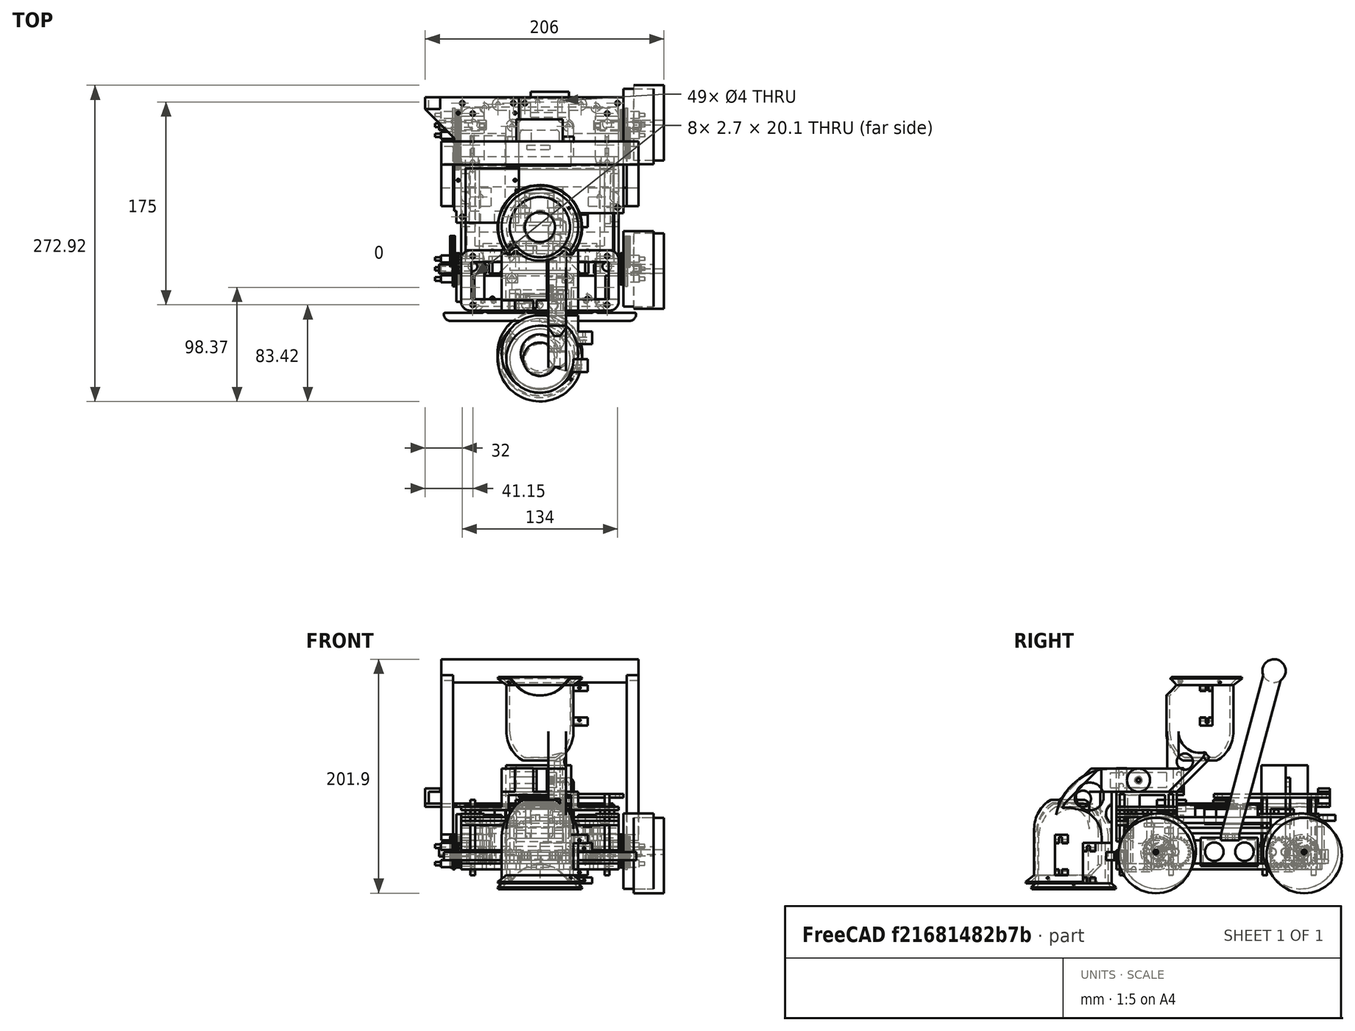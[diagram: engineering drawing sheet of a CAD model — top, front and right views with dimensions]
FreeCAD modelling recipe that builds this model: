
FCSTD DOCUMENT  (FreeCAD 1.0R39319 (Git))
Label: robot - robcup-ber4a3
License: All rights reserved
LicenseURL: https://en.wikipedia.org/wiki/All_rights_reserved
objects: Part::Cylinder×264, Part::Box×177, Part::Cut×164, Part::MultiFuse×149, Part::Fillet×33, Part::FeaturePython×22, Part::Sphere×14, Part::Chamfer×13, Part::Cone×8, Part::Part2DObjectPython×4, Part::Extrusion×4
note: 852 computed .brp shape members not serialized (recipe doc carries the construction recipe); baked Part::Feature solids carry a one-line shape summary decoded from their .brp

FEATURE [Part::Box] Box024  label="立方体004"
  AttacherType = Attacher::AttachEngine3D
  Height = 25
  Length = 51
  Placement = pos=(-51,-93,16) rot=(0,0,1;0rad)
  Width = 5
FEATURE [Part::Box] Box025  label="立方体005"
  AttacherType = Attacher::AttachEngine3D
  Height = 25
  Length = 23
  Placement = pos=(-37,-93,16) rot=(0,0,1;0rad)
  Width = 5
FEATURE [Part::Box] Box026  label="立方体006"
  AttacherType = Attacher::AttachEngine3D
  Height = 10
  Length = 51
  Placement = pos=(-51,-90,31) rot=(0,0,1;0rad)
  Width = 5
FEATURE [Part::Cylinder] Cylinder007  label="円柱007"
  Angle = 360
  AttacherType = Attacher::AttachEngine3D
  FirstAngle = 0
  Height = 32
  Placement = pos=(0,82,0) rot=(0,0,1;0rad)
  Radius = 4
  SecondAngle = 0
FEATURE [Part::Cylinder] Cylinder011  label="円柱011"
  Angle = 360
  AttacherType = Attacher::AttachEngine3D
  FirstAngle = 0
  Height = 32
  Placement = pos=(15.2,-98,0) rot=(0,0,1;0rad)
  Radius = 4
  SecondAngle = 0
FEATURE [Part::Cylinder] Cylinder012  label="円柱012"
  Angle = 360
  AttacherType = Attacher::AttachEngine3D
  FirstAngle = 0
  Height = 42
  Placement = pos=(-68,82,-5) rot=(0,0,1;0rad)
  Radius = 2
  SecondAngle = 0
FEATURE [Part::Box] Box069  label="立方体048"
  AttacherType = Attacher::AttachEngine3D
  Height = 20.1
  Length = 38.8
  Placement = pos=(82,-93,0) rot=(0,0,1;0rad)
  Width = 40.1
FEATURE [Part::Box] Box075  label="立方体054"
  AttacherType = Attacher::AttachEngine3D
  Height = 20.1
  Length = 38.8
  Placement = pos=(82,-93,0) rot=(0,0,1;0rad)
  Width = 40.1
FEATURE [Part::Box] Box084  label="立方体063"
  AttacherType = Attacher::AttachEngine3D
  Height = 20.1
  Length = 2.7
  Placement = pos=(90.8,-99.95,0) rot=(0,0,1;0rad)
  Width = 54
FEATURE [Part::Box] Box097  label="立方体076"
  AttacherType = Attacher::AttachEngine3D
  Height = 25
  Length = 52
  Placement = pos=(-60,-93,16) rot=(0,0,1;0rad)
  Width = 5
FEATURE [Part::Box] Box098  label="立方体077"
  AttacherType = Attacher::AttachEngine3D
  Height = 25
  Length = 35
  Placement = pos=(-52,-88,16) rot=(0,0,1;0rad)
  Width = 5
FEATURE [Part::Box] Box100  label="立方体079"
  AttacherType = Attacher::AttachEngine3D
  Height = 25
  Length = 25
  Placement = pos=(-38.5,-94,16) rot=(0,0,1;0rad)
  Width = 1
FEATURE [Part::Box] Box101  label="立方体080"
  AttacherType = Attacher::AttachEngine3D
  Height = 25
  Length = 15
  Placement = pos=(-33.5,-101,16) rot=(0,0,1;0rad)
  Width = 7
FEATURE [Part::Box] Box102  label="立方体081"
  AttacherType = Attacher::AttachEngine3D
  Height = 5
  Length = 112
  Placement = pos=(-90,-52,-5) rot=(0,0,1;0rad)
  Width = 66
FEATURE [Part::Cylinder] Cylinder033  label="円柱033"
  Angle = 360
  AttacherType = Attacher::AttachEngine3D
  FirstAngle = 0
  Height = 32
  Placement = pos=(30.2,-10,0) rot=(0,0,1;0rad)
  Radius = 4
  SecondAngle = 0
FEATURE [Part::Cylinder] Cylinder034  label="円柱034"
  Angle = 360
  AttacherType = Attacher::AttachEngine3D
  FirstAngle = 0
  Height = 32
  Placement = pos=(-98,-10,0) rot=(0,0,1;0rad)
  Radius = 4
  SecondAngle = 0
FEATURE [Part::Box] Box223  label="立方体201"
  AttacherType = Attacher::AttachEngine3D
  Height = 20.1
  Length = 2.7
  Placement = pos=(90.8,-99.95,0) rot=(0,0,1;0rad)
  Width = 54
FEATURE [Part::Box] Box225  label="立方体203"
  AttacherType = Attacher::AttachEngine3D
  Height = 20.1
  Length = 2.7
  Placement = pos=(109.3,-99.95,0) rot=(0,0,1;0rad)
  Width = 54
FEATURE [Part::MultiFuse] Fusion084
  Placement = pos=(-188,26,0) rot=(0,0,1;0rad)
  Shapes = -> [Box084,Box069]
FEATURE [Part::MultiFuse] Fusion085
  Placement = pos=(-188,100,0) rot=(0,0,1;0rad)
  Shapes = -> [Box223,Box075]
FEATURE [Part::Box] Box226  label="立方体204"
  AttacherType = Attacher::AttachEngine3D
  Height = 20.1
  Length = 38.8
  Placement = pos=(82,-93,0) rot=(0,0,1;0rad)
  Width = 40.1
FEATURE [Part::Box] Box227  label="立方体205"
  AttacherType = Attacher::AttachEngine3D
  Height = 20.1
  Length = 38.8
  Placement = pos=(82,-93,0) rot=(0,0,1;0rad)
  Width = 40.1
FEATURE [Part::MultiFuse] Fusion086
  Placement = pos=(-82.6,26,0) rot=(0,0,1;0rad)
  Shapes = -> [Box226,Box225]
FEATURE [Part::Box] Box076  label="立方体055"
  AttacherType = Attacher::AttachEngine3D
  Height = 20.1
  Length = 2.7
  Placement = pos=(109.3,-99.95,0) rot=(0,0,1;0rad)
  Width = 54
FEATURE [Part::MultiFuse] Fusion087
  Placement = pos=(-82.6,100,0) rot=(0,0,1;0rad)
  Shapes = -> [Box076,Box227]
FEATURE [Part::FeaturePython] CycloidGear  # WARN: FeaturePython — macro-defined, semantics opaque (R4)
  AttacherType = Attacher::AttachEngine3D
  Placement = pos=(-32.8,-91,71) rot=(0,1,0;1.5708rad)
  angular_backlash = 0
  backlash = 0
  clearance = 0.25
  double_helix = false
  head = 0
  head_fillet = 0
  height = 5.5
  helix_angle = 0
  inner_diameter = 12.5
  module = 0.24
  num_teeth = 25
  numpoints = 20
  outer_diameter = 7.5
  pitch_diameter = 6
  root_fillet = 0
  version = 1.3.0
  expr: angular_backlash = backlash / pitch_diameter * 360 ° / pi
  expr: inner_diameter = num_teeth / 2
  expr: pitch_diameter = num_teeth * module
FEATURE [Part::Box] Box259  label="立方体234"
  AttacherType = Attacher::AttachEngine3D
  Height = 3
  Length = 90
  Placement = pos=(-52,-40,42) rot=(0,0,1;0rad)
  Width = 100
FEATURE [Part::Box] Box260  label="立方体235"
  AttacherType = Attacher::AttachEngine3D
  Height = 3
  Length = 56
  Placement = pos=(-104,-22,37) rot=(0,0,1;0rad)
  Width = 88
FEATURE [Part::Cylinder] Cylinder064  label="円柱064"
  Angle = 360
  AttacherType = Attacher::AttachEngine3D
  FirstAngle = 0
  Height = 3
  Placement = pos=(-100.5,62.5,37) rot=(0,0,1;0rad)
  Radius = 1.25
  SecondAngle = 0
FEATURE [Part::Cylinder] Cylinder065  label="円柱065"
  Angle = 360
  AttacherType = Attacher::AttachEngine3D
  FirstAngle = 0
  Height = 3
  Placement = pos=(-51.5,62.5,37) rot=(0,0,1;0rad)
  Radius = 1.25
  SecondAngle = 0
FEATURE [Part::Cylinder] Cylinder066  label="円柱066"
  Angle = 360
  AttacherType = Attacher::AttachEngine3D
  FirstAngle = 0
  Height = 3
  Placement = pos=(-51.5,4.5,37) rot=(0,0,1;0rad)
  Radius = 1.25
  SecondAngle = 0
FEATURE [Part::Cylinder] Cylinder067  label="円柱067"
  Angle = 360
  AttacherType = Attacher::AttachEngine3D
  FirstAngle = 0
  Height = 3
  Placement = pos=(-100.5,4.5,37) rot=(0,0,1;0rad)
  Radius = 1.25
  SecondAngle = 0
FEATURE [Part::Box] Box263  label="立方体237"
  AttacherType = Attacher::AttachEngine3D
  Height = 20.4
  Length = 45.2
  Placement = pos=(-48.6,-98,10) rot=(0,0,1;0rad)
  Width = 5
FEATURE [Part::Cylinder] Cylinder068  label="円柱068"
  Angle = 360
  AttacherType = Attacher::AttachEngine3D
  FirstAngle = 0
  Height = 15
  Placement = pos=(-13,-93,20.2) rot=(1,0,0;1.5708rad)
  Radius = 8
  SecondAngle = 0
FEATURE [Part::Cylinder] Cylinder069  label="円柱069"
  Angle = 360
  AttacherType = Attacher::AttachEngine3D
  FirstAngle = 0
  Height = 15
  Placement = pos=(-39,-93,20.2) rot=(1,0,0;1.5708rad)
  Radius = 8
  SecondAngle = 0
FEATURE [Part::MultiFuse] Fusion112
  Placement = pos=(0,-109,40) rot=(0,0,-1;1.5708rad)
  Refine = true
  Shapes = -> [Box263,Cylinder069,Cylinder068]
FEATURE [Part::Box] Box264  label="立方体238"
  AttacherType = Attacher::AttachEngine3D
  Height = 20.4
  Length = 45.2
  Placement = pos=(-48.6,-98,10) rot=(0,0,1;0rad)
  Width = 5
FEATURE [Part::Cylinder] Cylinder070  label="円柱070"
  Angle = 360
  AttacherType = Attacher::AttachEngine3D
  FirstAngle = 0
  Height = 15
  Placement = pos=(-13,-93,20.2) rot=(1,0,0;1.5708rad)
  Radius = 8
  SecondAngle = 0
FEATURE [Part::Cylinder] Cylinder071  label="円柱071"
  Angle = 360
  AttacherType = Attacher::AttachEngine3D
  FirstAngle = 0
  Height = 15
  Placement = pos=(-39,-93,20.2) rot=(1,0,0;1.5708rad)
  Radius = 8
  SecondAngle = 0
FEATURE [Part::MultiFuse] Fusion113
  Placement = pos=(-67,-57,40) rot=(0,0,1;1.5708rad)
  Refine = true
  Shapes = -> [Box264,Cylinder071,Cylinder070]
FEATURE [Part::Box] Box266  label="立方体240"
  AttacherType = Attacher::AttachEngine3D
  Height = 49.2
  Length = 12
  Placement = pos=(-105,-58.4,48) rot=(1,0,0;1.5708rad)
  Width = 24.4
FEATURE [Part::Box] Box268  label="立方体242"
  AttacherType = Attacher::AttachEngine3D
  Height = 49.2
  Length = 12
  Placement = pos=(26,-58.4,48) rot=(1,0,0;1.5708rad)
  Width = 24.4
FEATURE [Part::Cylinder] Cylinder072  label="円柱072"
  Angle = 360
  AttacherType = Attacher::AttachEngine3D
  FirstAngle = 0
  Height = 40.5
  Placement = pos=(-125,62,10) rot=(0,1,0;1.5708rad)
  Radius = 4
  SecondAngle = 0
FEATURE [Part::FeaturePython] CycloidGear001  # WARN: FeaturePython — macro-defined, semantics opaque (R4)
  AttacherType = Attacher::AttachEngine3D
  Placement = pos=(-111.4,62,10) rot=(0,1,0;1.5708rad)
  angular_backlash = 0
  backlash = 0
  clearance = 0.25
  double_helix = false
  head = 0
  head_fillet = 0
  height = 4
  helix_angle = 0
  inner_diameter = 12.5
  module = 1
  num_teeth = 25
  numpoints = 20
  outer_diameter = 7.5
  pitch_diameter = 25
  root_fillet = 0
  version = 1.3.0
  expr: angular_backlash = backlash / pitch_diameter * 360 ° / pi
  expr: inner_diameter = num_teeth / 2
  expr: pitch_diameter = num_teeth * module
FEATURE [Part::FeaturePython] CycloidGear002  # WARN: FeaturePython — macro-defined, semantics opaque (R4)
  AttacherType = Attacher::AttachEngine3D
  Placement = pos=(-111.45,37,10) rot=(0,1,0;1.5708rad)
  angular_backlash = 0
  backlash = 0
  clearance = 0.25
  double_helix = false
  head = 0
  head_fillet = 0
  height = 4
  helix_angle = 0
  inner_diameter = 12.5
  module = 1
  num_teeth = 25
  numpoints = 20
  outer_diameter = 7.5
  pitch_diameter = 25
  root_fillet = 0
  version = 1.3.0
  expr: angular_backlash = backlash / pitch_diameter * 360 ° / pi
  expr: inner_diameter = num_teeth / 2
  expr: pitch_diameter = num_teeth * module
FEATURE [Part::FeaturePython] CycloidGear003  # WARN: FeaturePython — macro-defined, semantics opaque (R4)
  AttacherType = Attacher::AttachEngine3D
  Placement = pos=(-111.45,37,10) rot=(0,1,0;1.5708rad)
  angular_backlash = 0
  backlash = 0
  clearance = 0.25
  double_helix = false
  head = 0
  head_fillet = 0
  height = 4
  helix_angle = 0
  inner_diameter = 12.5
  module = 0.24
  num_teeth = 25
  numpoints = 20
  outer_diameter = 7.5
  pitch_diameter = 6
  root_fillet = 0
  version = 1.3.0
  expr: angular_backlash = backlash / pitch_diameter * 360 ° / pi
  expr: inner_diameter = num_teeth / 2
  expr: pitch_diameter = num_teeth * module
FEATURE [Part::Sphere] Sphere  label="球体"
  Angle1 = 0
  Angle2 = 60
  Angle3 = 360
  AttacherType = Attacher::AttachEngine3D
  Placement = pos=(-34,-160,45) rot=(0,0,1;0rad)
  Radius = 33
FEATURE [Part::Sphere] Sphere001  label="球体001"
  Angle1 = 0
  Angle2 = 60
  Angle3 = 360
  AttacherType = Attacher::AttachEngine3D
  Placement = pos=(-34,-160,45) rot=(0,0,1;0rad)
  Radius = 30
FEATURE [Part::Cone] Cone  label="円錐"
  Angle = 360
  AttacherType = Attacher::AttachEngine3D
  Height = 5
  Radius1 = 38
  Radius2 = 33
FEATURE [Part::Cone] Cone001  label="円錐001"
  Angle = 360
  AttacherType = Attacher::AttachEngine3D
  Height = 5
  Radius1 = 33
  Radius2 = 30
FEATURE [Part::Cut] Cut053
  Base = -> Cone
  Placement = pos=(-34,-160,0) rot=(0,0,1;0rad)
  Tool = -> Cone001
FEATURE [Part::Chamfer] Chamfer016
  Base = -> Cut053
  EdgeLinks = -> Cut053 [Edge3]
  Edges = 1 edges r=2: [Edge3]
FEATURE [Part::Cylinder] Cylinder073  label="円柱073"
  Angle = 360
  AttacherType = Attacher::AttachEngine3D
  FirstAngle = 0
  Height = 20
  Placement = pos=(-60,-160,-3) rot=(0,-1,0;0.785398rad)
  Radius = 1
  SecondAngle = 0
FEATURE [Part::Cylinder] Cylinder074  label="円柱074"
  Angle = 360
  AttacherType = Attacher::AttachEngine3D
  FirstAngle = 0
  Height = 20
  Placement = pos=(-8,-160,-3) rot=(0,1,0;0.785398rad)
  Radius = 1
  SecondAngle = 0
FEATURE [Part::Box] Box273  label="立方体246"
  AttacherType = Attacher::AttachEngine3D
  Height = 20.1
  Length = 2.7
  Placement = pos=(109.3,-99.95,0) rot=(0,0,1;0rad)
  Width = 54
FEATURE [Part::Box] Box274  label="立方体247"
  AttacherType = Attacher::AttachEngine3D
  Height = 20.1
  Length = 38.8
  Placement = pos=(82,-93,0) rot=(0,0,1;0rad)
  Width = 40.1
FEATURE [Part::MultiFuse] Fusion118
  Placement = pos=(-153.6,-8,61) rot=(0,0,1;0rad)
  Shapes = -> [Box274,Box273]
FEATURE [Part::Cylinder] Cylinder076  label="円柱076"
  Angle = 360
  AttacherType = Attacher::AttachEngine3D
  FirstAngle = 0
  Height = 50
  Placement = pos=(-34,-160,-17) rot=(0,0,1;0rad)
  Radius = 33
  SecondAngle = 0
FEATURE [Part::Box] Box278  label="立方体250"
  AttacherType = Attacher::AttachEngine3D
  Height = 35
  Length = 45.1
  Placement = pos=(-34,-146,-17) rot=(0,0,1;0rad)
  Width = 25
FEATURE [Part::Box] Box279  label="立方体251"
  AttacherType = Attacher::AttachEngine3D
  Height = 32.3
  Length = 12.1
  Placement = pos=(0,8.5,-4.9) rot=(0,0,1;0rad)
  Width = 2.5
FEATURE [Part::Box] Box280  label="立方体252"
  AttacherType = Attacher::AttachEngine3D
  Height = 22.5
  Length = 12.1
  Width = 26.7
FEATURE [Part::Cylinder] Cylinder077  label="円柱077"
  Angle = 360
  AttacherType = Attacher::AttachEngine3D
  FirstAngle = 0
  Height = 3
  Placement = pos=(6.05,0,16.4) rot=(1,0,0;1.5708rad)
  Radius = 2.4
  SecondAngle = 0
FEATURE [Part::MultiFuse] Fusion120
  Placement = pos=(-1,-151,-12) rot=(0,0,1;0rad)
  Shapes = -> [Cylinder077,Box279,Box280]
FEATURE [Part::Cut] Cut056
  Base = -> Box278
  Tool = -> Fusion120
FEATURE [Part::Cut] Cut057
  Base = -> Cut056
  Placement = pos=(0,15,-3) rot=(0,0,1;0rad)
  Tool = -> Cylinder076
FEATURE [Part::MultiFuse] Fusion121
  Placement = pos=(0,0,-3) rot=(0,0,1;0rad)
  Shapes = -> [Fusion118,CycloidGear]
FEATURE [Part::Box] Box281  label="立方体253"
  AttacherType = Attacher::AttachEngine3D
  Height = 20.1
  Length = 16
  Placement = pos=(-60.3,-108,62) rot=(0,0,1;0rad)
  Width = 9
FEATURE [Part::Box] Box283  label="立方体255"
  AttacherType = Attacher::AttachEngine3D
  Height = 3
  Length = 66
  Placement = pos=(-71.6,-108,59) rot=(0,0,1;0rad)
  Width = 58.1
FEATURE [Part::Box] Box286  label="立方体258"
  AttacherType = Attacher::AttachEngine3D
  Height = 16
  Length = 6
  Placement = pos=(-67,-108,46.1) rot=(0,0,1;0rad)
  Width = 9.9
FEATURE [Part::Box] Box288  label="立方体260"
  AttacherType = Attacher::AttachEngine3D
  Height = 16
  Length = 6
  Placement = pos=(-7,-108,46.1) rot=(0,0,1;0rad)
  Width = 20
FEATURE [Part::Cylinder] Cylinder083  label="円柱083"
  Angle = 360
  AttacherType = Attacher::AttachEngine3D
  FirstAngle = 0
  Height = 15
  Placement = pos=(-31.3,-89,72) rot=(0.57735,0.57735,0.57735;2.0944rad)
  Radius = 10
  SecondAngle = 0
FEATURE [Part::Box] Box289  label="立方体261"
  AttacherType = Attacher::AttachEngine3D
  Height = 20
  Length = 15
  Placement = pos=(-31.3,-112,62) rot=(0,0,1;0rad)
  Width = 23
FEATURE [Part::Cylinder] Cylinder084  label="円柱084"
  Angle = 360
  AttacherType = Attacher::AttachEngine3D
  FirstAngle = 0
  Height = 50
  Placement = pos=(-34,-145,-27) rot=(0,0,1;0rad)
  Radius = 30
  SecondAngle = 0
FEATURE [Part::Sphere] Sphere003  label="球体003"
  Angle1 = 0
  Angle2 = 60
  Angle3 = 360
  AttacherType = Attacher::AttachEngine3D
  Placement = pos=(-34,-145,23) rot=(0,0,1;0rad)
  Radius = 30
FEATURE [Part::Cylinder] Cylinder085  label="円柱085"
  Angle = 360
  AttacherType = Attacher::AttachEngine3D
  FirstAngle = 0
  Height = 5
  Placement = pos=(-128.4,53.35,15) rot=(0,1,0;1.5708rad)
  Radius = 1.5
  SecondAngle = 0
FEATURE [Part::FeaturePython] Tube  # WARN: FeaturePython — macro-defined, semantics opaque (R4)
  AttacherType = Attacher::AttachEngine3D
  Height = 2
  InnerRadius = 6
  OuterRadius = 15
  Placement = pos=(-113.4,62,10) rot=(0,1,0;1.5708rad)
FEATURE [Part::Cylinder] Cylinder086  label="円柱086"
  Angle = 360
  AttacherType = Attacher::AttachEngine3D
  FirstAngle = 0
  Height = 5
  Placement = pos=(-128.4,70.66,15) rot=(0,1,0;1.5708rad)
  Radius = 1.5
  SecondAngle = 0
FEATURE [Part::Cylinder] Cylinder087  label="円柱087"
  Angle = 360
  AttacherType = Attacher::AttachEngine3D
  FirstAngle = 0
  Height = 5
  Placement = pos=(-128.4,62,0) rot=(0,1,0;1.5708rad)
  Radius = 1.5
  SecondAngle = 0
FEATURE [Part::FeaturePython] CycloidGear004  # WARN: FeaturePython — macro-defined, semantics opaque (R4)
  AttacherType = Attacher::AttachEngine3D
  Placement = pos=(39.6,62,10) rot=(0,1,0;1.5708rad)
  angular_backlash = 0
  backlash = 0
  clearance = 0.25
  double_helix = false
  head = 0
  head_fillet = 0
  height = 4
  helix_angle = 0
  inner_diameter = 12.5
  module = 1
  num_teeth = 25
  numpoints = 20
  outer_diameter = 7.5
  pitch_diameter = 25
  root_fillet = 0
  version = 1.3.0
  expr: angular_backlash = backlash / pitch_diameter * 360 ° / pi
  expr: inner_diameter = num_teeth / 2
  expr: pitch_diameter = num_teeth * module
FEATURE [Part::Cut] Cut062  label="右下モーター側ギア"
  Base = -> CycloidGear002
  Placement = pos=(4,-10,0) rot=(0,0,1;0rad)
  Tool = -> CycloidGear003
FEATURE [Part::FeaturePython] CycloidGear007  # WARN: FeaturePython — macro-defined, semantics opaque (R4)
  AttacherType = Attacher::AttachEngine3D
  Placement = pos=(-111.45,37,10) rot=(0,1,0;1.5708rad)
  angular_backlash = 0
  backlash = 0
  clearance = 0.25
  double_helix = false
  head = 0
  head_fillet = 0
  height = 4
  helix_angle = 0
  inner_diameter = 12.5
  module = 1
  num_teeth = 25
  numpoints = 20
  outer_diameter = 7.5
  pitch_diameter = 25
  root_fillet = 0
  version = 1.3.0
  expr: angular_backlash = backlash / pitch_diameter * 360 ° / pi
  expr: inner_diameter = num_teeth / 2
  expr: pitch_diameter = num_teeth * module
FEATURE [Part::FeaturePython] CycloidGear008  # WARN: FeaturePython — macro-defined, semantics opaque (R4)
  AttacherType = Attacher::AttachEngine3D
  Placement = pos=(-111.45,37,10) rot=(0,1,0;1.5708rad)
  angular_backlash = 0
  backlash = 0
  clearance = 0.25
  double_helix = false
  head = 0
  head_fillet = 0
  height = 4
  helix_angle = 0
  inner_diameter = 12.5
  module = 0.24
  num_teeth = 25
  numpoints = 20
  outer_diameter = 7.5
  pitch_diameter = 6
  root_fillet = 0
  version = 1.3.0
  expr: angular_backlash = backlash / pitch_diameter * 360 ° / pi
  expr: inner_diameter = num_teeth / 2
  expr: pitch_diameter = num_teeth * module
FEATURE [Part::Cut] Cut064  label="左下モーター側ギア"
  Base = -> CycloidGear007
  Placement = pos=(151.05,0,0) rot=(0,0,1;0rad)
  Tool = -> CycloidGear008
FEATURE [Part::Cylinder] Cylinder088  label="円柱088"
  Angle = 360
  AttacherType = Attacher::AttachEngine3D
  FirstAngle = 0
  Height = 10
  Placement = pos=(-123.4,70.66,15) rot=(0,1,0;1.5708rad)
  Radius = 3
  SecondAngle = 0
FEATURE [Part::Cylinder] Cylinder089  label="円柱089"
  Angle = 360
  AttacherType = Attacher::AttachEngine3D
  FirstAngle = 0
  Height = 10
  Placement = pos=(-123.4,-90.65,15) rot=(0,1,0;1.5708rad)
  Radius = 3
  SecondAngle = 0
FEATURE [Part::Cylinder] Cylinder090  label="円柱090"
  Angle = 360
  AttacherType = Attacher::AttachEngine3D
  FirstAngle = 0
  Height = 10
  Placement = pos=(-123.4,62,0) rot=(0,1,0;1.5708rad)
  Radius = 3
  SecondAngle = 0
FEATURE [Part::Box] Box297  label="立方体269"
  AttacherType = Attacher::AttachEngine3D
  Height = 13
  Length = 30
  Placement = pos=(-94,-22,34) rot=(0,0,1;0rad)
  Width = 65
FEATURE [Part::Cylinder] Cylinder091  label="円柱091"
  Angle = 360
  AttacherType = Attacher::AttachEngine3D
  FirstAngle = 0
  Height = 1.4
  Placement = pos=(-107.4,62,10) rot=(0,1,0;1.5708rad)
  Radius = 5
  SecondAngle = 0
FEATURE [Part::Cylinder] Cylinder093  label="円柱093"
  Angle = 360
  AttacherType = Attacher::AttachEngine3D
  FirstAngle = 0
  Height = 40.5
  Placement = pos=(-125,-82,10) rot=(0,1,0;1.5708rad)
  Radius = 4
  SecondAngle = 0
FEATURE [Part::FeaturePython] CycloidGear009  # WARN: FeaturePython — macro-defined, semantics opaque (R4)
  AttacherType = Attacher::AttachEngine3D
  Placement = pos=(-111.4,-82,10) rot=(0,1,0;1.5708rad)
  angular_backlash = 0
  backlash = 0
  clearance = 0.25
  double_helix = false
  head = 0
  head_fillet = 0
  height = 4
  helix_angle = 0
  inner_diameter = 12.5
  module = 1
  num_teeth = 25
  numpoints = 20
  outer_diameter = 7.5
  pitch_diameter = 25
  root_fillet = 0
  version = 1.3.0
  expr: angular_backlash = backlash / pitch_diameter * 360 ° / pi
  expr: inner_diameter = num_teeth / 2
  expr: pitch_diameter = num_teeth * module
FEATURE [Part::FeaturePython] Tube014  # WARN: FeaturePython — macro-defined, semantics opaque (R4)
  AttacherType = Attacher::AttachEngine3D
  Height = 2
  InnerRadius = 6
  OuterRadius = 15
  Placement = pos=(-113.4,-82,10) rot=(0,1,0;1.5708rad)
FEATURE [Part::Cylinder] Cylinder100  label="円柱100"
  Angle = 360
  AttacherType = Attacher::AttachEngine3D
  FirstAngle = 0
  Height = 10
  Placement = pos=(-123.4,53.35,15) rot=(0,1,0;1.5708rad)
  Radius = 3
  SecondAngle = 0
FEATURE [Part::Cylinder] Cylinder101  label="円柱101"
  Angle = 360
  AttacherType = Attacher::AttachEngine3D
  FirstAngle = 0
  Height = 10
  Placement = pos=(-123.4,-73.34,15) rot=(0,1,0;1.5708rad)
  Radius = 3
  SecondAngle = 0
FEATURE [Part::Cylinder] Cylinder102  label="円柱102"
  Angle = 360
  AttacherType = Attacher::AttachEngine3D
  FirstAngle = 0
  Height = 10
  Placement = pos=(-123.4,-82,0) rot=(0,1,0;1.5708rad)
  Radius = 3
  SecondAngle = 0
FEATURE [Part::Cylinder] Cylinder106  label="円柱106"
  Angle = 360
  AttacherType = Attacher::AttachEngine3D
  FirstAngle = 0
  Height = 1.4
  Placement = pos=(-107.4,-82,10) rot=(0,1,0;1.5708rad)
  Radius = 5
  SecondAngle = 0
FEATURE [Part::FeaturePython] CycloidGear010  # WARN: FeaturePython — macro-defined, semantics opaque (R4)
  AttacherType = Attacher::AttachEngine3D
  Placement = pos=(-111.45,37,10) rot=(0,1,0;1.5708rad)
  angular_backlash = 0
  backlash = 0
  clearance = 0.25
  double_helix = false
  head = 0
  head_fillet = 0
  height = 4
  helix_angle = 0
  inner_diameter = 12.5
  module = 1
  num_teeth = 25
  numpoints = 20
  outer_diameter = 7.5
  pitch_diameter = 25
  root_fillet = 0
  version = 1.3.0
  expr: angular_backlash = backlash / pitch_diameter * 360 ° / pi
  expr: inner_diameter = num_teeth / 2
  expr: pitch_diameter = num_teeth * module
FEATURE [Part::FeaturePython] CycloidGear011  # WARN: FeaturePython — macro-defined, semantics opaque (R4)
  AttacherType = Attacher::AttachEngine3D
  Placement = pos=(-111.45,37,10) rot=(0,1,0;1.5708rad)
  angular_backlash = 0
  backlash = 0
  clearance = 0.25
  double_helix = false
  head = 0
  head_fillet = 0
  height = 4
  helix_angle = 0
  inner_diameter = 12.5
  module = 0.24
  num_teeth = 25
  numpoints = 20
  outer_diameter = 7.5
  pitch_diameter = 6
  root_fillet = 0
  version = 1.3.0
  expr: angular_backlash = backlash / pitch_diameter * 360 ° / pi
  expr: inner_diameter = num_teeth / 2
  expr: pitch_diameter = num_teeth * module
FEATURE [Part::Cut] Cut073  label="右上モーター側ギア"
  Base = -> CycloidGear010
  Placement = pos=(0.05,-94,0) rot=(0,0,1;0rad)
  Tool = -> CycloidGear011
FEATURE [Part::FeaturePython] Tube017  # WARN: FeaturePython — macro-defined, semantics opaque (R4)
  AttacherType = Attacher::AttachEngine3D
  Height = 2
  InnerRadius = 6
  OuterRadius = 15
  Placement = pos=(43.6,62,10) rot=(0,1,0;1.5708rad)
FEATURE [Part::Cylinder] Cylinder108  label="円柱108"
  Angle = 360
  AttacherType = Attacher::AttachEngine3D
  FirstAngle = 0
  Height = 1.4
  Placement = pos=(38.2,62,10) rot=(0,1,0;1.5708rad)
  Radius = 5
  SecondAngle = 0
FEATURE [Part::Cylinder] Cylinder109  label="円柱109"
  Angle = 360
  AttacherType = Attacher::AttachEngine3D
  FirstAngle = 0
  Height = 10
  Placement = pos=(45.6,70.66,15) rot=(0,1,0;1.5708rad)
  Radius = 3
  SecondAngle = 0
FEATURE [Part::Cylinder] Cylinder110  label="円柱110"
  Angle = 360
  AttacherType = Attacher::AttachEngine3D
  FirstAngle = 0
  Height = 10
  Placement = pos=(45.6,53.35,15) rot=(0,1,0;1.5708rad)
  Radius = 3
  SecondAngle = 0
FEATURE [Part::Cylinder] Cylinder111  label="円柱111"
  Angle = 360
  AttacherType = Attacher::AttachEngine3D
  FirstAngle = 0
  Height = 10
  Placement = pos=(45.6,62,0) rot=(0,1,0;1.5708rad)
  Radius = 3
  SecondAngle = 0
FEATURE [Part::Cylinder] Cylinder113  label="円柱113"
  Angle = 360
  AttacherType = Attacher::AttachEngine3D
  FirstAngle = 0
  Height = 5
  Placement = pos=(55.6,70.66,15) rot=(0,1,0;1.5708rad)
  Radius = 1.5
  SecondAngle = 0
FEATURE [Part::Cylinder] Cylinder114  label="円柱114"
  Angle = 360
  AttacherType = Attacher::AttachEngine3D
  FirstAngle = 0
  Height = 5
  Placement = pos=(55.6,53.35,15) rot=(0,1,0;1.5708rad)
  Radius = 1.5
  SecondAngle = 0
FEATURE [Part::Cylinder] Cylinder115  label="円柱115"
  Angle = 360
  AttacherType = Attacher::AttachEngine3D
  FirstAngle = 0
  Height = 5
  Placement = pos=(55.6,62,0) rot=(0,1,0;1.5708rad)
  Radius = 1.5
  SecondAngle = 0
FEATURE [Part::Cylinder] Cylinder117  label="円柱117"
  Angle = 360
  AttacherType = Attacher::AttachEngine3D
  FirstAngle = 0
  Height = 40.5
  Placement = pos=(16.7,62,10) rot=(0,1,0;1.5708rad)
  Radius = 4
  SecondAngle = 0
FEATURE [Part::FeaturePython] CycloidGear012  # WARN: FeaturePython — macro-defined, semantics opaque (R4)
  AttacherType = Attacher::AttachEngine3D
  Placement = pos=(-111.45,37,10) rot=(0,1,0;1.5708rad)
  angular_backlash = 0
  backlash = 0
  clearance = 0.25
  double_helix = false
  head = 0
  head_fillet = 0
  height = 4
  helix_angle = 0
  inner_diameter = 12.5
  module = 1
  num_teeth = 25
  numpoints = 20
  outer_diameter = 7.5
  pitch_diameter = 25
  root_fillet = 0
  version = 1.3.0
  expr: angular_backlash = backlash / pitch_diameter * 360 ° / pi
  expr: inner_diameter = num_teeth / 2
  expr: pitch_diameter = num_teeth * module
FEATURE [Part::FeaturePython] CycloidGear013  # WARN: FeaturePython — macro-defined, semantics opaque (R4)
  AttacherType = Attacher::AttachEngine3D
  Placement = pos=(-111.45,37,10) rot=(0,1,0;1.5708rad)
  angular_backlash = 0
  backlash = 0
  clearance = 0.25
  double_helix = false
  head = 0
  head_fillet = 0
  height = 4
  helix_angle = 0
  inner_diameter = 12.5
  module = 0.24
  num_teeth = 25
  numpoints = 20
  outer_diameter = 7.5
  pitch_diameter = 6
  root_fillet = 0
  version = 1.3.0
  expr: angular_backlash = backlash / pitch_diameter * 360 ° / pi
  expr: inner_diameter = num_teeth / 2
  expr: pitch_diameter = num_teeth * module
FEATURE [Part::Cut] Cut074  label="左上モーター側ギア"
  Base = -> CycloidGear012
  Placement = pos=(151.05,-94,0) rot=(0,0,1;0rad)
  Tool = -> CycloidGear013
FEATURE [Part::FeaturePython] CycloidGear014  # WARN: FeaturePython — macro-defined, semantics opaque (R4)
  AttacherType = Attacher::AttachEngine3D
  Placement = pos=(39.6,-82,10) rot=(0,1,0;1.5708rad)
  angular_backlash = 0
  backlash = 0
  clearance = 0.25
  double_helix = false
  head = 0
  head_fillet = 0
  height = 4
  helix_angle = 0
  inner_diameter = 12.5
  module = 1
  num_teeth = 25
  numpoints = 20
  outer_diameter = 7.5
  pitch_diameter = 25
  root_fillet = 0
  version = 1.3.0
  expr: angular_backlash = backlash / pitch_diameter * 360 ° / pi
  expr: inner_diameter = num_teeth / 2
  expr: pitch_diameter = num_teeth * module
FEATURE [Part::Cylinder] Cylinder118  label="円柱118"
  Angle = 360
  AttacherType = Attacher::AttachEngine3D
  FirstAngle = 0
  Height = 1.4
  Placement = pos=(38.2,-82,10) rot=(0,1,0;1.5708rad)
  Radius = 5
  SecondAngle = 0
FEATURE [Part::Cylinder] Cylinder119  label="円柱119"
  Angle = 360
  AttacherType = Attacher::AttachEngine3D
  FirstAngle = 0
  Height = 40.5
  Placement = pos=(16.7,-82,10) rot=(0,1,0;1.5708rad)
  Radius = 4
  SecondAngle = 0
FEATURE [Part::Cylinder] Cylinder121  label="円柱121"
  Angle = 360
  AttacherType = Attacher::AttachEngine3D
  FirstAngle = 0
  Height = 10
  Placement = pos=(45.6,-73.34,15) rot=(0,1,0;1.5708rad)
  Radius = 3
  SecondAngle = 0
FEATURE [Part::Cylinder] Cylinder122  label="円柱122"
  Angle = 360
  AttacherType = Attacher::AttachEngine3D
  FirstAngle = 0
  Height = 10
  Placement = pos=(45.6,-90.65,15) rot=(0,1,0;1.5708rad)
  Radius = 3
  SecondAngle = 0
FEATURE [Part::Cylinder] Cylinder123  label="円柱123"
  Angle = 360
  AttacherType = Attacher::AttachEngine3D
  FirstAngle = 0
  Height = 10
  Placement = pos=(45.6,-82,0) rot=(0,1,0;1.5708rad)
  Radius = 3
  SecondAngle = 0
FEATURE [Part::Cylinder] Cylinder124  label="円柱124"
  Angle = 360
  AttacherType = Attacher::AttachEngine3D
  FirstAngle = 0
  Height = 5
  Placement = pos=(55.6,-73.34,15) rot=(0,1,0;1.5708rad)
  Radius = 1.5
  SecondAngle = 0
FEATURE [Part::Cylinder] Cylinder125  label="円柱125"
  Angle = 360
  AttacherType = Attacher::AttachEngine3D
  FirstAngle = 0
  Height = 5
  Placement = pos=(55.6,-90.65,15) rot=(0,1,0;1.5708rad)
  Radius = 1.5
  SecondAngle = 0
FEATURE [Part::Cylinder] Cylinder126  label="円柱126"
  Angle = 360
  AttacherType = Attacher::AttachEngine3D
  FirstAngle = 0
  Height = 5
  Placement = pos=(55.6,-82,0) rot=(0,1,0;1.5708rad)
  Radius = 1.5
  SecondAngle = 0
FEATURE [Part::FeaturePython] Tube018  # WARN: FeaturePython — macro-defined, semantics opaque (R4)
  AttacherType = Attacher::AttachEngine3D
  Height = 2
  InnerRadius = 6
  OuterRadius = 15
  Placement = pos=(43.6,-82,10) rot=(0,1,0;1.5708rad)
FEATURE [Part::Box] Box309  label="立方体281"
  AttacherType = Attacher::AttachEngine3D
  Height = 5
  Length = 43
  Placement = pos=(8,-18,0) rot=(0,0,1;0rad)
  Width = 16
FEATURE [Part::Box] Box310  label="立方体282"
  AttacherType = Attacher::AttachEngine3D
  Height = 5
  Length = 43
  Placement = pos=(-119,-18,0) rot=(0,0,1;0rad)
  Width = 16
FEATURE [Part::Cylinder] Cylinder127  label="円柱127"
  Angle = 360
  AttacherType = Attacher::AttachEngine3D
  FirstAngle = 0
  Height = 170
  Placement = pos=(-119,28,146.3) rot=(0,1,0;1.5708rad)
  Radius = 10
  SecondAngle = 0
FEATURE [Part::Cylinder] Cylinder001  label="円柱001"
  Angle = 360
  AttacherType = Attacher::AttachEngine3D
  FirstAngle = 0
  Height = 0.8
  Radius = 7.8
  SecondAngle = 0
FEATURE [Part::Cylinder] Cylinder128  label="円柱128"
  Angle = 360
  AttacherType = Attacher::AttachEngine3D
  FirstAngle = 0
  Height = 4
  Radius = 7
  SecondAngle = 0
FEATURE [Part::MultiFuse] Fusion137
  Placement = pos=(-107.4,62,10) rot=(0,-1,0;1.5708rad)
  Shapes = -> [Cylinder001,Cylinder128]
FEATURE [Part::Cut] Cut
  Base = -> CycloidGear001
  Tool = -> Fusion137
FEATURE [Part::Cylinder] Cylinder129  label="円柱129"
  Angle = 360
  AttacherType = Attacher::AttachEngine3D
  FirstAngle = 0
  Height = 0.8
  Radius = 7.8
  SecondAngle = 0
FEATURE [Part::Cylinder] Cylinder130  label="円柱130"
  Angle = 360
  AttacherType = Attacher::AttachEngine3D
  FirstAngle = 0
  Height = 4
  Radius = 7
  SecondAngle = 0
FEATURE [Part::MultiFuse] Fusion138
  Placement = pos=(-107.4,-82,10) rot=(0,-1,0;1.5708rad)
  Shapes = -> [Cylinder129,Cylinder130]
FEATURE [Part::Cut] Cut087
  Base = -> CycloidGear009
  Tool = -> Fusion138
FEATURE [Part::Cylinder] Cylinder131  label="円柱131"
  Angle = 360
  AttacherType = Attacher::AttachEngine3D
  FirstAngle = 0
  Height = 0.8
  Radius = 7.8
  SecondAngle = 0
FEATURE [Part::Cylinder] Cylinder132  label="円柱132"
  Angle = 360
  AttacherType = Attacher::AttachEngine3D
  FirstAngle = 0
  Height = 4
  Radius = 7
  SecondAngle = 0
FEATURE [Part::MultiFuse] Fusion139
  Placement = pos=(39.6,-82,10) rot=(0,1,0;1.5708rad)
  Shapes = -> [Cylinder131,Cylinder132]
FEATURE [Part::Cylinder] Cylinder133  label="円柱133"
  Angle = 360
  AttacherType = Attacher::AttachEngine3D
  FirstAngle = 0
  Height = 0.8
  Radius = 7.8
  SecondAngle = 0
FEATURE [Part::Cylinder] Cylinder134  label="円柱134"
  Angle = 360
  AttacherType = Attacher::AttachEngine3D
  FirstAngle = 0
  Height = 4
  Radius = 7
  SecondAngle = 0
FEATURE [Part::MultiFuse] Fusion140
  Placement = pos=(39.6,62,10) rot=(0,1,0;1.5708rad)
  Shapes = -> [Cylinder133,Cylinder134]
FEATURE [Part::Cut] Cut088
  Base = -> CycloidGear014
  Tool = -> Fusion139
FEATURE [Part::Cut] Cut089
  Base = -> CycloidGear004
  Tool = -> Fusion140
FEATURE [Part::Cylinder] Cylinder135  label="円柱135"
  Angle = 360
  AttacherType = Attacher::AttachEngine3D
  FirstAngle = 0
  Height = 47.8
  Placement = pos=(9.4,62,10) rot=(0,1,0;1.5708rad)
  Radius = 2
  SecondAngle = 0
FEATURE [Part::Cylinder] Cylinder136  label="円柱136"
  Angle = 360
  AttacherType = Attacher::AttachEngine3D
  FirstAngle = 0
  Height = 47.8
  Placement = pos=(9.4,-82,10) rot=(0,1,0;1.5708rad)
  Radius = 2
  SecondAngle = 0
FEATURE [Part::MultiFuse] Fusion141
  Shapes = -> [Cylinder108,Cylinder117]
FEATURE [Part::Cut] Cut092  label="左下車軸"
  Base = -> Fusion141
  Placement = pos=(-4,-10,0) rot=(0,0,1;0rad)
  Tool = -> Cylinder135
FEATURE [Part::Cylinder] Cylinder138  label="円柱138"
  Angle = 360
  AttacherType = Attacher::AttachEngine3D
  FirstAngle = 0
  Height = 47.8
  Placement = pos=(-125,62,10) rot=(0,1,0;1.5708rad)
  Radius = 2
  SecondAngle = 0
FEATURE [Part::MultiFuse] Fusion142
  Shapes = -> [Cylinder072,Cylinder091]
FEATURE [Part::Cut] Cut095  label="右下車軸"
  Base = -> Fusion142
  Placement = pos=(4,-10,0) rot=(0,0,1;0rad)
  Tool = -> Cylinder138
FEATURE [Part::MultiFuse] Fusion143
  Shapes = -> [Cylinder119,Cylinder118]
FEATURE [Part::Cut] Cut096  label="右上車軸"
  Base = -> Fusion143
  Placement = pos=(-4,10,0) rot=(0,0,1;0rad)
  Tool = -> Cylinder136
FEATURE [Part::Cylinder] Cylinder142  label="円柱142"
  Angle = 360
  AttacherType = Attacher::AttachEngine3D
  FirstAngle = 0
  Height = 5
  Placement = pos=(-128.4,-90.65,15) rot=(0,1,0;1.5708rad)
  Radius = 1.5
  SecondAngle = 0
FEATURE [Part::Cylinder] Cylinder143  label="円柱143"
  Angle = 360
  AttacherType = Attacher::AttachEngine3D
  FirstAngle = 0
  Height = 5
  Placement = pos=(-128.4,-82,0) rot=(0,1,0;1.5708rad)
  Radius = 1.5
  SecondAngle = 0
FEATURE [Part::Cylinder] Cylinder144  label="円柱144"
  Angle = 360
  AttacherType = Attacher::AttachEngine3D
  FirstAngle = 0
  Height = 5
  Placement = pos=(-128.4,-73.34,15) rot=(0,1,0;1.5708rad)
  Radius = 1.5
  SecondAngle = 0
FEATURE [Part::Cylinder] Cylinder145  label="円柱145"
  Angle = 360
  AttacherType = Attacher::AttachEngine3D
  FirstAngle = 0
  Height = 47.8
  Placement = pos=(-125,-82,10) rot=(0,1,0;1.5708rad)
  Radius = 2
  SecondAngle = 0
FEATURE [Part::MultiFuse] Fusion144
  Shapes = -> [Cylinder093,Cylinder106]
FEATURE [Part::Cut] Cut098  label="左上車軸"
  Base = -> Fusion144
  Placement = pos=(4,10,0) rot=(0,0,1;0rad)
  Tool = -> Cylinder145
FEATURE [Part::MultiFuse] Fusion145  label="右上車軸側ギア"
  Placement = pos=(4,10,0) rot=(0,0,1;0rad)
  Shapes = -> [Cylinder142,Cylinder089,Cylinder143,Cylinder102,Cylinder144,Cylinder101,Tube014,Cut087]
FEATURE [Part::MultiFuse] Fusion146  label="左上車軸側ギア"
  Placement = pos=(-4,10,0) rot=(0,0,1;0rad)
  Shapes = -> [Cylinder124,Cylinder121,Cylinder122,Cylinder125,Cylinder126,Cylinder123,Tube018,Cut088]
FEATURE [Part::MultiFuse] Fusion147  label="左下車軸側ギア"
  Placement = pos=(-4,-10,0) rot=(0,0,1;0rad)
  Shapes = -> [Cylinder109,Cylinder113,Cylinder111,Cylinder115,Cylinder110,Cylinder114,Tube017,Cut089]
FEATURE [Part::MultiFuse] Fusion148  label="右下車軸側ギア"
  Placement = pos=(4,-10,0) rot=(0,0,1;0rad)
  Shapes = -> [Cylinder085,Cylinder100,Cylinder087,Cylinder090,Cylinder086,Cylinder088,Tube,Cut]
FEATURE [Part::Cylinder] Cylinder163  label="円柱163"
  Angle = 360
  AttacherType = Attacher::AttachEngine3D
  FirstAngle = 0
  Height = 20
  Placement = pos=(9.4,51.9,5) rot=(0,1,0;1.5708rad)
  Radius = 2
  SecondAngle = 0
FEATURE [Part::Cylinder] Cylinder164  label="円柱164"
  Angle = 360
  AttacherType = Attacher::AttachEngine3D
  FirstAngle = 0
  Height = 20
  Placement = pos=(9.4,51.9,15) rot=(0,1,0;1.5708rad)
  Radius = 2
  SecondAngle = 0
FEATURE [Part::Cylinder] Cylinder165  label="円柱165"
  Angle = 360
  AttacherType = Attacher::AttachEngine3D
  FirstAngle = 0
  Height = 20
  Placement = pos=(9.4,2.2,15) rot=(0,1,0;1.5708rad)
  Radius = 2
  SecondAngle = 0
FEATURE [Part::Cylinder] Cylinder166  label="円柱166"
  Angle = 360
  AttacherType = Attacher::AttachEngine3D
  FirstAngle = 0
  Height = 20
  Placement = pos=(9.4,2.2,5) rot=(0,1,0;1.5708rad)
  Radius = 2
  SecondAngle = 0
FEATURE [Part::Cylinder] Cylinder167  label="円柱167"
  Angle = 360
  AttacherType = Attacher::AttachEngine3D
  FirstAngle = 0
  Height = 20
  Placement = pos=(9.4,-22.1,5) rot=(0,1,0;1.5708rad)
  Radius = 2
  SecondAngle = 0
FEATURE [Part::Cylinder] Cylinder168  label="円柱168"
  Angle = 360
  AttacherType = Attacher::AttachEngine3D
  FirstAngle = 0
  Height = 20
  Placement = pos=(9.4,-22.1,15) rot=(0,1,0;1.5708rad)
  Radius = 2
  SecondAngle = 0
FEATURE [Part::Cylinder] Cylinder169  label="円柱169"
  Angle = 360
  AttacherType = Attacher::AttachEngine3D
  FirstAngle = 0
  Height = 20
  Placement = pos=(9.4,-71.8,15) rot=(0,1,0;1.5708rad)
  Radius = 2
  SecondAngle = 0
FEATURE [Part::Cylinder] Cylinder170  label="円柱170"
  Angle = 360
  AttacherType = Attacher::AttachEngine3D
  FirstAngle = 0
  Height = 20
  Placement = pos=(9.4,-71.8,5) rot=(0,1,0;1.5708rad)
  Radius = 2
  SecondAngle = 0
FEATURE [Part::Cylinder] Cylinder171  label="円柱171"
  Angle = 360
  AttacherType = Attacher::AttachEngine3D
  FirstAngle = 0
  Height = 20
  Placement = pos=(-97.2,51.9,5) rot=(0,1,0;1.5708rad)
  Radius = 2
  SecondAngle = 0
FEATURE [Part::Cylinder] Cylinder172  label="円柱172"
  Angle = 360
  AttacherType = Attacher::AttachEngine3D
  FirstAngle = 0
  Height = 20
  Placement = pos=(-97.2,51.9,15) rot=(0,1,0;1.5708rad)
  Radius = 2
  SecondAngle = 0
FEATURE [Part::Cylinder] Cylinder173  label="円柱173"
  Angle = 360
  AttacherType = Attacher::AttachEngine3D
  FirstAngle = 0
  Height = 20
  Placement = pos=(-97.2,2.2,15) rot=(0,1,0;1.5708rad)
  Radius = 2
  SecondAngle = 0
FEATURE [Part::Cylinder] Cylinder174  label="円柱174"
  Angle = 360
  AttacherType = Attacher::AttachEngine3D
  FirstAngle = 0
  Height = 20
  Placement = pos=(-97.2,2.2,5) rot=(0,1,0;1.5708rad)
  Radius = 2
  SecondAngle = 0
FEATURE [Part::Cylinder] Cylinder175  label="円柱175"
  Angle = 360
  AttacherType = Attacher::AttachEngine3D
  FirstAngle = 0
  Height = 20
  Placement = pos=(-97.2,-22.1,5) rot=(0,1,0;1.5708rad)
  Radius = 2
  SecondAngle = 0
FEATURE [Part::Cylinder] Cylinder176  label="円柱176"
  Angle = 360
  AttacherType = Attacher::AttachEngine3D
  FirstAngle = 0
  Height = 20
  Placement = pos=(-97.2,-22.1,15) rot=(0,1,0;1.5708rad)
  Radius = 2
  SecondAngle = 0
FEATURE [Part::Cylinder] Cylinder177  label="円柱177"
  Angle = 360
  AttacherType = Attacher::AttachEngine3D
  FirstAngle = 0
  Height = 20
  Placement = pos=(-97.2,-71.8,15) rot=(0,1,0;1.5708rad)
  Radius = 2
  SecondAngle = 0
FEATURE [Part::Cylinder] Cylinder178  label="円柱178"
  Angle = 360
  AttacherType = Attacher::AttachEngine3D
  FirstAngle = 0
  Height = 20
  Placement = pos=(-97.2,-71.8,5) rot=(0,1,0;1.5708rad)
  Radius = 2
  SecondAngle = 0
FEATURE [Part::Cut] Cut116
  Base = -> Fusion087
  Tool = -> Cylinder164
FEATURE [Part::Cut] Cut117
  Base = -> Cut116
  Tool = -> Cylinder163
FEATURE [Part::Cut] Cut118
  Base = -> Cut117
  Tool = -> Cylinder165
FEATURE [Part::Cut] Cut119  label="左下モーターー"
  Base = -> Cut118
  Placement = pos=(-4.2,24.9,47.1) rot=(-1,0,0;1.5708rad)
  Tool = -> Cylinder166
FEATURE [Part::Cut] Cut120
  Base = -> Fusion086
  Tool = -> Cylinder168
FEATURE [Part::Cut] Cut121
  Base = -> Cut120
  Tool = -> Cylinder167
FEATURE [Part::Cut] Cut122
  Base = -> Cut121
  Tool = -> Cylinder169
FEATURE [Part::Cut] Cut123  label="左上モーター"
  Base = -> Cut122
  Placement = pos=(-4.2,-98.1,-26.9) rot=(-1,0,0;1.5708rad)
  Tool = -> Cylinder170
FEATURE [Part::Cut] Cut124
  Base = -> Fusion085
  Tool = -> Cylinder172
FEATURE [Part::Cut] Cut125
  Base = -> Cut124
  Tool = -> Cylinder171
FEATURE [Part::Cut] Cut126
  Base = -> Cut125
  Tool = -> Cylinder173
FEATURE [Part::Cut] Cut128
  Base = -> Fusion084
  Tool = -> Cylinder176
FEATURE [Part::Cut] Cut129
  Base = -> Cut128
  Tool = -> Cylinder175
FEATURE [Part::Cut] Cut130
  Base = -> Cut129
  Tool = -> Cylinder177
FEATURE [Part::Cut] Cut131  label="右上モーター"
  Base = -> Cut130
  Placement = pos=(4,-98.1,-26.9) rot=(-1,0,0;1.5708rad)
  Tool = -> Cylinder178
FEATURE [Part::Part2DObjectPython] Wire004  # Draft 2D object (typed FeaturePython)
  Area = 2400
  ChamferSize = 0
  Closed = true
  End = (40,150,0)
  FilletRadius = 0
  Length = 342.483
  MakeFace = true
  Points = (4) [(0,0,0),(16,0,0),(56,150,0),(40,150,0)]
  Start = (0,0,0)
  Subdivisions = 0
FEATURE [Part::Extrusion] Extrude009
  Base = -> Wire004
  Dir = (0,0,1)
  DirMode = 2
  FaceMakerClass = Part::FaceMakerBullseye
  FaceMakerMode = 3
  LengthFwd = 10
  LengthRev = 0
  Solid = false
  Symmetric = false
FEATURE [Part::Fillet] Fillet002
  Base = -> Extrude009
  EdgeLinks = -> Extrude009 [Edge5,Edge8]
  Edges = 2 edges r=7.72: [Edge5,Edge8]
  Placement = pos=(41,-18,5) rot=(0.57735,0.57735,0.57735;2.0944rad)
FEATURE [Part::Part2DObjectPython] Wire005  # Draft 2D object (typed FeaturePython)
  Area = 2400
  ChamferSize = 0
  Closed = true
  End = (40,150,0)
  FilletRadius = 0
  Length = 342.483
  MakeFace = true
  Points = (4) [(0,0,0),(16,0,0),(56,150,0),(40,150,0)]
  Start = (0,0,0)
  Subdivisions = 0
FEATURE [Part::Extrusion] Extrude010
  Base = -> Wire005
  Dir = (0,0,1)
  DirMode = 2
  FaceMakerClass = Part::FaceMakerBullseye
  FaceMakerMode = 3
  LengthFwd = 10
  LengthRev = 0
  Solid = false
  Symmetric = false
FEATURE [Part::Fillet] Fillet003
  Base = -> Extrude010
  EdgeLinks = -> Extrude010 [Edge5,Edge8]
  Edges = 2 edges r=7.72: [Edge5,Edge8]
  Placement = pos=(-119,-18,5) rot=(0.57735,0.57735,0.57735;2.0944rad)
FEATURE [Part::Cylinder] Cylinder179  label="円柱179"
  Angle = 360
  AttacherType = Attacher::AttachEngine3D
  FirstAngle = 0
  Height = 30
  Placement = pos=(-71.6,-105.8,73) rot=(0,1,0;1.5708rad)
  Radius = 2
  SecondAngle = 0
FEATURE [Part::Cylinder] Cylinder180  label="円柱180"
  Angle = 360
  AttacherType = Attacher::AttachEngine3D
  FirstAngle = 0
  Height = 33
  Placement = pos=(-74.6,-105.8,63) rot=(0,1,0;1.5708rad)
  Radius = 2
  SecondAngle = 0
FEATURE [Part::Cylinder] Cylinder181  label="円柱181"
  Angle = 360
  AttacherType = Attacher::AttachEngine3D
  FirstAngle = 0
  Height = 30
  Placement = pos=(-71.6,-56.2,73) rot=(0,1,0;1.5708rad)
  Radius = 2
  SecondAngle = 0
FEATURE [Part::Cylinder] Cylinder182  label="円柱182"
  Angle = 360
  AttacherType = Attacher::AttachEngine3D
  FirstAngle = 0
  Height = 33
  Placement = pos=(-74.6,-56.2,63) rot=(0,1,0;1.5708rad)
  Radius = 2
  SecondAngle = 0
FEATURE [Part::Cylinder] Cylinder183  label="円柱183"
  Angle = 360
  AttacherType = Attacher::AttachEngine3D
  FirstAngle = 0
  Height = 30
  Placement = pos=(-71.6,-105.8,73) rot=(0,1,0;1.5708rad)
  Radius = 2
  SecondAngle = 0
FEATURE [Part::Cylinder] Cylinder184  label="円柱184"
  Angle = 360
  AttacherType = Attacher::AttachEngine3D
  FirstAngle = 0
  Height = 33
  Placement = pos=(-74.6,-105.8,63) rot=(0,1,0;1.5708rad)
  Radius = 2
  SecondAngle = 0
FEATURE [Part::Cylinder] Cylinder185  label="円柱185"
  Angle = 360
  AttacherType = Attacher::AttachEngine3D
  FirstAngle = 0
  Height = 30
  Placement = pos=(-71.6,-56.2,73) rot=(0,1,0;1.5708rad)
  Radius = 2
  SecondAngle = 0
FEATURE [Part::Cylinder] Cylinder186  label="円柱186"
  Angle = 360
  AttacherType = Attacher::AttachEngine3D
  FirstAngle = 0
  Height = 33
  Placement = pos=(-74.6,-56.2,63) rot=(0,1,0;1.5708rad)
  Radius = 2
  SecondAngle = 0
FEATURE [Part::Cut] Cut140
  Base = -> Fusion121
  Tool = -> Cylinder183
FEATURE [Part::Cut] Cut141
  Base = -> Cut140
  Tool = -> Cylinder184
FEATURE [Part::Cut] Cut142
  Base = -> Cut141
  Tool = -> Cylinder185
FEATURE [Part::Cut] Cut143  label="レスキューアームモータ　"
  Base = -> Cut142
  Placement = pos=(4.7,2,4) rot=(0,0,1;0rad)
  Tool = -> Cylinder186
FEATURE [Part::MultiFuse] Fusion
  Shapes = -> [Box097,Box098]
FEATURE [Part::Cylinder] Cylinder187  label="円柱187"
  Angle = 360
  AttacherType = Attacher::AttachEngine3D
  FirstAngle = 0
  Height = 13
  Placement = pos=(-55,-69,-5) rot=(0,0,1;0rad)
  Radius = 2
  SecondAngle = 0
FEATURE [Part::Cylinder] Cylinder188  label="円柱188"
  Angle = 360
  AttacherType = Attacher::AttachEngine3D
  FirstAngle = 0
  Height = 13
  Placement = pos=(-12,-69,-5) rot=(0,0,1;0rad)
  Radius = 2
  SecondAngle = 0
FEATURE [Part::Cylinder] Cylinder190  label="円柱190"
  Angle = 360
  AttacherType = Attacher::AttachEngine3D
  FirstAngle = 0
  Height = 20
  Placement = pos=(-18.5,-88,34.5) rot=(1,0,0;1.5708rad)
  Radius = 2
  SecondAngle = 0
FEATURE [Part::Box] Box321  label="立方体293"
  AttacherType = Attacher::AttachEngine3D
  Height = 25
  Length = 23
  Placement = pos=(-46,-93,16) rot=(0,0,1;0rad)
  Width = 5
FEATURE [Part::Cut] Cut144
  Base = -> Fusion
  Placement = pos=(0,-40,96) rot=(1,0,0;1.5708rad)
  Tool = -> Box321
FEATURE [Part::Cylinder] Cylinder192  label="円柱192"
  Angle = 360
  AttacherType = Attacher::AttachEngine3D
  FirstAngle = 0
  Height = 13
  Placement = pos=(-16,-69,-5) rot=(0,0,1;0rad)
  Radius = 2
  SecondAngle = 0
FEATURE [Part::Cut] Cut147
  Base = -> Cut144
  Tool = -> Cylinder187
FEATURE [Part::Cut] Cut148  label="ライントレースカメラふた　"
  Base = -> Cut147
  Placement = pos=(0,8,42) rot=(0,0,1;0rad)
  Tool = -> Cylinder188
FEATURE [Part::Box] Box325  label="立方体297"
  AttacherType = Attacher::AttachEngine3D
  Height = 13
  Length = 12
  Placement = pos=(-85,-32,34) rot=(0,0,1;0rad)
  Width = 10
FEATURE [Part::Cylinder] Cylinder196  label="円柱196"
  Angle = 360
  AttacherType = Attacher::AttachEngine3D
  FirstAngle = 0
  Height = 20
  Placement = pos=(-57,-27,32) rot=(0,0,1;0rad)
  Radius = 2
  SecondAngle = 0
FEATURE [Part::Cylinder] Cylinder197  label="円柱197"
  Angle = 360
  AttacherType = Attacher::AttachEngine3D
  FirstAngle = 0
  Height = 20
  Placement = pos=(-101,71,32) rot=(0,0,1;0rad)
  Radius = 2
  SecondAngle = 0
FEATURE [Part::Cylinder] Cylinder198  label="円柱198"
  Angle = 360
  AttacherType = Attacher::AttachEngine3D
  FirstAngle = 0
  Height = 20
  Placement = pos=(-57,71,32) rot=(0,0,1;0rad)
  Radius = 2
  SecondAngle = 0
FEATURE [Part::Cylinder] Cylinder199  label="円柱199"
  Angle = 360
  AttacherType = Attacher::AttachEngine3D
  FirstAngle = 0
  Height = 20
  Placement = pos=(-101,-27,32) rot=(0,0,1;0rad)
  Radius = 2
  SecondAngle = 0
FEATURE [Part::Cylinder] Cylinder203  label="円柱203"
  Angle = 360
  AttacherType = Attacher::AttachEngine3D
  FirstAngle = 0
  Height = 13
  Placement = pos=(33,-35,32) rot=(0,0,1;0rad)
  Radius = 2
  SecondAngle = 0
FEATURE [Part::Cylinder] Cylinder204  label="円柱204"
  Angle = 360
  AttacherType = Attacher::AttachEngine3D
  FirstAngle = 0
  Height = 13
  Placement = pos=(33,55,32) rot=(0,0,1;0rad)
  Radius = 2
  SecondAngle = 0
FEATURE [Part::Cylinder] Cylinder205  label="円柱205"
  Angle = 360
  AttacherType = Attacher::AttachEngine3D
  FirstAngle = 0
  Height = 13
  Placement = pos=(-47,55,32) rot=(0,0,1;0rad)
  Radius = 2
  SecondAngle = 0
FEATURE [Part::Cylinder] Cylinder206  label="円柱206"
  Angle = 360
  AttacherType = Attacher::AttachEngine3D
  FirstAngle = 0
  Height = 13
  Placement = pos=(-47,-35,32) rot=(0,0,1;0rad)
  Radius = 2
  SecondAngle = 0
FEATURE [Part::Cut] Cut168
  Base = -> Box259
  Tool = -> Cylinder206
FEATURE [Part::Cut] Cut169
  Base = -> Cut168
  Tool = -> Cylinder203
FEATURE [Part::Cut] Cut170
  Base = -> Cut169
  Tool = -> Cylinder205
FEATURE [Part::Cut] Cut171  label="基盤"
  Base = -> Cut170
  Placement = pos=(0,16,15) rot=(0,0,1;0rad)
  Tool = -> Cylinder204
FEATURE [Part::Cylinder] Cylinder212  label="円柱212"
  Angle = 360
  AttacherType = Attacher::AttachEngine3D
  FirstAngle = 0
  Height = 47
  Placement = pos=(7,-98,-5) rot=(0,0,1;0rad)
  Radius = 2
  SecondAngle = 0
FEATURE [Part::Cylinder] Cylinder213  label="円柱213"
  Angle = 360
  AttacherType = Attacher::AttachEngine3D
  FirstAngle = 0
  Height = 37
  Placement = pos=(15.2,-98,0) rot=(0,0,1;0rad)
  Radius = 2
  SecondAngle = 0
FEATURE [Part::Cut] Cut183
  Base = -> Box310
  Tool = -> Cylinder034
FEATURE [Part::Cut] Cut187
  Base = -> Box309
  Tool = -> Cylinder033
FEATURE [Part::Cylinder] Cylinder225  label="円柱225"
  Angle = 360
  AttacherType = Attacher::AttachEngine3D
  FirstAngle = 0
  Height = 32
  Placement = pos=(-68,82,0) rot=(0,0,1;0rad)
  Radius = 4
  SecondAngle = 0
FEATURE [Part::Cylinder] Cylinder227  label="円柱227"
  Angle = 360
  AttacherType = Attacher::AttachEngine3D
  FirstAngle = 0
  Height = 42
  Placement = pos=(-81.9,72,-5) rot=(0,0,1;0rad)
  Radius = 2
  SecondAngle = 0
FEATURE [Part::Cut] Cut191
  Base = -> Cylinder225
  Placement = pos=(-13.9,-10,0) rot=(0,0,1;0rad)
  Tool = -> Cylinder012
FEATURE [Part::Cylinder] Cylinder229  label="円柱229"
  Angle = 360
  AttacherType = Attacher::AttachEngine3D
  FirstAngle = 0
  Height = 42
  Placement = pos=(14.1,72,-5) rot=(0,0,1;0rad)
  Radius = 2
  SecondAngle = 0
FEATURE [Part::Cylinder] Cylinder230  label="円柱230"
  Angle = 360
  AttacherType = Attacher::AttachEngine3D
  FirstAngle = 0
  Height = 42
  Placement = pos=(0,82,-5) rot=(0,0,1;0rad)
  Radius = 2
  SecondAngle = 0
FEATURE [Part::Cut] Cut196
  Base = -> Cylinder007
  Placement = pos=(14.1,-10,0) rot=(0,0,1;0rad)
  Tool = -> Cylinder230
FEATURE [Part::Cylinder] Cylinder236  label="円柱236"
  Angle = 360
  AttacherType = Attacher::AttachEngine3D
  FirstAngle = 0
  Height = 42
  Placement = pos=(-85,-10,-5) rot=(0,0,1;0rad)
  Radius = 2
  SecondAngle = 0
FEATURE [Part::Cylinder] Cylinder237  label="円柱237"
  Angle = 360
  AttacherType = Attacher::AttachEngine3D
  FirstAngle = 0
  Height = 42
  Placement = pos=(17.2,-10,-5) rot=(0,0,1;0rad)
  Radius = 2
  SecondAngle = 0
FEATURE [Part::Cut] Cut202
  Base = -> Cut183
  Tool = -> Cylinder236
FEATURE [Part::Cut] Cut203
  Base = -> Cut187
  Tool = -> Cylinder237
FEATURE [Part::MultiFuse] Fusion167
  Shapes = -> [Fillet002,Cylinder127,Fillet003]
FEATURE [Part::MultiFuse] Fusion169  label="持ち手"
  Placement = pos=(0,0,20.1) rot=(0,0,1;0rad)
  Shapes = -> [Cut202,Fusion167,Cut203]
FEATURE [Part::Cylinder] Cylinder264  label="円柱264"
  Angle = 360
  AttacherType = Attacher::AttachEngine3D
  FirstAngle = 0
  Height = 12
  Placement = pos=(1.4,70,0) rot=(0,0,1;0rad)
  Radius = 2
  SecondAngle = 0
FEATURE [Part::Cylinder] Cylinder265  label="円柱265"
  Angle = 360
  AttacherType = Attacher::AttachEngine3D
  FirstAngle = 0
  Height = 12
  Placement = pos=(-70.2,70,0) rot=(0,0,1;0rad)
  Radius = 2
  SecondAngle = 0
FEATURE [Part::Box] Box016  label="機体底面"
  AttacherType = Attacher::AttachEngine3D
  Height = 5
  Length = 136
  Placement = pos=(-102,-108,-5) rot=(0,0,1;0rad)
  Width = 176
FEATURE [Part::Cylinder] Cylinder267  label="円柱267"
  Angle = 360
  AttacherType = Attacher::AttachEngine3D
  FirstAngle = 0
  Height = 26
  Placement = pos=(3,0,0) rot=(0,0,1;0rad)
  Radius = 32.5
  SecondAngle = 0
FEATURE [Part::Cylinder] Cylinder268  label="円柱268"
  Angle = 360
  AttacherType = Attacher::AttachEngine3D
  FirstAngle = 0
  Height = 26
  Radius = 2
  SecondAngle = 0
FEATURE [Part::Cut] Cut248  label="タイヤ"
  Base = -> Cylinder267
  Placement = pos=(47,54,10) rot=(0,1,0;1.5708rad)
  Tool = -> Cylinder268
  expr: .Placement.Base.x = 47 mm
FEATURE [Part::Cylinder] Cylinder269  label="円柱269"
  Angle = 360
  AttacherType = Attacher::AttachEngine3D
  FirstAngle = 0
  Height = 26
  Placement = pos=(3,0,0) rot=(0,0,1;0rad)
  Radius = 32.5
  SecondAngle = 0
FEATURE [Part::Cylinder] Cylinder270  label="円柱270"
  Angle = 360
  AttacherType = Attacher::AttachEngine3D
  FirstAngle = 0
  Height = 26
  Radius = 2
  SecondAngle = 0
FEATURE [Part::Cut] Cut249  label="タイヤ001"
  Base = -> Cylinder269
  Placement = pos=(47,-74,10) rot=(0,1,0;1.5708rad)
  Tool = -> Cylinder270
  expr: .Placement.Base.x = 47 mm
FEATURE [Part::Box] Box211  label="2"
  AttacherType = Attacher::AttachEngine3D
  Height = 5
  Length = 136
  Placement = pos=(-102,-66.1,26) rot=(0,0,1;0rad)
  Width = 91
FEATURE [Part::MultiFuse] Fusion193
  Shapes = -> [Cylinder064,Cylinder065,Cylinder066,Cylinder067]
FEATURE [Part::Cut] Cut251
  Base = -> Box260
  Placement = pos=(-4,0,12) rot=(0,0,1;0rad)
  Tool = -> Fusion193
FEATURE [Part::Box] Box295  label="立方体267"
  AttacherType = Attacher::AttachEngine3D
  Height = 3
  Length = 81
  Placement = pos=(-133,66,49) rot=(0,0,1;0rad)
  Width = 10
FEATURE [Part::Box] Box293  label="立方体265"
  AttacherType = Attacher::AttachEngine3D
  Height = 3
  Length = 54
  Placement = pos=(-106,-32,49) rot=(0,0,1;0rad)
  Width = 10
FEATURE [Part::Box] Box365  label="立方体336"
  AttacherType = Attacher::AttachEngine3D
  Height = 13
  Length = 3
  Placement = pos=(-133,66,49) rot=(0,0,1;0rad)
  Width = 10
FEATURE [Part::Box] Box366  label="立方体337"
  AttacherType = Attacher::AttachEngine3D
  Height = 3
  Length = 25
  Placement = pos=(-133,41,49) rot=(0,0,1;0rad)
  Width = 25
FEATURE [Part::Chamfer] Chamfer024
  Base = -> Box366
  EdgeLinks = -> Box366 [Edge1]
  Edges = 1 edges r=24.99: [Edge1]
FEATURE [Part::MultiFuse] Fusion194
  Shapes = -> [Cut251,Box295,Chamfer024,Box293]
FEATURE [Part::MultiFuse] Fusion195
  Shapes = -> [Fusion194,Box365]
FEATURE [Part::MultiFuse] Fusion196
  Shapes = -> [Cylinder198,Cylinder197,Cylinder199,Cylinder196]
FEATURE [Part::Cut] Cut252
  Base = -> Fusion195
  Tool = -> Fusion196
FEATURE [Part::MultiFuse] Fusion197  label=" Coral"
  Shapes = -> [Box297,Box325]
FEATURE [Part::MultiFuse] Fusion211
  Placement = pos=(-8.5,9.5,144) rot=(1,0,0;1.5708rad)
  Shapes = -> [Box100,Box101]
FEATURE [Part::Box] Box381  label="立方体351"
  AttacherType = Attacher::AttachEngine3D
  Height = 25
  Length = 15
  Placement = pos=(-41.9,-108,30) rot=(0,0,1;0rad)
  Width = 15
FEATURE [Part::Box] Box382  label="立方体352"
  AttacherType = Attacher::AttachEngine3D
  Height = 25
  Length = 25
  Placement = pos=(-46.9,-94,30) rot=(0,0,1;0rad)
  Width = 1
FEATURE [Part::MultiFuse] Fusion221
  Placement = pos=(0,-5,-8) rot=(0,0,1;0rad)
  Shapes = -> [Box381,Box382]
FEATURE [Part::MultiFuse] Fusion223
  Shapes = -> [Box024,Box026]
FEATURE [Part::Cut] Cut268
  Base = -> Fusion223
  Placement = pos=(-9,0,10) rot=(0,0,1;0rad)
  Tool = -> Box025
FEATURE [Part::Box] Box384  label="立方体354"
  AttacherType = Attacher::AttachEngine3D
  Height = 2
  Length = 2
  Placement = pos=(-47,-93,26) rot=(0,0,1;0rad)
  Width = 5
FEATURE [Part::Box] Box385  label="立方体355"
  AttacherType = Attacher::AttachEngine3D
  Height = 2
  Length = 2
  Placement = pos=(-24,-93,26) rot=(0,0,1;0rad)
  Width = 5
FEATURE [Part::MultiFuse] Fusion224
  Placement = pos=(0,-5,-4) rot=(0,0,1;0rad)
  Shapes = -> [Box384,Box385,Cut268]
FEATURE [Part::Box] Box386  label="立方体356"
  AttacherType = Attacher::AttachEngine3D
  Height = 31
  Length = 41
  Placement = pos=(-55,-108,19) rot=(0,0,1;0rad)
  Width = 10
FEATURE [Part::Box] Box397  label="立方体367"
  AttacherType = Attacher::AttachEngine3D
  Height = 20
  Length = 33
  Placement = pos=(-42,59,37) rot=(0,0,1;0rad)
  Width = 4
FEATURE [Part::Box] Box400  label="立方体370"
  AttacherType = Attacher::AttachEngine3D
  Height = 5
  Length = 33
  Placement = pos=(-42,59,37) rot=(0,0,1;0rad)
  Width = 22
FEATURE [Part::Cylinder] Cylinder290  label="円柱290"
  Angle = 360
  AttacherType = Attacher::AttachEngine3D
  FirstAngle = 0
  Height = 10
  Placement = pos=(-36,72,32) rot=(0,0,1;0rad)
  Radius = 2
  SecondAngle = 0
FEATURE [Part::Cylinder] Cylinder291  label="円柱291"
  Angle = 360
  AttacherType = Attacher::AttachEngine3D
  FirstAngle = 0
  Height = 10
  Placement = pos=(-15,72,32) rot=(0,0,1;0rad)
  Radius = 2
  SecondAngle = 0
FEATURE [Part::MultiFuse] Fusion229
  Shapes = -> [Cylinder290,Cylinder291]
FEATURE [Part::Cut] Cut277
  Base = -> Box400
  Tool = -> Fusion229
FEATURE [Part::MultiFuse] Fusion231  label="リポバッテリー蓋"
  Shapes = -> [Box397,Cut277]
FEATURE [Part::Cylinder] Cylinder294  label="円柱294"
  Angle = 360
  AttacherType = Attacher::AttachEngine3D
  FirstAngle = 0
  Height = 20
  Placement = pos=(-53,-88,43) rot=(1,0,0;1.5708rad)
  Radius = 2
  SecondAngle = 0
FEATURE [Part::Cylinder] Cylinder295  label="円柱295"
  Angle = 360
  AttacherType = Attacher::AttachEngine3D
  FirstAngle = 0
  Height = 20
  Placement = pos=(-16,-88,43) rot=(1,0,0;1.5708rad)
  Radius = 2
  SecondAngle = 0
FEATURE [Part::MultiFuse] Fusion233
  Shapes = -> [Cylinder294,Cylinder295]
FEATURE [Part::Cut] Cut280  label="レスキューカメラ蓋"
  Base = -> Fusion224
  Tool = -> Fusion233
FEATURE [Part::Box] Box403  label="立方体373"
  AttacherType = Attacher::AttachEngine3D
  Height = 25
  Length = 40
  Placement = pos=(-54.5,-108,22) rot=(0,0,1;0rad)
  Width = 6
FEATURE [Part::MultiFuse] Fusion246
  Placement = pos=(0,2,4) rot=(0,0,1;0rad)
  Shapes = -> [Cylinder181,Cylinder182]
FEATURE [Part::MultiFuse] Fusion247
  Placement = pos=(0,2,4) rot=(0,0,1;0rad)
  Shapes = -> [Cylinder179,Cylinder180]
FEATURE [Part::Box] Box408  label="立方体378"
  AttacherType = Attacher::AttachEngine3D
  Height = 20.1
  Length = 20
  Placement = pos=(-64.3,-58.9,62) rot=(0,0,1;0rad)
  Width = 9
FEATURE [Part::Box] Box409  label="立方体379"
  AttacherType = Attacher::AttachEngine3D
  Height = 16
  Length = 6
  Placement = pos=(-67,-66,46.1) rot=(0,0,1;0rad)
  Width = 10
FEATURE [Part::Box] Box411  label="立方体381"
  AttacherType = Attacher::AttachEngine3D
  Height = 16
  Length = 6
  Placement = pos=(-7,-66,46.1) rot=(0,0,1;0rad)
  Width = 10
FEATURE [Part::MultiFuse] Fusion252
  Shapes = -> [Fusion246,Fusion247]
FEATURE [Part::FeaturePython] Tube008  # WARN: FeaturePython — macro-defined, semantics opaque (R4)
  AttacherType = Attacher::AttachEngine3D
  Height = 40
  InnerRadius = 30
  OuterRadius = 33
  Placement = pos=(-34,-160,5) rot=(0,0,1;0rad)
FEATURE [Part::Cut] Cut052
  Base = -> Sphere
  Tool = -> Sphere001
FEATURE [Part::Box] Box418  label="立方体388"
  AttacherType = Attacher::AttachEngine3D
  Height = 67
  Length = 15
  Placement = pos=(-31.3,-161,15) rot=(0,0,1;0rad)
  Width = 49
FEATURE [Part::Cylinder] Cylinder302  label="円柱302"
  Angle = 360
  AttacherType = Attacher::AttachEngine3D
  FirstAngle = 0
  Height = 50
  Placement = pos=(-31.3,-131,58) rot=(0.57735,0.57735,0.57735;2.0944rad)
  Radius = 12
  SecondAngle = 0
FEATURE [Part::FeaturePython] CycloidGear016  # WARN: FeaturePython — macro-defined, semantics opaque (R4)
  AttacherType = Attacher::AttachEngine3D
  Placement = pos=(-32.8,-89,72) rot=(0,1,0;1.5708rad)
  angular_backlash = 0
  backlash = 0
  clearance = 0.25
  double_helix = false
  head = 0
  head_fillet = 0
  height = 5.5
  helix_angle = 0
  inner_diameter = 12.5
  module = 0.24
  num_teeth = 25
  numpoints = 20
  outer_diameter = 7.5
  pitch_diameter = 6
  root_fillet = 0
  version = 1.3.0
  expr: angular_backlash = backlash / pitch_diameter * 360 ° / pi
  expr: inner_diameter = num_teeth / 2
  expr: pitch_diameter = num_teeth * module
FEATURE [Part::Cylinder] Cylinder303  label="円柱303"
  Angle = 360
  AttacherType = Attacher::AttachEngine3D
  FirstAngle = 0
  Height = 15
  Placement = pos=(-31.3,-89,72) rot=(0.57735,0.57735,0.57735;2.0944rad)
  Radius = 1.5
  SecondAngle = 0
FEATURE [Part::Box] Box419  label="立方体389"
  AttacherType = Attacher::AttachEngine3D
  Height = 3
  Length = 13
  Placement = pos=(-133,66,62) rot=(0,0,1;0rad)
  Width = 10
FEATURE [Part::MultiFuse] Fusion262  label="ラズパイ固定関節材"
  Shapes = -> [Cut252,Box419]
FEATURE [Part::Box] Box422  label="立方体392"
  AttacherType = Attacher::AttachEngine3D
  Height = 4
  Length = 81.6
  Placement = pos=(-75.2,65,0) rot=(0,0,1;0rad)
  Width = 10
FEATURE [Part::Box] Box423  label="立方体393"
  AttacherType = Attacher::AttachEngine3D
  Height = 12
  Length = 25
  Placement = pos=(-75.2,65,0) rot=(0,0,1;0rad)
  Width = 10
FEATURE [Part::Box] Box424  label="立方体394"
  AttacherType = Attacher::AttachEngine3D
  Height = 12
  Length = 25
  Placement = pos=(-18.6,65,0) rot=(0,0,1;0rad)
  Width = 10
FEATURE [Part::Box] Box425  label="立方体395"
  AttacherType = Attacher::AttachEngine3D
  Height = 12
  Length = 10
  Placement = pos=(-60.2,54.6,0) rot=(0,0,1;0rad)
  Width = 20.4
FEATURE [Part::Box] Box426  label="立方体396"
  AttacherType = Attacher::AttachEngine3D
  Height = 12
  Length = 10
  Placement = pos=(-18.6,54.6,0) rot=(0,0,1;0rad)
  Width = 20.4
FEATURE [Part::MultiFuse] Fusion269
  Shapes = -> [Box422,Box423,Box424,Box425,Box426]
FEATURE [Part::Fillet] Fillet010
  Base = -> Fusion269
  EdgeLinks = -> Fusion269 [Edge8,Edge10]
  Edges = 2 edges r=4.99: [Edge8,Edge10]
FEATURE [Part::Fillet] Fillet011
  Base = -> Fillet010
  EdgeLinks = -> Fillet010 [Edge88,Edge90]
  Edges = 2 edges r=4.99: [Edge88,Edge90]
FEATURE [Part::Fillet] Fillet012
  Base = -> Fillet011
  EdgeLinks = -> Fillet011 [Edge38,Edge55,Edge73,Edge90]
  Edges = 4 edges r=3: [Edge38,Edge55,Edge73,Edge90]
FEATURE [Part::Fillet] Fillet013
  Base = -> Fillet012
  EdgeLinks = -> Fillet012 [Edge28,Edge48]
  Edges = 2 edges r=2: [Edge28,Edge48]
FEATURE [Part::MultiFuse] Fusion270
  Shapes = -> [Cylinder265,Cylinder264]
FEATURE [Part::Cut] Cut295  label="バッテリー固定材"
  Base = -> Fillet013
  Tool = -> Fusion270
FEATURE [Part::MultiFuse] Fusion273
  Placement = pos=(0,-5,0) rot=(0,0,1;0rad)
  Shapes = -> [Cylinder227,Cylinder229]
FEATURE [Part::Cylinder] Cylinder308  label="円柱308"
  Angle = 360
  AttacherType = Attacher::AttachEngine3D
  FirstAngle = 0
  Height = 42
  Placement = pos=(-81.9,72,-5) rot=(0,0,1;0rad)
  Radius = 2
  SecondAngle = 0
FEATURE [Part::Cylinder] Cylinder309  label="円柱309"
  Angle = 360
  AttacherType = Attacher::AttachEngine3D
  FirstAngle = 0
  Height = 42
  Placement = pos=(14.1,72,-5) rot=(0,0,1;0rad)
  Radius = 2
  SecondAngle = 0
FEATURE [Part::MultiFuse] Fusion275
  Placement = pos=(0,-5,0) rot=(0,0,1;0rad)
  Shapes = -> [Cylinder308,Cylinder309]
FEATURE [Part::Cylinder] Cylinder311  label="円柱311"
  Angle = 360
  AttacherType = Attacher::AttachEngine3D
  FirstAngle = 0
  Height = 47
  Placement = pos=(-75,-98,-5) rot=(0,0,1;0rad)
  Radius = 2
  SecondAngle = 0
FEATURE [Part::MultiFuse] Fusion283
  Shapes = -> [Cylinder084,Sphere003]
FEATURE [Part::Fillet] Fillet014
  Base = -> Box418
  EdgeLinks = -> Box418 [Edge10]
  Edges = 1 edges r=48.99: [Edge10]
  Placement = pos=(4.7,0,0) rot=(0,0,1;0rad)
FEATURE [Part::Box] Box429  label="立方体399"
  AttacherType = Attacher::AttachEngine3D
  Height = 35
  Length = 12.1
  Placement = pos=(-1,-120,-20) rot=(0,0,1;0rad)
  Width = 14
FEATURE [Part::MultiFuse] Fusion117
  Shapes = -> [Cut052,Tube008,Chamfer016]
FEATURE [Part::Cut] Cut054
  Base = -> Fusion117
  Tool = -> Cylinder073
FEATURE [Part::Cut] Cut055
  Base = -> Cut054
  Placement = pos=(0,15,-20) rot=(0,0,1;0rad)
  Tool = -> Cylinder074
FEATURE [Part::Cut] Cut301
  Base = -> Cut057
  Placement = pos=(0,-6,5) rot=(0,0,1;0rad)
  Tool = -> Box429
FEATURE [Part::MultiFuse] Fusion284
  Placement = pos=(0,0,-2) rot=(0,0,1;0rad)
  Shapes = -> [Cut055,Cut301]
FEATURE [Part::MultiFuse] Fusion288
  Shapes = -> [Cylinder303,CycloidGear016]
FEATURE [Part::Cylinder] Cylinder  label="円柱"
  Angle = 360
  AttacherType = Attacher::AttachEngine3D
  FirstAngle = 0
  Height = 50
  Radius = 1
  SecondAngle = 0
FEATURE [Part::Cylinder] Cylinder318  label="円柱318"
  Angle = 360
  AttacherType = Attacher::AttachEngine3D
  FirstAngle = 0
  Height = 50
  Placement = pos=(0,-27.7,0) rot=(0,0,1;0rad)
  Radius = 1
  SecondAngle = 0
FEATURE [Part::MultiFuse] Fusion290
  Placement = pos=(4.1,-87,13.1) rot=(1,0,0;1.5708rad)
  Shapes = -> [Cylinder,Cylinder318]
FEATURE [Part::MultiFuse] Fusion291
  Shapes = -> [Cylinder083,Box289]
FEATURE [Part::Cut] Cut310
  Base = -> Fusion291
  Placement = pos=(4.7,0,0) rot=(0,0,1;0rad)
  Tool = -> Fusion288
FEATURE [Part::Sphere] Sphere004  label="球体004"
  Angle1 = -90
  Angle2 = 90
  Angle3 = 360
  AttacherType = Attacher::AttachEngine3D
  Placement = pos=(-16,-108,43) rot=(0,0,1;0rad)
  Radius = 10
FEATURE [Part::Box] Box431  label="立方体401"
  AttacherType = Attacher::AttachEngine3D
  Height = 35
  Length = 45.1
  Placement = pos=(-34,-146,-17) rot=(0,0,1;0rad)
  Width = 25
FEATURE [Part::Box] Box432  label="立方体402"
  AttacherType = Attacher::AttachEngine3D
  Height = 32.3
  Length = 12.1
  Placement = pos=(0,8.5,-4.9) rot=(0,0,1;0rad)
  Width = 2.5
FEATURE [Part::Box] Box433  label="立方体403"
  AttacherType = Attacher::AttachEngine3D
  Height = 22.5
  Length = 12.1
  Width = 26.7
FEATURE [Part::Box] Box434  label="立方体404"
  AttacherType = Attacher::AttachEngine3D
  Height = 35
  Length = 12.1
  Placement = pos=(-1,-120,-20) rot=(0,0,1;0rad)
  Width = 14
FEATURE [Part::Cone] Cone002  label="円錐002"
  Angle = 360
  AttacherType = Attacher::AttachEngine3D
  Height = 5
  Radius1 = 38
  Radius2 = 33
FEATURE [Part::Cone] Cone003  label="円錐003"
  Angle = 360
  AttacherType = Attacher::AttachEngine3D
  Height = 5
  Radius1 = 33
  Radius2 = 30
FEATURE [Part::Cut] Cut314
  Base = -> Cone002
  Placement = pos=(-34,-160,0) rot=(0,0,1;0rad)
  Tool = -> Cone003
FEATURE [Part::Chamfer] Chamfer034
  Base = -> Cut314
  EdgeLinks = -> Cut314 [Edge3]
  Edges = 1 edges r=2: [Edge3]
FEATURE [Part::Cylinder] Cylinder319  label="円柱319"
  Angle = 360
  AttacherType = Attacher::AttachEngine3D
  FirstAngle = 0
  Height = 20
  Placement = pos=(-60,-160,-3) rot=(0,-1,0;0.785398rad)
  Radius = 1
  SecondAngle = 0
FEATURE [Part::Cylinder] Cylinder320  label="円柱320"
  Angle = 360
  AttacherType = Attacher::AttachEngine3D
  FirstAngle = 0
  Height = 20
  Placement = pos=(-8,-160,-3) rot=(0,1,0;0.785398rad)
  Radius = 1
  SecondAngle = 0
FEATURE [Part::Cylinder] Cylinder321  label="円柱321"
  Angle = 360
  AttacherType = Attacher::AttachEngine3D
  FirstAngle = 0
  Height = 50
  Placement = pos=(-34,-160,-17) rot=(0,0,1;0rad)
  Radius = 33
  SecondAngle = 0
FEATURE [Part::Cylinder] Cylinder322  label="円柱322"
  Angle = 360
  AttacherType = Attacher::AttachEngine3D
  FirstAngle = 0
  Height = 3
  Placement = pos=(6.05,0,16.4) rot=(1,0,0;1.5708rad)
  Radius = 2.4
  SecondAngle = 0
FEATURE [Part::MultiFuse] Fusion294
  Placement = pos=(-1,-151,-12) rot=(0,0,1;0rad)
  Shapes = -> [Cylinder322,Box432,Box433]
FEATURE [Part::Cut] Cut317
  Base = -> Box431
  Tool = -> Fusion294
FEATURE [Part::Cut] Cut318
  Base = -> Cut317
  Placement = pos=(0,15,-3) rot=(0,0,1;0rad)
  Tool = -> Cylinder321
FEATURE [Part::Cut] Cut319
  Base = -> Cut318
  Placement = pos=(0,-6,5) rot=(0,0,1;0rad)
  Tool = -> Box434
FEATURE [Part::Sphere] Sphere005  label="球体005"
  Angle1 = 0
  Angle2 = 60
  Angle3 = 360
  AttacherType = Attacher::AttachEngine3D
  Placement = pos=(-34,-160,45) rot=(0,0,1;0rad)
  Radius = 33
FEATURE [Part::Sphere] Sphere006  label="球体006"
  Angle1 = 0
  Angle2 = 60
  Angle3 = 360
  AttacherType = Attacher::AttachEngine3D
  Placement = pos=(-34,-160,45) rot=(0,0,1;0rad)
  Radius = 30
FEATURE [Part::Cut] Cut313
  Base = -> Sphere005
  Tool = -> Sphere006
FEATURE [Part::FeaturePython] Tube019  # WARN: FeaturePython — macro-defined, semantics opaque (R4)
  AttacherType = Attacher::AttachEngine3D
  Height = 40
  InnerRadius = 30
  OuterRadius = 33
  Placement = pos=(-34,-160,5) rot=(0,0,1;0rad)
FEATURE [Part::MultiFuse] Fusion293
  Shapes = -> [Cut313,Tube019,Chamfer034]
FEATURE [Part::Cut] Cut315
  Base = -> Fusion293
  Tool = -> Cylinder319
FEATURE [Part::Cut] Cut316
  Base = -> Cut315
  Placement = pos=(0,15,-20) rot=(0,0,1;0rad)
  Tool = -> Cylinder320
FEATURE [Part::MultiFuse] Fusion295
  Placement = pos=(0,0,-2) rot=(0,0,1;0rad)
  Shapes = -> [Cut316,Cut319]
FEATURE [Part::Cut] Cut320
  Base = -> Cylinder302
  Tool = -> Fusion295
FEATURE [Part::MultiFuse] Fusion296
  Shapes = -> [Cut320,Sphere004]
FEATURE [Part::Cylinder] Cylinder327  label="円柱327"
  Angle = 360
  AttacherType = Attacher::AttachEngine3D
  FirstAngle = 0
  Height = 47
  Placement = pos=(7,-98,-5) rot=(0,0,1;0rad)
  Radius = 2
  SecondAngle = 0
FEATURE [Part::Cylinder] Cylinder328  label="円柱328"
  Angle = 360
  AttacherType = Attacher::AttachEngine3D
  FirstAngle = 0
  Height = 47
  Placement = pos=(-75,-98,-5) rot=(0,0,1;0rad)
  Radius = 2
  SecondAngle = 0
FEATURE [Part::MultiFuse] Fusion316
  Refine = true
  Shapes = -> [Cylinder327,Cylinder328]
FEATURE [Part::Cylinder] Cylinder329  label="円柱329"
  Angle = 360
  AttacherType = Attacher::AttachEngine3D
  FirstAngle = 0
  Height = 47
  Placement = pos=(7,-98,-5) rot=(0,0,1;0rad)
  Radius = 2
  SecondAngle = 0
FEATURE [Part::Cylinder] Cylinder330  label="円柱330"
  Angle = 360
  AttacherType = Attacher::AttachEngine3D
  FirstAngle = 0
  Height = 47
  Placement = pos=(-75,-98,-5) rot=(0,0,1;0rad)
  Radius = 2
  SecondAngle = 0
FEATURE [Part::MultiFuse] Fusion317
  Placement = pos=(0,41,0) rot=(0,0,1;0rad)
  Refine = true
  Shapes = -> [Cylinder329,Cylinder330]
FEATURE [Part::Cut] Cut177
  Base = -> Cylinder011
  Placement = pos=(-8.2,0,0) rot=(0,0,1;0rad)
  Tool = -> Cylinder213
FEATURE [Part::MultiFuse] Fusion319
  Placement = pos=(0,-5,0) rot=(0,0,1;0rad)
  Refine = true
  Shapes = -> [Cut191,Cut196]
FEATURE [Part::MultiFuse] Fusion328
  Refine = true
  Shapes = -> [Fusion316,Fusion317,Fusion275]
FEATURE [Part::Cut] Cut341
  Base = -> Fillet014
  Refine = true
  Tool = -> Fusion283
FEATURE [Part::Cut] Cut342
  Base = -> Cut341
  Refine = true
  Tool = -> Fusion296
FEATURE [Part::Cut] Cut343
  Base = -> Fusion284
  Refine = true
  Tool = -> Fusion290
FEATURE [Part::MultiFuse] Fusion334
  Refine = true
  Shapes = -> [Cut343,Cut342,Cut310]
FEATURE [Part::Box] Box440  label="立方体410"
  AttacherType = Attacher::AttachEngine3D
  Height = 5
  Length = 16
  Placement = pos=(-82.9,-64.9,37) rot=(0,0,1;0rad)
  Width = 15
FEATURE [Part::Box] Box442  label="立方体412"
  AttacherType = Attacher::AttachEngine3D
  Height = 5
  Length = 16
  Placement = pos=(-0.9,-64.9,37) rot=(0,0,1;0rad)
  Width = 15
FEATURE [Part::Box] Box447  label="立方体417"
  AttacherType = Attacher::AttachEngine3D
  Height = 35
  Length = 45.1
  Placement = pos=(-34,-146,-17) rot=(0,0,1;0rad)
  Width = 25
FEATURE [Part::Box] Box448  label="立方体418"
  AttacherType = Attacher::AttachEngine3D
  Height = 32.7
  Length = 12.1
  Placement = pos=(0,8.5,-4.9) rot=(0,0,1;0rad)
  Width = 2.5
FEATURE [Part::Box] Box449  label="立方体419"
  AttacherType = Attacher::AttachEngine3D
  Height = 22.7
  Length = 12.1
  Width = 26.7
FEATURE [Part::Box] Box450  label="立方体420"
  AttacherType = Attacher::AttachEngine3D
  Height = 35
  Length = 12.1
  Placement = pos=(-1,-135,-17) rot=(0,0,1;0rad)
  Width = 14
FEATURE [Part::Cone] Cone004  label="円錐004"
  Angle = 360
  AttacherType = Attacher::AttachEngine3D
  Height = 7
  Radius1 = 38
  Radius2 = 29
FEATURE [Part::Cone] Cone005  label="円錐005"
  Angle = 360
  AttacherType = Attacher::AttachEngine3D
  Height = 7
  Radius1 = 33
  Radius2 = 26
FEATURE [Part::Cut] Cut355
  Base = -> Cone004
  Placement = pos=(-34,-145,-22) rot=(0,0,1;0rad)
  Tool = -> Cone005
FEATURE [Part::Cylinder] Cylinder337  label="円柱337"
  Angle = 360
  AttacherType = Attacher::AttachEngine3D
  FirstAngle = 0
  Height = 50
  Radius = 1.05
  SecondAngle = 0
FEATURE [Part::Cylinder] Cylinder338  label="円柱338"
  Angle = 360
  AttacherType = Attacher::AttachEngine3D
  FirstAngle = 0
  Height = 20
  Placement = pos=(-57,-145,-26) rot=(0,-1,0;0.785398rad)
  Radius = 1.5
  SecondAngle = 0
FEATURE [Part::Cylinder] Cylinder339  label="円柱339"
  Angle = 360
  AttacherType = Attacher::AttachEngine3D
  FirstAngle = 0
  Height = 20
  Placement = pos=(-11,-145,-26) rot=(0,1,0;0.785398rad)
  Radius = 1
  SecondAngle = 0
FEATURE [Part::Cylinder] Cylinder340  label="円柱340"
  Angle = 360
  AttacherType = Attacher::AttachEngine3D
  FirstAngle = 0
  Height = 3
  Placement = pos=(6.05,0,16.4) rot=(1,0,0;1.5708rad)
  Radius = 2.4
  SecondAngle = 0
FEATURE [Part::Cylinder] Cylinder341  label="円柱341"
  Angle = 360
  AttacherType = Attacher::AttachEngine3D
  FirstAngle = 0
  Height = 50
  Placement = pos=(0,-27.7,0) rot=(0,0,1;0rad)
  Radius = 1.05
  SecondAngle = 0
FEATURE [Part::Cylinder] Cylinder342  label="円柱342"
  Angle = 360
  AttacherType = Attacher::AttachEngine3D
  FirstAngle = 0
  Height = 40
  Placement = pos=(-34,-145,-15) rot=(0,0,1;0rad)
  Radius = 29
  SecondAngle = 0
FEATURE [Part::Cylinder] Cylinder343  label="円柱343"
  Angle = 360
  AttacherType = Attacher::AttachEngine3D
  FirstAngle = 0
  Height = 40
  Placement = pos=(-34,-145,-27) rot=(0,0,1;0rad)
  Radius = 26
  SecondAngle = 0
FEATURE [Part::Cylinder] Cylinder344  label="円柱344"
  Angle = 90
  AttacherType = Attacher::AttachEngine3D
  FirstAngle = 0
  Height = 40
  Radius = 29
  SecondAngle = 0
FEATURE [Part::Cylinder] Cylinder345  label="円柱345"
  Angle = 90
  AttacherType = Attacher::AttachEngine3D
  FirstAngle = 0
  Height = 40
  Radius = 35
  SecondAngle = 0
FEATURE [Part::Cut] Cut329
  Base = -> Cylinder345
  Placement = pos=(-34,-145,-17) rot=(0,0,1;0rad)
  Tool = -> Cylinder344
FEATURE [Part::MultiFuse] Fusion347
  Placement = pos=(-1,-151,-12) rot=(0,0,1;0rad)
  Shapes = -> [Cylinder340,Box448,Box449]
FEATURE [Part::MultiFuse] Fusion348
  Placement = pos=(4.1,-111,13.1) rot=(1,0,0;1.5708rad)
  Shapes = -> [Cylinder337,Cylinder341]
FEATURE [Part::MultiFuse] Fusion303
  Placement = pos=(92.57,-66.51,0) rot=(0,0,-1;0.785398rad)
  Shapes = -> [Cylinder339,Cylinder338]
FEATURE [Part::MultiFuse] Fusion350
  Placement = pos=(-30.8902,3.9004,0) rot=(0,0,1;0.20944rad)
  Refine = true
  Shapes = -> [Fusion303]
FEATURE [Part::Sphere] Sphere007  label="球体007"
  Angle1 = 0
  Angle2 = 60
  Angle3 = 360
  AttacherType = Attacher::AttachEngine3D
  Placement = pos=(-34,-145,25) rot=(0,0,1;0rad)
  Radius = 29
FEATURE [Part::Sphere] Sphere008  label="球体008"
  Angle1 = 0
  Angle2 = 60
  Angle3 = 360
  AttacherType = Attacher::AttachEngine3D
  Placement = pos=(-34,-145,13) rot=(0,0,1;0rad)
  Radius = 26
FEATURE [Part::MultiFuse] Fusion349
  Placement = pos=(0,0,12) rot=(0,0,1;0rad)
  Shapes = -> [Cylinder343,Sphere008]
FEATURE [Part::Sphere] Sphere010  label="球体010"
  Angle1 = -90
  Angle2 = 90
  Angle3 = 360
  AttacherType = Attacher::AttachEngine3D
  Placement = pos=(-34,-119,-36) rot=(0,0,1;0rad)
  Radius = 30
FEATURE [Part::Box] Box451  label="立方体421"
  AttacherType = Attacher::AttachEngine3D
  Height = 67
  Length = 15
  Placement = pos=(-24.3,-155,15) rot=(0,0,1;0rad)
  Width = 39
FEATURE [Part::Chamfer] Chamfer040
  Base = -> Box451
  EdgeLinks = -> Box451 [Edge10]
  Edges = 1 edges r=30: [Edge10]
FEATURE [Part::Cylinder] Cylinder346  label="円柱346"
  Angle = 360
  AttacherType = Attacher::AttachEngine3D
  FirstAngle = 0
  Height = 50
  Placement = pos=(-36,-132,56) rot=(0.57735,0.57735,0.57735;2.0944rad)
  Radius = 7
  SecondAngle = 0
FEATURE [Part::Cylinder] Cylinder347  label="円柱347"
  Angle = 360
  AttacherType = Attacher::AttachEngine3D
  FirstAngle = 0
  Height = 40
  Placement = pos=(-34,-145,-27) rot=(0,0,1;0rad)
  Radius = 26
  SecondAngle = 0
FEATURE [Part::Cylinder] Cylinder348  label="円柱348"
  Angle = 90
  AttacherType = Attacher::AttachEngine3D
  FirstAngle = 0
  Height = 79
  Radius = 29
  SecondAngle = 0
FEATURE [Part::Cylinder] Cylinder349  label="円柱349"
  Angle = 90
  AttacherType = Attacher::AttachEngine3D
  FirstAngle = 0
  Height = 79
  Radius = 50
  SecondAngle = 0
FEATURE [Part::Cut] Cut359
  Base = -> Cylinder349
  Placement = pos=(-34,-145,-17) rot=(0,0,1;0rad)
  Tool = -> Cylinder348
FEATURE [Part::Sphere] Sphere009  label="球体009"
  Angle1 = 0
  Angle2 = 60
  Angle3 = 360
  AttacherType = Attacher::AttachEngine3D
  Placement = pos=(-34,-145,13) rot=(0,0,1;0rad)
  Radius = 26
FEATURE [Part::MultiFuse] Fusion302
  Placement = pos=(0,0,17) rot=(0,0,1;0rad)
  Shapes = -> [Cylinder347,Sphere009]
FEATURE [Part::Box] Box452  label="立方体422"
  AttacherType = Attacher::AttachEngine3D
  Height = 20
  Length = 15
  Placement = pos=(-26.6,-121,62) rot=(0,0,1;0rad)
  Width = 32
FEATURE [Part::Cylinder] Cylinder350  label="円柱350"
  Angle = 360
  AttacherType = Attacher::AttachEngine3D
  FirstAngle = 0
  Height = 15
  Placement = pos=(-26.6,-89,72) rot=(0.57735,0.57735,0.57735;2.0944rad)
  Radius = 10
  SecondAngle = 0
FEATURE [Part::Cylinder] Cylinder351  label="円柱351"
  Angle = 360
  AttacherType = Attacher::AttachEngine3D
  FirstAngle = 0
  Height = 25
  Placement = pos=(-31.3,-89,72) rot=(0.57735,0.57735,0.57735;2.0944rad)
  Radius = 1.6
  SecondAngle = 0
FEATURE [Part::Chamfer] Chamfer043
  Base = -> Cut355
  EdgeLinks = -> Cut355 [Edge3]
  Edges = 1 edges r=2: [Edge3]
FEATURE [Part::Chamfer] Chamfer041
  Base = -> Chamfer040
  EdgeLinks = -> Chamfer040 [Edge2,Edge6,Edge7,Edge10]
  Edges = 4 edges r=5: [Edge2,Edge6,Edge7,Edge10]
  Placement = pos=(-2.3,0,0) rot=(0,0,1;0rad)
FEATURE [Part::Box] Box453  label="立方体423"
  AttacherType = Attacher::AttachEngine3D
  Height = 13
  Length = 7
  Placement = pos=(-26.6,-113,65.5) rot=(0,0,1;0rad)
  Width = 34
FEATURE [Part::MultiFuse] Fusion358
  Shapes = -> [Chamfer043,Cylinder342,Sphere007]
FEATURE [Part::Cut] Cut372
  Base = -> Fusion358
  Tool = -> Sphere010
FEATURE [Part::Cut] Cut373
  Base = -> Cut372
  Tool = -> Fusion350
FEATURE [Part::Cut] Cut375
  Base = -> Chamfer041
  Tool = -> Cylinder346
FEATURE [Part::Cut] Cut376
  Base = -> Cut375
  Tool = -> Cut359
FEATURE [Part::Cut] Cut377
  Base = -> Cut376
  Tool = -> Fusion302
FEATURE [Part::Cut] Cut380
  Base = -> Box447
  Tool = -> Fusion347
FEATURE [Part::Cut] Cut381
  Base = -> Cut380
  Tool = -> Box450
FEATURE [Part::Cut] Cut382
  Base = -> Cut381
  Placement = pos=(-4,-10,2) rot=(0,0,1;0rad)
  Tool = -> Fusion348
FEATURE [Part::Cut] Cut383
  Base = -> Cut382
  Tool = -> Cut329
FEATURE [Part::MultiFuse] Fusion359
  Shapes = -> [Cut383,Cut373]
FEATURE [Part::Cut] Cut384
  Base = -> Fusion359
  Placement = pos=(0,0,5) rot=(0,0,1;0rad)
  Tool = -> Fusion349
FEATURE [Part::MultiFuse] Fusion360
  Placement = pos=(0,-5,0) rot=(0,0,1;0rad)
  Shapes = -> [Cut377,Cut384]
FEATURE [Part::Cut] Cut127  label="右下モーター"
  Base = -> Cut126
  Placement = pos=(4,24.9,47.1) rot=(-1,0,0;1.5708rad)
  Tool = -> Cylinder174
FEATURE [Part::Cylinder] Cylinder352  label="円柱352"
  Angle = 360
  AttacherType = Attacher::AttachEngine3D
  FirstAngle = 0
  Height = 4
  Placement = pos=(-106,-72,10.79) rot=(0,1,0;1.5708rad)
  Radius = 12.5
  SecondAngle = 0
FEATURE [Part::Cylinder] Cylinder353  label="円柱353"
  Angle = 360
  AttacherType = Attacher::AttachEngine3D
  FirstAngle = 0
  Height = 4
  Placement = pos=(-106,-88,30) rot=(0,1,0;1.5708rad)
  Radius = 12.5
  SecondAngle = 0
FEATURE [Part::Box] Box454  label="立方体424"
  AttacherType = Attacher::AttachEngine3D
  Height = 20
  Length = 20
  Placement = pos=(-102,-78,0) rot=(0,0,1;0rad)
  Width = 15
FEATURE [Part::Cylinder] Cylinder354  label="円柱354"
  Angle = 360
  AttacherType = Attacher::AttachEngine3D
  FirstAngle = 0
  Height = 30
  Placement = pos=(-116,-72,10.79) rot=(0,1,0;1.5708rad)
  Radius = 4
  SecondAngle = 0
FEATURE [Part::Cylinder] Cylinder358  label="円柱358"
  Angle = 360
  AttacherType = Attacher::AttachEngine3D
  FirstAngle = 0
  Height = 13
  Placement = pos=(-48,-69,-5) rot=(0,0,1;0rad)
  Radius = 2
  SecondAngle = 0
FEATURE [Part::Box] Box  label="立方体428"
  AttacherType = Attacher::AttachEngine3D
  Height = 85
  Length = 56
  Width = 21
FEATURE [Part::Box] Box458  label="立方体429"
  AttacherType = Attacher::AttachEngine3D
  Height = 3
  Length = 20
  Placement = pos=(18,14,-3) rot=(0,0,1;0rad)
  Width = 4
FEATURE [Part::Box] Box002  label="立方体430"
  AttacherType = Attacher::AttachEngine3D
  Height = 12
  Length = 10
  Placement = pos=(12,21,-5) rot=(0,0,1;0rad)
  Width = 10
FEATURE [Part::Box] Box003  label="立方体431"
  AttacherType = Attacher::AttachEngine3D
  Height = 78
  Length = 40
  Placement = pos=(9,21,7) rot=(0,0,1;0rad)
  Width = 19
FEATURE [Part::MultiFuse] Fusion363  label="ラズパイ"
  Placement = pos=(-63.2,17,0) rot=(0,0,1;0rad)
  Shapes = -> [Box003,Box,Box002,Box458]
FEATURE [Part::FeaturePython] Tube020  # WARN: FeaturePython — macro-defined, semantics opaque (R4)
  AttacherType = Attacher::AttachEngine3D
  Height = 26
  InnerRadius = 4
  OuterRadius = 32.5
  Placement = pos=(38,-72,10.79) rot=(0,1,0;1.5708rad)
FEATURE [Part::FeaturePython] Tube021  # WARN: FeaturePython — macro-defined, semantics opaque (R4)
  AttacherType = Attacher::AttachEngine3D
  Height = 26
  InnerRadius = 4
  OuterRadius = 32.5
  Placement = pos=(38,51,10.79) rot=(0,1,0;1.5708rad)
FEATURE [Part::Cylinder] Cylinder360  label="円柱360"
  Angle = 360
  AttacherType = Attacher::AttachEngine3D
  FirstAngle = 0
  Height = 65
  Placement = pos=(-90,-103,-10) rot=(0,0,1;0rad)
  Radius = 2
  SecondAngle = 0
FEATURE [Part::Cylinder] Cylinder361  label="円柱361"
  Angle = 360
  AttacherType = Attacher::AttachEngine3D
  FirstAngle = 0
  Height = 65
  Placement = pos=(-90,-61,-10) rot=(0,0,1;0rad)
  Radius = 2
  SecondAngle = 0
FEATURE [Part::MultiFuse] Fusion364
  Placement = pos=(-2,0,0) rot=(0,0,1;0rad)
  Shapes = -> [Cylinder361,Cylinder360]
FEATURE [Part::Cylinder] Cylinder362  label="円柱362"
  Angle = 360
  AttacherType = Attacher::AttachEngine3D
  FirstAngle = 0
  Height = 70
  Placement = pos=(-90,-103,-10) rot=(0,0,1;0rad)
  Radius = 2
  SecondAngle = 0
FEATURE [Part::Cylinder] Cylinder363  label="円柱363"
  Angle = 360
  AttacherType = Attacher::AttachEngine3D
  FirstAngle = 0
  Height = 70
  Placement = pos=(-90,-61,-10) rot=(0,0,1;0rad)
  Radius = 2
  SecondAngle = 0
FEATURE [Part::MultiFuse] Fusion365
  Placement = pos=(114,0,0) rot=(0,0,1;0rad)
  Shapes = -> [Cylinder363,Cylinder362]
FEATURE [Part::Box] Box459  label="立方体432"
  AttacherType = Attacher::AttachEngine3D
  Height = 3
  Length = 20
  Placement = pos=(14,-108,40.1) rot=(0,0,1;0rad)
  Width = 52
FEATURE [Part::Cylinder] Cylinder364  label="円柱364"
  Angle = 360
  AttacherType = Attacher::AttachEngine3D
  FirstAngle = 0
  Height = 70
  Placement = pos=(-90,-103,-10) rot=(0,0,1;0rad)
  Radius = 2
  SecondAngle = 0
FEATURE [Part::Cylinder] Cylinder365  label="円柱365"
  Angle = 360
  AttacherType = Attacher::AttachEngine3D
  FirstAngle = 0
  Height = 70
  Placement = pos=(-90,-61,-10) rot=(0,0,1;0rad)
  Radius = 2
  SecondAngle = 0
FEATURE [Part::MultiFuse] Fusion366
  Placement = pos=(114,123,0) rot=(0,0,1;0rad)
  Shapes = -> [Cylinder365,Cylinder364]
FEATURE [Part::Box] Box460  label="ripo"
  AttacherType = Attacher::AttachEngine3D
  Height = 32
  Length = 80
  Placement = pos=(-75,-76,0) rot=(0,0,1;0rad)
  Width = 15
FEATURE [Part::Box] Box461  label="立方体434"
  AttacherType = Attacher::AttachEngine3D
  Height = 3
  Length = 20
  Placement = pos=(-102,-108,40.1) rot=(0,0,1;0rad)
  Width = 52
FEATURE [Part::Box] Box462  label="立方体435"
  AttacherType = Attacher::AttachEngine3D
  Height = 5
  Length = 2.7
  Placement = pos=(22.5,-98.1,-5) rot=(0,0,1;0rad)
  Width = 20.1
FEATURE [Part::Box] Box463  label="立方体436"
  AttacherType = Attacher::AttachEngine3D
  Height = 5
  Length = 2.7
  Placement = pos=(22.5,-98.1,39) rot=(0,0,1;0rad)
  Width = 20.1
FEATURE [Part::Box] Box464  label="立方体437"
  AttacherType = Attacher::AttachEngine3D
  Height = 5
  Length = 2.7
  Placement = pos=(-93.2,-98.1,39) rot=(0,0,1;0rad)
  Width = 20.1
FEATURE [Part::Cut] Cut397
  Base = -> Box459
  Tool = -> Box463
FEATURE [Part::Box] Box465  label="立方体438"
  AttacherType = Attacher::AttachEngine3D
  Height = 5
  Length = 2.7
  Placement = pos=(-93.2,-98.1,-5) rot=(0,0,1;0rad)
  Width = 20.1
FEATURE [Part::Cut] Cut398
  Base = -> Box461
  Tool = -> Box464
FEATURE [Part::Cylinder] Cylinder366  label="円柱366"
  Angle = 360
  AttacherType = Attacher::AttachEngine3D
  FirstAngle = 0
  Height = 65
  Placement = pos=(-90,-103,-10) rot=(0,0,1;0rad)
  Radius = 2
  SecondAngle = 0
FEATURE [Part::Cylinder] Cylinder367  label="円柱367"
  Angle = 360
  AttacherType = Attacher::AttachEngine3D
  FirstAngle = 0
  Height = 65
  Placement = pos=(-90,-61,-10) rot=(0,0,1;0rad)
  Radius = 2
  SecondAngle = 0
FEATURE [Part::MultiFuse] Fusion367
  Placement = pos=(-2,123,0) rot=(0,0,1;0rad)
  Shapes = -> [Cylinder367,Cylinder366]
FEATURE [Part::Fillet] Fillet015
  Base = -> Cut398
  EdgeLinks = -> Cut398 [Edge1,Edge3,Edge6,Edge15]
  Edges = 4 edges r=8: [Edge1,Edge3,Edge6,Edge15]
FEATURE [Part::Cylinder] Cylinder368  label="円柱368"
  Angle = 360
  AttacherType = Attacher::AttachEngine3D
  FirstAngle = 0
  Height = 5
  Placement = pos=(-92,-70,39) rot=(0,0,1;0rad)
  Radius = 4
  SecondAngle = 0
FEATURE [Part::Cylinder] Cylinder369  label="円柱369"
  Angle = 360
  AttacherType = Attacher::AttachEngine3D
  FirstAngle = 0
  Height = 5
  Placement = pos=(24,-70,39) rot=(0,0,1;0rad)
  Radius = 4
  SecondAngle = 0
FEATURE [Part::Cut] Cut399
  Base = -> Fillet015
  Tool = -> Cylinder368
FEATURE [Part::Fillet] Fillet016
  Base = -> Cut397
  EdgeLinks = -> Cut397 [Edge1,Edge3,Edge6,Edge15]
  Edges = 4 edges r=8: [Edge1,Edge3,Edge6,Edge15]
FEATURE [Part::Cut] Cut400
  Base = -> Fillet016
  Tool = -> Cylinder369
FEATURE [Part::Cylinder] Cylinder370  label="円柱370"
  Angle = 360
  AttacherType = Attacher::AttachEngine3D
  FirstAngle = 0
  Height = 65
  Placement = pos=(-90,-103,-10) rot=(0,0,1;0rad)
  Radius = 2
  SecondAngle = 0
FEATURE [Part::Cylinder] Cylinder371  label="円柱371"
  Angle = 360
  AttacherType = Attacher::AttachEngine3D
  FirstAngle = 0
  Height = 65
  Placement = pos=(-90,-61,-10) rot=(0,0,1;0rad)
  Radius = 2
  SecondAngle = 0
FEATURE [Part::MultiFuse] Fusion368
  Placement = pos=(-2,0,0) rot=(0,0,1;0rad)
  Shapes = -> [Cylinder371,Cylinder370]
FEATURE [Part::Cut] Cut401
  Base = -> Cut399
  Tool = -> Fusion368
FEATURE [Part::Cylinder] Cylinder372  label="円柱372"
  Angle = 360
  AttacherType = Attacher::AttachEngine3D
  FirstAngle = 0
  Height = 70
  Placement = pos=(-90,-103,-10) rot=(0,0,1;0rad)
  Radius = 2
  SecondAngle = 0
FEATURE [Part::Cylinder] Cylinder373  label="円柱373"
  Angle = 360
  AttacherType = Attacher::AttachEngine3D
  FirstAngle = 0
  Height = 70
  Placement = pos=(-90,-61,-10) rot=(0,0,1;0rad)
  Radius = 2
  SecondAngle = 0
FEATURE [Part::MultiFuse] Fusion369
  Placement = pos=(114,0,0) rot=(0,0,1;0rad)
  Shapes = -> [Cylinder373,Cylinder372]
FEATURE [Part::Cut] Cut402
  Base = -> Cut400
  Tool = -> Fusion369
FEATURE [Part::Box] Box466  label="立方体439"
  AttacherType = Attacher::AttachEngine3D
  Height = 3
  Length = 20
  Placement = pos=(-102,-108,40.1) rot=(0,0,1;0rad)
  Width = 52
FEATURE [Part::Box] Box467  label="立方体440"
  AttacherType = Attacher::AttachEngine3D
  Height = 5
  Length = 2.7
  Placement = pos=(-93.2,-98.1,39) rot=(0,0,1;0rad)
  Width = 20.1
FEATURE [Part::Cut] Cut403
  Base = -> Box466
  Tool = -> Box467
FEATURE [Part::Cylinder] Cylinder374  label="円柱374"
  Angle = 360
  AttacherType = Attacher::AttachEngine3D
  FirstAngle = 0
  Height = 5
  Placement = pos=(-92,-70,39) rot=(0,0,1;0rad)
  Radius = 4
  SecondAngle = 0
FEATURE [Part::Cylinder] Cylinder375  label="円柱375"
  Angle = 360
  AttacherType = Attacher::AttachEngine3D
  FirstAngle = 0
  Height = 65
  Placement = pos=(-90,-103,-10) rot=(0,0,1;0rad)
  Radius = 2
  SecondAngle = 0
FEATURE [Part::Cylinder] Cylinder376  label="円柱376"
  Angle = 360
  AttacherType = Attacher::AttachEngine3D
  FirstAngle = 0
  Height = 65
  Placement = pos=(-90,-61,-10) rot=(0,0,1;0rad)
  Radius = 2
  SecondAngle = 0
FEATURE [Part::Fillet] Fillet017
  Base = -> Cut403
  EdgeLinks = -> Cut403 [Edge1,Edge3,Edge6,Edge15]
  Edges = 4 edges r=8: [Edge1,Edge3,Edge6,Edge15]
FEATURE [Part::Cut] Cut404
  Base = -> Fillet017
  Tool = -> Cylinder374
FEATURE [Part::MultiFuse] Fusion370
  Placement = pos=(-2,0,0) rot=(0,0,1;0rad)
  Shapes = -> [Cylinder376,Cylinder375]
FEATURE [Part::Cut] Cut405
  Base = -> Cut404
  Placement = pos=(0,123,0) rot=(0,0,1;0rad)
  Tool = -> Fusion370
FEATURE [Part::Box] Box468  label="立方体441"
  AttacherType = Attacher::AttachEngine3D
  Height = 3
  Length = 20
  Placement = pos=(14,-108,40.1) rot=(0,0,1;0rad)
  Width = 52
FEATURE [Part::Box] Box469  label="立方体442"
  AttacherType = Attacher::AttachEngine3D
  Height = 5
  Length = 2.7
  Placement = pos=(22.5,-98.1,39) rot=(0,0,1;0rad)
  Width = 20.1
FEATURE [Part::Cut] Cut406
  Base = -> Box468
  Tool = -> Box469
FEATURE [Part::Cylinder] Cylinder377  label="円柱377"
  Angle = 360
  AttacherType = Attacher::AttachEngine3D
  FirstAngle = 0
  Height = 5
  Placement = pos=(24,-70,39) rot=(0,0,1;0rad)
  Radius = 4
  SecondAngle = 0
FEATURE [Part::Cylinder] Cylinder378  label="円柱378"
  Angle = 360
  AttacherType = Attacher::AttachEngine3D
  FirstAngle = 0
  Height = 70
  Placement = pos=(-90,-103,-10) rot=(0,0,1;0rad)
  Radius = 2
  SecondAngle = 0
FEATURE [Part::Cylinder] Cylinder379  label="円柱379"
  Angle = 360
  AttacherType = Attacher::AttachEngine3D
  FirstAngle = 0
  Height = 70
  Placement = pos=(-90,-61,-10) rot=(0,0,1;0rad)
  Radius = 2
  SecondAngle = 0
FEATURE [Part::Fillet] Fillet018
  Base = -> Cut406
  EdgeLinks = -> Cut406 [Edge1,Edge3,Edge6,Edge15]
  Edges = 4 edges r=8: [Edge1,Edge3,Edge6,Edge15]
FEATURE [Part::Cut] Cut407
  Base = -> Fillet018
  Tool = -> Cylinder377
FEATURE [Part::MultiFuse] Fusion371
  Placement = pos=(114,0,0) rot=(0,0,1;0rad)
  Shapes = -> [Cylinder379,Cylinder378]
FEATURE [Part::Cut] Cut408
  Base = -> Cut407
  Placement = pos=(0,123,0) rot=(0,0,1;0rad)
  Tool = -> Fusion371
FEATURE [Part::Box] Box470  label="立方体443"
  AttacherType = Attacher::AttachEngine3D
  Height = 15
  Length = 136
  Placement = pos=(-102,14,0) rot=(0,0,1;0rad)
  Width = 3
FEATURE [Part::Cut] Cut410
  Base = -> Box266
  Placement = pos=(3,72.4,-50) rot=(0,0,1;0rad)
  Tool = -> Fusion112
FEATURE [Part::Cut] Cut411
  Base = -> Box268
  Placement = pos=(-4,72.4,-50) rot=(0,0,1;0rad)
  Tool = -> Fusion113
FEATURE [Part::Box] Box471  label="立方体444"
  AttacherType = Attacher::AttachEngine3D
  Height = 3
  Length = 41
  Placement = pos=(-7,-108,46.1) rot=(0,0,1;0rad)
  Width = 9.9
FEATURE [Part::MultiFuse] Fusion372
  Shapes = -> [Box283,Box408,Box281]
FEATURE [Part::Cut] Cut412
  Base = -> Fusion372
  Placement = pos=(4.7,0,0.1) rot=(0,0,1;0rad)
  Tool = -> Fusion252
FEATURE [Part::Box] Box472  label="立方体445"
  AttacherType = Attacher::AttachEngine3D
  Height = 3
  Length = 41
  Placement = pos=(-102,-108,46.1) rot=(0,0,1;0rad)
  Width = 9.9
FEATURE [Part::Box] Box473  label="立方体446"
  AttacherType = Attacher::AttachEngine3D
  Height = 3
  Length = 41
  Placement = pos=(-7,-66,46.1) rot=(0,0,1;0rad)
  Width = 10
FEATURE [Part::Chamfer] Chamfer044
  Base = -> Cut412
  EdgeLinks = -> Cut412 [Edge3,Edge20]
  Edges = 2 edges r=6.1: [Edge3,Edge20]
  Placement = pos=(-0.1,0,0) rot=(0,0,1;0rad)
FEATURE [Part::Box] Box474  label="立方体447"
  AttacherType = Attacher::AttachEngine3D
  Height = 3
  Length = 41
  Placement = pos=(-102,-66,46.1) rot=(0,0,1;0rad)
  Width = 10
FEATURE [Part::Box] Box475  label="立方体448"
  AttacherType = Attacher::AttachEngine3D
  Height = 3
  Length = 8.8
  Placement = pos=(-102,-108,46.1) rot=(0,0,1;0rad)
  Width = 52
FEATURE [Part::Box] Box476  label="立方体449"
  AttacherType = Attacher::AttachEngine3D
  Height = 3
  Length = 8.8
  Placement = pos=(25.2,-108,46.1) rot=(0,0,1;0rad)
  Width = 52
FEATURE [Part::Cylinder] Cylinder380  label="円柱380"
  Angle = 360
  AttacherType = Attacher::AttachEngine3D
  FirstAngle = 0
  Height = 65
  Placement = pos=(-90,-103,-10) rot=(0,0,1;0rad)
  Radius = 2
  SecondAngle = 0
FEATURE [Part::Cylinder] Cylinder381  label="円柱381"
  Angle = 360
  AttacherType = Attacher::AttachEngine3D
  FirstAngle = 0
  Height = 65
  Placement = pos=(-90,-61,-10) rot=(0,0,1;0rad)
  Radius = 2
  SecondAngle = 0
FEATURE [Part::MultiFuse] Fusion373
  Placement = pos=(-2,0,0) rot=(0,0,1;0rad)
  Shapes = -> [Cylinder381,Cylinder380]
FEATURE [Part::Cylinder] Cylinder382  label="円柱382"
  Angle = 360
  AttacherType = Attacher::AttachEngine3D
  FirstAngle = 0
  Height = 70
  Placement = pos=(-90,-103,-10) rot=(0,0,1;0rad)
  Radius = 2
  SecondAngle = 0
FEATURE [Part::Cylinder] Cylinder383  label="円柱383"
  Angle = 360
  AttacherType = Attacher::AttachEngine3D
  FirstAngle = 0
  Height = 70
  Placement = pos=(-90,-61,-10) rot=(0,0,1;0rad)
  Radius = 2
  SecondAngle = 0
FEATURE [Part::MultiFuse] Fusion374
  Placement = pos=(114,0,0) rot=(0,0,1;0rad)
  Shapes = -> [Cylinder383,Cylinder382]
FEATURE [Part::MultiFuse] Fusion375
  Shapes = -> [Box472,Box475,Box474]
FEATURE [Part::MultiFuse] Fusion376
  Shapes = -> [Box471,Box476,Box473]
FEATURE [Part::Cut] Cut413
  Base = -> Fusion375
  Tool = -> Fusion373
FEATURE [Part::Cut] Cut414
  Base = -> Fusion376
  Tool = -> Fusion374
FEATURE [Part::MultiFuse] Fusion377
  Shapes = -> [Box288,Box411,Box286,Box409]
FEATURE [Part::Fillet] Fillet019
  Base = -> Cut413
  EdgeLinks = -> Cut413 [Edge1,Edge32]
  Edges = 2 edges r=8: [Edge1,Edge32]
FEATURE [Part::Box] Box477  label="立方体"
  AttacherType = Attacher::AttachEngine3D
  Height = 2
  Length = 127
  Placement = pos=(-98,-56,49) rot=(0,0,1;0rad)
  Width = 71
FEATURE [Part::Fillet] Fillet021
  Base = -> Cut414
  EdgeLinks = -> Cut414 [Edge18,Edge60]
  Edges = 2 edges r=8: [Edge18,Edge60]
FEATURE [Part::MultiFuse] Fusion362
  Placement = pos=(-2.5,50,51) rot=(0,0,1;0rad)
  Shapes = -> [Cylinder192,Cylinder358]
FEATURE [Part::Box] Box478  label="立方体450"
  AttacherType = Attacher::AttachEngine3D
  Height = 4
  Length = 4
  Placement = pos=(-26,-10.5,51) rot=(0,0,1;0rad)
  Width = 4
FEATURE [Part::MultiFuse] Fusion378  label="rescue arm stand"
  Shapes = -> [Fillet019,Fillet021,Fusion377,Chamfer044]
FEATURE [Part::Cut] Cut415
  Base = -> Box016
  Tool = -> Box102
FEATURE [Part::Box] Box479  label="立方体451"
  AttacherType = Attacher::AttachEngine3D
  Height = 3
  Length = 58.4
  Placement = pos=(-63.2,38,0) rot=(0,0,1;0rad)
  Width = 19
FEATURE [Part::Cylinder] Cylinder384  label="円柱384"
  Angle = 360
  AttacherType = Attacher::AttachEngine3D
  FirstAngle = 0
  Height = 10
  Placement = pos=(-10.7,44,10.5) rot=(1,0,0;1.5708rad)
  Radius = 2
  SecondAngle = 0
FEATURE [Part::Box] Box480  label="立方体452"
  AttacherType = Attacher::AttachEngine3D
  Height = 15
  Length = 9
  Placement = pos=(-63.2,38,7) rot=(0,0,1;0rad)
  Width = 4
FEATURE [Part::Box] Box481  label="立方体453"
  AttacherType = Attacher::AttachEngine3D
  Height = 7
  Length = 34
  Placement = pos=(-51.2,38,0) rot=(0,0,1;0rad)
  Width = 10
FEATURE [Part::Box] Box482  label="立方体454"
  AttacherType = Attacher::AttachEngine3D
  Height = 67
  Length = 9.4
  Placement = pos=(-14.2,38,7) rot=(0,0,1;0rad)
  Width = 4
FEATURE [Part::Fillet] Fillet
  Base = -> Box481
  EdgeLinks = -> Box481 [Edge3,Edge7]
  Edges = 2 edges r=3: [Edge3,Edge7]
FEATURE [Part::Cut] Cut416
  Base = -> Box479
  Tool = -> Fillet
FEATURE [Part::Cylinder] Cylinder385  label="円柱385"
  Angle = 360
  AttacherType = Attacher::AttachEngine3D
  FirstAngle = 0
  Height = 10
  Placement = pos=(-10.7,44,68.5) rot=(1,0,0;1.5708rad)
  Radius = 2
  SecondAngle = 0
FEATURE [Part::Cylinder] Cylinder386  label="円柱386"
  Angle = 360
  AttacherType = Attacher::AttachEngine3D
  FirstAngle = 0
  Height = 10
  Placement = pos=(-59.7,44,10.5) rot=(1,0,0;1.5708rad)
  Radius = 2
  SecondAngle = 0
FEATURE [Part::MultiFuse] Fusion379
  Shapes = -> [Cylinder385,Cylinder384]
FEATURE [Part::Cut] Cut417
  Base = -> Box482
  Tool = -> Fusion379
FEATURE [Part::Cut] Cut418
  Base = -> Box480
  Tool = -> Cylinder386
FEATURE [Part::Fillet] Fillet024
  Base = -> Cut418
  EdgeLinks = -> Cut418 [Edge2,Edge10]
  Edges = 2 edges r=4.49: [Edge2,Edge10]
FEATURE [Part::Fillet] Fillet025
  Base = -> Cut417
  EdgeLinks = -> Cut417 [Edge2,Edge11]
  Edges = 2 edges r=4.69: [Edge2,Edge11]
FEATURE [Part::Cylinder] Cylinder387  label="円柱387"
  Angle = 360
  AttacherType = Attacher::AttachEngine3D
  FirstAngle = 0
  Height = 16
  Placement = pos=(-9.8,51,-5) rot=(0,0,1;0rad)
  Radius = 2
  SecondAngle = 0
FEATURE [Part::Cylinder] Cylinder388  label="円柱388"
  Angle = 360
  AttacherType = Attacher::AttachEngine3D
  FirstAngle = 0
  Height = 16
  Placement = pos=(-9.8,51,-5) rot=(0,0,1;0rad)
  Radius = 2
  SecondAngle = 0
FEATURE [Part::Box] Box483  label="立方体455"
  AttacherType = Attacher::AttachEngine3D
  Height = 4
  Length = 4
  Placement = pos=(-26,-23.5,51) rot=(0,0,1;0rad)
  Width = 4
FEATURE [Part::Box] Box484  label="立方体456"
  AttacherType = Attacher::AttachEngine3D
  Height = 4
  Length = 4
  Placement = pos=(-47,-10.5,51) rot=(0,0,1;0rad)
  Width = 4
FEATURE [Part::Box] Box485  label="立方体457"
  AttacherType = Attacher::AttachEngine3D
  Height = 4
  Length = 4
  Placement = pos=(-47,-23.5,51) rot=(0,0,1;0rad)
  Width = 4
FEATURE [Part::Box] Box486  label="立方体458"
  AttacherType = Attacher::AttachEngine3D
  Height = 1.5
  Length = 25
  Placement = pos=(-47,-24.5,53.5) rot=(0,0,1;0rad)
  Width = 18
FEATURE [Part::Cylinder] Cylinder389  label="円柱389"
  Angle = 360
  AttacherType = Attacher::AttachEngine3D
  FirstAngle = 0
  Height = 16
  Placement = pos=(-58.2,51,-5) rot=(0,0,1;0rad)
  Radius = 2
  SecondAngle = 0
FEATURE [Part::MultiFuse] Fusion380
  Shapes = -> [Cylinder388,Cylinder387,Cylinder389]
FEATURE [Part::Cylinder] Cylinder391  label="円柱391"
  Angle = 360
  AttacherType = Attacher::AttachEngine3D
  FirstAngle = 0
  Height = 5
  Placement = pos=(-9.8,51,-5) rot=(0,0,1;0rad)
  Radius = 4
  SecondAngle = 0
FEATURE [Part::Cylinder] Cylinder392  label="円柱392"
  Angle = 360
  AttacherType = Attacher::AttachEngine3D
  FirstAngle = 0
  Height = 5
  Placement = pos=(-58.2,51,-5) rot=(0,0,1;0rad)
  Radius = 4
  SecondAngle = 0
FEATURE [Part::Box] Box487  label="立方体459"
  AttacherType = Attacher::AttachEngine3D
  Height = 5
  Length = 34
  Placement = pos=(-51.2,38,-5) rot=(0,0,1;0rad)
  Width = 10
FEATURE [Part::Box] Box488  label="立方体460"
  AttacherType = Attacher::AttachEngine3D
  Height = 3
  Length = 20
  Placement = pos=(-45.2,31,-3) rot=(0,0,1;0rad)
  Width = 4
FEATURE [Part::Fillet] Fillet027
  Base = -> Box487
  EdgeLinks = -> Box487 [Edge3,Edge7]
  Edges = 2 edges r=3: [Edge3,Edge7]
FEATURE [Part::MultiFuse] Fusion383
  Shapes = -> [Fillet027,Box488]
FEATURE [Part::MultiFuse] Fusion384
  Shapes = -> [Cylinder391,Cylinder392]
FEATURE [Part::MultiFuse] Fusion385
  Shapes = -> [Fusion383,Fusion384]
FEATURE [Part::Cut] Cut420
  Base = -> Cut415
  Tool = -> Fusion385
FEATURE [Part::Cut] Cut419
  Base = -> Cut416
  Tool = -> Fusion380
FEATURE [Part::Fillet] Fillet026
  Base = -> Cut419
  EdgeLinks = -> Cut419 [Edge3,Edge19]
  Edges = 2 edges r=6: [Edge3,Edge19]
FEATURE [Part::Box] Box489  label="立方体461"
  AttacherType = Attacher::AttachEngine3D
  Height = 4
  Length = 58.4
  Placement = pos=(-63.2,38,3) rot=(0,0,1;0rad)
  Width = 19
FEATURE [Part::Box] Box490  label="立方体462"
  AttacherType = Attacher::AttachEngine3D
  Height = 7
  Length = 34
  Placement = pos=(-51.2,38,0) rot=(0,0,1;0rad)
  Width = 10
FEATURE [Part::Cylinder] Cylinder393  label="円柱393"
  Angle = 360
  AttacherType = Attacher::AttachEngine3D
  FirstAngle = 0
  Height = 16
  Placement = pos=(-9.8,51,-5) rot=(0,0,1;0rad)
  Radius = 2
  SecondAngle = 0
FEATURE [Part::Cylinder] Cylinder394  label="円柱394"
  Angle = 360
  AttacherType = Attacher::AttachEngine3D
  FirstAngle = 0
  Height = 16
  Placement = pos=(-9.8,51,-5) rot=(0,0,1;0rad)
  Radius = 2
  SecondAngle = 0
FEATURE [Part::Cylinder] Cylinder395  label="円柱395"
  Angle = 360
  AttacherType = Attacher::AttachEngine3D
  FirstAngle = 0
  Height = 16
  Placement = pos=(-58.2,51,-5) rot=(0,0,1;0rad)
  Radius = 2
  SecondAngle = 0
FEATURE [Part::Fillet] Fillet028
  Base = -> Box490
  EdgeLinks = -> Box490 [Edge3,Edge7]
  Edges = 2 edges r=3: [Edge3,Edge7]
FEATURE [Part::Cut] Cut421
  Base = -> Box489
  Tool = -> Fillet028
FEATURE [Part::MultiFuse] Fusion386
  Shapes = -> [Cylinder394,Cylinder393,Cylinder395]
FEATURE [Part::Cut] Cut422
  Base = -> Cut421
  Tool = -> Fusion386
FEATURE [Part::Fillet] Fillet029
  Base = -> Cut422
  EdgeLinks = -> Cut422 [Edge3,Edge19]
  Edges = 2 edges r=6: [Edge3,Edge19]
FEATURE [Part::MultiFuse] Fusion387
  Shapes = -> [Fillet026,Cut420]
FEATURE [Part::MultiFuse] Fusion388
  Shapes = -> [Fillet024,Fillet029,Fillet025]
FEATURE [Part::Box] Box491  label="立方体463"
  AttacherType = Attacher::AttachEngine3D
  Height = 20
  Length = 5
  Placement = pos=(29,-63,0) rot=(0,0,1;0rad)
  Width = 27.8
FEATURE [Part::Box] Box492  label="立方体464"
  AttacherType = Attacher::AttachEngine3D
  Height = 20
  Length = 5
  Placement = pos=(-102,-63,0) rot=(0,0,1;0rad)
  Width = 27.8
FEATURE [Part::Box] Box493  label="立方体465"
  AttacherType = Attacher::AttachEngine3D
  Height = 15
  Length = 15
  Placement = pos=(-102,17,0) rot=(0,0,1;0rad)
  Width = 7.9
FEATURE [Part::Box] Box494  label="立方体466"
  AttacherType = Attacher::AttachEngine3D
  Height = 15
  Length = 15
  Placement = pos=(-102,17,0) rot=(0,0,1;0rad)
  Width = 7.9
FEATURE [Part::Box] Box495  label="立方体467"
  AttacherType = Attacher::AttachEngine3D
  Height = 15
  Length = 15
  Placement = pos=(19,17,0) rot=(0,0,1;0rad)
  Width = 7.9
FEATURE [Part::MultiFuse] Fusion389
  Shapes = -> [Box462,Box465]
FEATURE [Part::Box] Box496  label="立方体468"
  AttacherType = Attacher::AttachEngine3D
  Height = 5
  Length = 2.7
  Placement = pos=(22.5,-98.1,-5) rot=(0,0,1;0rad)
  Width = 20.1
FEATURE [Part::Box] Box497  label="立方体469"
  AttacherType = Attacher::AttachEngine3D
  Height = 5
  Length = 2.7
  Placement = pos=(-93.2,-98.1,-5) rot=(0,0,1;0rad)
  Width = 20.1
FEATURE [Part::MultiFuse] Fusion390
  Placement = pos=(0,123,0) rot=(0,0,1;0rad)
  Shapes = -> [Box496,Box497]
FEATURE [Part::MultiFuse] Fusion391
  Shapes = -> [Fusion389,Fusion390]
FEATURE [Part::Cut] Cut423
  Base = -> Fusion387
  Tool = -> Fusion391
FEATURE [Part::Box] Box498  label="立方体470"
  AttacherType = Attacher::AttachEngine3D
  Height = 5
  Length = 12
  Placement = pos=(-98,-66,35) rot=(0,0,1;0rad)
  Width = 90.9
FEATURE [Part::Box] Box499  label="立方体471"
  AttacherType = Attacher::AttachEngine3D
  Height = 5
  Length = 12
  Placement = pos=(18,-66,35) rot=(0,0,1;0rad)
  Width = 90.9
FEATURE [Part::Box] Box500  label="立方体472"
  AttacherType = Attacher::AttachEngine3D
  Height = 4
  Length = 41
  Placement = pos=(-55,-34.5,47) rot=(0,0,1;0rad)
  Width = 31
FEATURE [Part::Box] Box501  label="立方体473"
  AttacherType = Attacher::AttachEngine3D
  Height = 3
  Length = 128
  Placement = pos=(-98,-27,48) rot=(0,0,1;0rad)
  Width = 15
FEATURE [Part::Box] Box502  label="立方体474"
  AttacherType = Attacher::AttachEngine3D
  Height = 11
  Length = 12
  Placement = pos=(-98,-27,40) rot=(0,0,1;0rad)
  Width = 15
FEATURE [Part::Box] Box503  label="立方体475"
  AttacherType = Attacher::AttachEngine3D
  Height = 11
  Length = 12
  Placement = pos=(18,-27,40) rot=(0,0,1;0rad)
  Width = 15
FEATURE [Part::Cylinder] Cylinder396  label="円柱396"
  Angle = 360
  AttacherType = Attacher::AttachEngine3D
  FirstAngle = 0
  Height = 13
  Placement = pos=(-16,-69,-5) rot=(0,0,1;0rad)
  Radius = 2
  SecondAngle = 0
FEATURE [Part::Cylinder] Cylinder397  label="円柱397"
  Angle = 360
  AttacherType = Attacher::AttachEngine3D
  FirstAngle = 0
  Height = 13
  Placement = pos=(-48,-69,-5) rot=(0,0,1;0rad)
  Radius = 2
  SecondAngle = 0
FEATURE [Part::MultiFuse] Fusion394
  Placement = pos=(-2.5,50,51) rot=(0,0,1;0rad)
  Shapes = -> [Cylinder396,Cylinder397]
FEATURE [Part::Box] Box504  label="立方体476"
  AttacherType = Attacher::AttachEngine3D
  Height = 4
  Length = 8
  Placement = pos=(-55,-24.5,51) rot=(0,0,1;0rad)
  Width = 11
FEATURE [Part::Box] Box505  label="立方体477"
  AttacherType = Attacher::AttachEngine3D
  Height = 4
  Length = 8
  Placement = pos=(-22,-24.5,51) rot=(0,0,1;0rad)
  Width = 11
FEATURE [Part::MultiFuse] Fusion395
  Shapes = -> [Box505,Box478,Box486,Box483,Box485,Box484,Box504]
FEATURE [Part::Cut] Cut425
  Base = -> Fusion395
  Tool = -> Fusion394
FEATURE [Part::Box] Box506  label="立方体478"
  AttacherType = Attacher::AttachEngine3D
  Height = 4
  Length = 4
  Placement = pos=(-26,-10.5,51) rot=(0,0,1;0rad)
  Width = 4
FEATURE [Part::Box] Box507  label="立方体479"
  AttacherType = Attacher::AttachEngine3D
  Height = 4
  Length = 4
  Placement = pos=(-26,-23.5,51) rot=(0,0,1;0rad)
  Width = 4
FEATURE [Part::Box] Box508  label="立方体480"
  AttacherType = Attacher::AttachEngine3D
  Height = 4
  Length = 4
  Placement = pos=(-47,-10.5,51) rot=(0,0,1;0rad)
  Width = 4
FEATURE [Part::Box] Box509  label="立方体481"
  AttacherType = Attacher::AttachEngine3D
  Height = 4
  Length = 4
  Placement = pos=(-47,-23.5,51) rot=(0,0,1;0rad)
  Width = 4
FEATURE [Part::Box] Box510  label="立方体482"
  AttacherType = Attacher::AttachEngine3D
  Height = 1.5
  Length = 25
  Placement = pos=(-47,-24.5,53.5) rot=(0,0,1;0rad)
  Width = 18
FEATURE [Part::Box] Box511  label="立方体483"
  AttacherType = Attacher::AttachEngine3D
  Height = 4
  Length = 8
  Placement = pos=(-55,-24.5,51) rot=(0,0,1;0rad)
  Width = 11
FEATURE [Part::Box] Box512  label="立方体484"
  AttacherType = Attacher::AttachEngine3D
  Height = 4
  Length = 8
  Placement = pos=(-22,-24.5,51) rot=(0,0,1;0rad)
  Width = 11
FEATURE [Part::Cylinder] Cylinder398  label="円柱398"
  Angle = 360
  AttacherType = Attacher::AttachEngine3D
  FirstAngle = 0
  Height = 13
  Placement = pos=(-16,-69,-5) rot=(0,0,1;0rad)
  Radius = 2
  SecondAngle = 0
FEATURE [Part::Cylinder] Cylinder399  label="円柱399"
  Angle = 360
  AttacherType = Attacher::AttachEngine3D
  FirstAngle = 0
  Height = 13
  Placement = pos=(-48,-69,-5) rot=(0,0,1;0rad)
  Radius = 2
  SecondAngle = 0
FEATURE [Part::MultiFuse] Fusion396
  Placement = pos=(-2.5,50,51) rot=(0,0,1;0rad)
  Shapes = -> [Cylinder398,Cylinder399]
FEATURE [Part::MultiFuse] Fusion397
  Shapes = -> [Box512,Box506,Box510,Box507,Box509,Box508,Box511]
FEATURE [Part::Cut] Cut427
  Base = -> Fusion397
  Placement = pos=(0.5,-149,15.5) rot=(-1,0,0;1.5708rad)
  Tool = -> Fusion396
FEATURE [Part::Cut] Cut428
  Base = -> Box386
  Tool = -> Fusion221
FEATURE [Part::Cylinder] Cylinder189  label="円柱189"
  Angle = 360
  AttacherType = Attacher::AttachEngine3D
  FirstAngle = 0
  Height = 20
  Placement = pos=(-50.5,-88,34.5) rot=(1,0,0;1.5708rad)
  Radius = 2
  SecondAngle = 0
FEATURE [Part::Cut] Cut429
  Base = -> Cut428
  Tool = -> Box403
FEATURE [Part::Cut] Cut430
  Base = -> Cut429
  Tool = -> Cylinder190
FEATURE [Part::Cut] Cut431
  Base = -> Cut430
  Placement = pos=(0.5,0,0) rot=(0,0,1;0rad)
  Tool = -> Cylinder189
FEATURE [Part::Box] Box513  label="立方体485"
  AttacherType = Attacher::AttachEngine3D
  Height = 3
  Length = 136
  Placement = pos=(-102,-108,0) rot=(0,0,1;0rad)
  Width = 10
FEATURE [Part::Cylinder] Cylinder400  label="円柱400"
  Angle = 360
  AttacherType = Attacher::AttachEngine3D
  FirstAngle = 0
  Height = 44
  Placement = pos=(-126,-72,10.7) rot=(0,1,0;1.5708rad)
  Radius = 2
  SecondAngle = 0
FEATURE [Part::Box] Box514  label="立方体486"
  AttacherType = Attacher::AttachEngine3D
  Height = 20
  Length = 20
  Placement = pos=(14,-78,0) rot=(0,0,1;0rad)
  Width = 15
FEATURE [Part::Cylinder] Cylinder401  label="円柱401"
  Angle = 360
  AttacherType = Attacher::AttachEngine3D
  FirstAngle = 0
  Height = 30
  Placement = pos=(18,-72,10.79) rot=(0,1,0;1.5708rad)
  Radius = 4
  SecondAngle = 0
FEATURE [Part::Cylinder] Cylinder402  label="円柱402"
  Angle = 360
  AttacherType = Attacher::AttachEngine3D
  FirstAngle = 0
  Height = 44
  Placement = pos=(14,-72,10.79) rot=(0,1,0;1.5708rad)
  Radius = 2
  SecondAngle = 0
FEATURE [Part::Cut] Cut432
  Base = -> Box454
  Tool = -> Cylinder354
FEATURE [Part::Cut] Cut433
  Base = -> Cut432
  Tool = -> Cylinder400
FEATURE [Part::Cut] Cut434
  Base = -> Box514
  Tool = -> Cylinder401
FEATURE [Part::Cut] Cut435
  Base = -> Cut434
  Tool = -> Cylinder402
FEATURE [Part::MultiFuse] Fusion398
  Shapes = -> [Cut435,Cut433]
FEATURE [Part::Box] Box515  label="立方体487"
  AttacherType = Attacher::AttachEngine3D
  Height = 20
  Length = 20
  Placement = pos=(-102,-78,0) rot=(0,0,1;0rad)
  Width = 15
FEATURE [Part::Box] Box516  label="立方体488"
  AttacherType = Attacher::AttachEngine3D
  Height = 20
  Length = 20
  Placement = pos=(14,-78,0) rot=(0,0,1;0rad)
  Width = 15
FEATURE [Part::Cylinder] Cylinder403  label="円柱403"
  Angle = 360
  AttacherType = Attacher::AttachEngine3D
  FirstAngle = 0
  Height = 30
  Placement = pos=(-116,-72,10.79) rot=(0,1,0;1.5708rad)
  Radius = 4
  SecondAngle = 0
FEATURE [Part::Cut] Cut436
  Base = -> Box515
  Tool = -> Cylinder403
FEATURE [Part::Cylinder] Cylinder404  label="円柱404"
  Angle = 360
  AttacherType = Attacher::AttachEngine3D
  FirstAngle = 0
  Height = 44
  Placement = pos=(-126,-72,10.7) rot=(0,1,0;1.5708rad)
  Radius = 2
  SecondAngle = 0
FEATURE [Part::Cut] Cut437
  Base = -> Cut436
  Tool = -> Cylinder404
FEATURE [Part::Cylinder] Cylinder405  label="円柱405"
  Angle = 360
  AttacherType = Attacher::AttachEngine3D
  FirstAngle = 0
  Height = 30
  Placement = pos=(18,-72,10.79) rot=(0,1,0;1.5708rad)
  Radius = 4
  SecondAngle = 0
FEATURE [Part::Cut] Cut438
  Base = -> Box516
  Tool = -> Cylinder405
FEATURE [Part::Cylinder] Cylinder406  label="円柱406"
  Angle = 360
  AttacherType = Attacher::AttachEngine3D
  FirstAngle = 0
  Height = 44
  Placement = pos=(14,-72,10.79) rot=(0,1,0;1.5708rad)
  Radius = 2
  SecondAngle = 0
FEATURE [Part::Cut] Cut439
  Base = -> Cut438
  Tool = -> Cylinder406
FEATURE [Part::MultiFuse] Fusion399
  Placement = pos=(0,123,0) rot=(0,0,1;0rad)
  Shapes = -> [Cut439,Cut437]
FEATURE [Part::MultiFuse] Fusion392
  Placement = pos=(0,26,0) rot=(0,0,1;0rad)
  Shapes = -> [Box503,Box501,Box502]
FEATURE [Part::Box] Box517  label="立方体489"
  AttacherType = Attacher::AttachEngine3D
  Height = 4
  Length = 128
  Placement = pos=(-98,-27,47) rot=(0,0,1;0rad)
  Width = 16
FEATURE [Part::Box] Box518  label="立方体490"
  AttacherType = Attacher::AttachEngine3D
  Height = 11
  Length = 12
  Placement = pos=(-98,-27,40) rot=(0,0,1;0rad)
  Width = 16
FEATURE [Part::Box] Box519  label="立方体491"
  AttacherType = Attacher::AttachEngine3D
  Height = 11
  Length = 12
  Placement = pos=(18,-27,40) rot=(0,0,1;0rad)
  Width = 16
FEATURE [Part::MultiFuse] Fusion400
  Placement = pos=(0,-29,0) rot=(0,0,1;0rad)
  Shapes = -> [Box519,Box517,Box518]
FEATURE [Part::Box] Box520  label="立方体492"
  AttacherType = Attacher::AttachEngine3D
  Height = 35
  Length = 45.1
  Placement = pos=(-34,-146,-17) rot=(0,0,1;0rad)
  Width = 25
FEATURE [Part::Box] Box521  label="立方体493"
  AttacherType = Attacher::AttachEngine3D
  Height = 32.7
  Length = 12.1
  Placement = pos=(0,8.5,-4.9) rot=(0,0,1;0rad)
  Width = 2.5
FEATURE [Part::Box] Box522  label="立方体494"
  AttacherType = Attacher::AttachEngine3D
  Height = 22.7
  Length = 12.1
  Width = 26.7
FEATURE [Part::Box] Box523  label="立方体495"
  AttacherType = Attacher::AttachEngine3D
  Height = 35
  Length = 12.1
  Placement = pos=(-1,-135,-17) rot=(0,0,1;0rad)
  Width = 14
FEATURE [Part::Box] Box524  label="立方体496"
  AttacherType = Attacher::AttachEngine3D
  Height = 67
  Length = 15
  Placement = pos=(-24.3,-155,15) rot=(0,0,1;0rad)
  Width = 39
FEATURE [Part::Box] Box525  label="立方体497"
  AttacherType = Attacher::AttachEngine3D
  Height = 20
  Length = 15
  Placement = pos=(-26.6,-113,62) rot=(0,0,1;0rad)
  Width = 24
FEATURE [Part::Box] Box526  label="立方体498"
  AttacherType = Attacher::AttachEngine3D
  Height = 13
  Length = 7
  Placement = pos=(-26.6,-113,65.5) rot=(0,0,1;0rad)
  Width = 34
FEATURE [Part::Chamfer] Chamfer045
  Base = -> Box524
  EdgeLinks = -> Box524 [Edge10]
  Edges = 1 edges r=30: [Edge10]
FEATURE [Part::Chamfer] Chamfer046
  Base = -> Chamfer045
  EdgeLinks = -> Chamfer045 [Edge2,Edge6,Edge7,Edge10]
  Edges = 4 edges r=5: [Edge2,Edge6,Edge7,Edge10]
  Placement = pos=(-2.3,0,0) rot=(0,0,1;0rad)
FEATURE [Part::Cone] Cone006  label="円錐006"
  Angle = 360
  AttacherType = Attacher::AttachEngine3D
  Height = 7
  Radius1 = 38
  Radius2 = 29
FEATURE [Part::Cone] Cone007  label="円錐007"
  Angle = 360
  AttacherType = Attacher::AttachEngine3D
  Height = 7
  Radius1 = 33
  Radius2 = 26
FEATURE [Part::Cut] Cut441
  Base = -> Cone006
  Placement = pos=(-34,-145,-22) rot=(0,0,1;0rad)
  Tool = -> Cone007
FEATURE [Part::Chamfer] Chamfer047
  Base = -> Cut441
  EdgeLinks = -> Cut441 [Edge3]
  Edges = 1 edges r=2: [Edge3]
FEATURE [Part::Cylinder] Cylinder407  label="円柱407"
  Angle = 360
  AttacherType = Attacher::AttachEngine3D
  FirstAngle = 0
  Height = 50
  Radius = 1.05
  SecondAngle = 0
FEATURE [Part::Cylinder] Cylinder408  label="円柱408"
  Angle = 360
  AttacherType = Attacher::AttachEngine3D
  FirstAngle = 0
  Height = 20
  Placement = pos=(-57,-145,-26) rot=(0,-1,0;0.785398rad)
  Radius = 1.5
  SecondAngle = 0
FEATURE [Part::Cylinder] Cylinder409  label="円柱409"
  Angle = 360
  AttacherType = Attacher::AttachEngine3D
  FirstAngle = 0
  Height = 20
  Placement = pos=(-11,-145,-26) rot=(0,1,0;0.785398rad)
  Radius = 1
  SecondAngle = 0
FEATURE [Part::Cylinder] Cylinder410  label="円柱410"
  Angle = 360
  AttacherType = Attacher::AttachEngine3D
  FirstAngle = 0
  Height = 3
  Placement = pos=(6.05,0,16.4) rot=(1,0,0;1.5708rad)
  Radius = 2.4
  SecondAngle = 0
FEATURE [Part::Cylinder] Cylinder411  label="円柱411"
  Angle = 360
  AttacherType = Attacher::AttachEngine3D
  FirstAngle = 0
  Height = 50
  Placement = pos=(0,-27.7,0) rot=(0,0,1;0rad)
  Radius = 1.05
  SecondAngle = 0
FEATURE [Part::Cylinder] Cylinder412  label="円柱412"
  Angle = 360
  AttacherType = Attacher::AttachEngine3D
  FirstAngle = 0
  Height = 40
  Placement = pos=(-34,-145,-15) rot=(0,0,1;0rad)
  Radius = 29
  SecondAngle = 0
FEATURE [Part::Cylinder] Cylinder413  label="円柱413"
  Angle = 360
  AttacherType = Attacher::AttachEngine3D
  FirstAngle = 0
  Height = 40
  Placement = pos=(-34,-145,-27) rot=(0,0,1;0rad)
  Radius = 26
  SecondAngle = 0
FEATURE [Part::Cylinder] Cylinder414  label="円柱414"
  Angle = 90
  AttacherType = Attacher::AttachEngine3D
  FirstAngle = 0
  Height = 40
  Radius = 29
  SecondAngle = 0
FEATURE [Part::Cylinder] Cylinder415  label="円柱415"
  Angle = 90
  AttacherType = Attacher::AttachEngine3D
  FirstAngle = 0
  Height = 40
  Radius = 35
  SecondAngle = 0
FEATURE [Part::Cut] Cut440
  Base = -> Cylinder415
  Placement = pos=(-34,-145,-17) rot=(0,0,1;0rad)
  Tool = -> Cylinder414
FEATURE [Part::Cylinder] Cylinder416  label="円柱416"
  Angle = 360
  AttacherType = Attacher::AttachEngine3D
  FirstAngle = 0
  Height = 50
  Placement = pos=(-36,-132,56) rot=(0.57735,0.57735,0.57735;2.0944rad)
  Radius = 7
  SecondAngle = 0
FEATURE [Part::Cut] Cut445
  Base = -> Chamfer046
  Tool = -> Cylinder416
FEATURE [Part::Cylinder] Cylinder417  label="円柱417"
  Angle = 360
  AttacherType = Attacher::AttachEngine3D
  FirstAngle = 0
  Height = 40
  Placement = pos=(-34,-145,-27) rot=(0,0,1;0rad)
  Radius = 26
  SecondAngle = 0
FEATURE [Part::Cylinder] Cylinder418  label="円柱418"
  Angle = 90
  AttacherType = Attacher::AttachEngine3D
  FirstAngle = 0
  Height = 79
  Radius = 29
  SecondAngle = 0
FEATURE [Part::Cylinder] Cylinder419  label="円柱419"
  Angle = 90
  AttacherType = Attacher::AttachEngine3D
  FirstAngle = 0
  Height = 79
  Radius = 50
  SecondAngle = 0
FEATURE [Part::Cut] Cut442
  Base = -> Cylinder419
  Placement = pos=(-34,-145,-17) rot=(0,0,1;0rad)
  Tool = -> Cylinder418
FEATURE [Part::Cut] Cut446
  Base = -> Cut445
  Tool = -> Cut442
FEATURE [Part::Cylinder] Cylinder420  label="円柱420"
  Angle = 360
  AttacherType = Attacher::AttachEngine3D
  FirstAngle = 0
  Height = 15
  Placement = pos=(-26.6,-89,72) rot=(0.57735,0.57735,0.57735;2.0944rad)
  Radius = 10
  SecondAngle = 0
FEATURE [Part::Cylinder] Cylinder421  label="円柱421"
  Angle = 360
  AttacherType = Attacher::AttachEngine3D
  FirstAngle = 0
  Height = 25
  Placement = pos=(-31.3,-89,72) rot=(0.57735,0.57735,0.57735;2.0944rad)
  Radius = 1.6
  SecondAngle = 0
FEATURE [Part::MultiFuse] Fusion402
  Placement = pos=(92.57,-66.51,0) rot=(0,0,-1;0.785398rad)
  Shapes = -> [Cylinder409,Cylinder408]
FEATURE [Part::MultiFuse] Fusion403
  Placement = pos=(-1,-151,-12) rot=(0,0,1;0rad)
  Shapes = -> [Cylinder410,Box521,Box522]
FEATURE [Part::Cut] Cut450
  Base = -> Box520
  Tool = -> Fusion403
FEATURE [Part::Cut] Cut451
  Base = -> Cut450
  Tool = -> Box523
FEATURE [Part::MultiFuse] Fusion404
  Placement = pos=(4.1,-111,13.1) rot=(1,0,0;1.5708rad)
  Shapes = -> [Cylinder407,Cylinder411]
FEATURE [Part::Cut] Cut452
  Base = -> Cut451
  Placement = pos=(-4,-10,2) rot=(0,0,1;0rad)
  Tool = -> Fusion404
FEATURE [Part::Cut] Cut453
  Base = -> Cut452
  Tool = -> Cut440
FEATURE [Part::MultiFuse] Fusion406
  Placement = pos=(-30.8902,3.9004,0) rot=(0,0,1;0.20944rad)
  Refine = true
  Shapes = -> [Fusion402]
FEATURE [Part::MultiFuse] Fusion407
  Refine = true
  Shapes = -> [Box525,Cylinder420]
FEATURE [Part::Cut] Cut448
  Base = -> Fusion407
  Tool = -> Cylinder421
FEATURE [Part::Cut] Cut449
  Base = -> Cut448
  Tool = -> Box526
FEATURE [Part::Sphere] Sphere011  label="球体011"
  Angle1 = 0
  Angle2 = 60
  Angle3 = 360
  AttacherType = Attacher::AttachEngine3D
  Placement = pos=(-34,-145,25) rot=(0,0,1;0rad)
  Radius = 29
FEATURE [Part::MultiFuse] Fusion408
  Shapes = -> [Chamfer047,Cylinder412,Sphere011]
FEATURE [Part::Sphere] Sphere012  label="球体012"
  Angle1 = 0
  Angle2 = 60
  Angle3 = 360
  AttacherType = Attacher::AttachEngine3D
  Placement = pos=(-34,-145,13) rot=(0,0,1;0rad)
  Radius = 26
FEATURE [Part::MultiFuse] Fusion405
  Placement = pos=(0,0,12) rot=(0,0,1;0rad)
  Shapes = -> [Cylinder413,Sphere012]
FEATURE [Part::Sphere] Sphere013  label="球体013"
  Angle1 = 0
  Angle2 = 60
  Angle3 = 360
  AttacherType = Attacher::AttachEngine3D
  Placement = pos=(-34,-145,13) rot=(0,0,1;0rad)
  Radius = 26
FEATURE [Part::MultiFuse] Fusion401
  Placement = pos=(0,0,17) rot=(0,0,1;0rad)
  Shapes = -> [Cylinder417,Sphere013]
FEATURE [Part::Cut] Cut447
  Base = -> Cut446
  Tool = -> Fusion401
FEATURE [Part::Sphere] Sphere014  label="球体014"
  Angle1 = -90
  Angle2 = 90
  Angle3 = 360
  AttacherType = Attacher::AttachEngine3D
  Placement = pos=(-34,-119,-36) rot=(0,0,1;0rad)
  Radius = 30
FEATURE [Part::Cut] Cut443
  Base = -> Fusion408
  Tool = -> Sphere014
FEATURE [Part::Cut] Cut444
  Base = -> Cut443
  Tool = -> Fusion406
FEATURE [Part::MultiFuse] Fusion409
  Shapes = -> [Cut453,Cut444]
FEATURE [Part::Cut] Cut454
  Base = -> Fusion409
  Placement = pos=(0,0,5) rot=(0,0,1;0rad)
  Tool = -> Fusion405
FEATURE [Part::MultiFuse] Fusion410
  Placement = pos=(0,3,0) rot=(0,0,1;0rad)
  Shapes = -> [Cut447,Cut454]
FEATURE [Part::MultiFuse] Fusion411
  Placement = pos=(0,-178,144) rot=(-1,0,0;3.14159rad)
  Shapes = -> [Cut449,Fusion410]
FEATURE [Part::Box] Box527  label="立方体499"
  AttacherType = Attacher::AttachEngine3D
  Height = 3
  Length = 41
  Placement = pos=(-55,-40,48) rot=(0,0,1;0rad)
  Width = 39
FEATURE [Part::Cut] Cut455
  Base = -> Box477
  Placement = pos=(0,0,1) rot=(0,0,1;0rad)
  Tool = -> Box500
FEATURE [Part::Cut] Cut456
  Base = -> Box527
  Tool = -> Fusion211
FEATURE [Part::Cut] Cut457
  Base = -> Cut456
  Tool = -> Fusion362
FEATURE [Part::Box] Box528  label="立方体500"
  AttacherType = Attacher::AttachEngine3D
  Height = 5
  Length = 43
  Placement = pos=(8,-18,0) rot=(0,0,1;0rad)
  Width = 16
FEATURE [Part::Box] Box529  label="立方体501"
  AttacherType = Attacher::AttachEngine3D
  Height = 5
  Length = 43
  Placement = pos=(-119,-18,0) rot=(0,0,1;0rad)
  Width = 16
FEATURE [Part::Cylinder] Cylinder422  label="円柱422"
  Angle = 360
  AttacherType = Attacher::AttachEngine3D
  FirstAngle = 0
  Height = 32
  Placement = pos=(30.2,-10,0) rot=(0,0,1;0rad)
  Radius = 4
  SecondAngle = 0
FEATURE [Part::Cut] Cut459
  Base = -> Box528
  Tool = -> Cylinder422
FEATURE [Part::Cylinder] Cylinder423  label="円柱423"
  Angle = 360
  AttacherType = Attacher::AttachEngine3D
  FirstAngle = 0
  Height = 32
  Placement = pos=(-98,-10,0) rot=(0,0,1;0rad)
  Radius = 4
  SecondAngle = 0
FEATURE [Part::Cut] Cut458
  Base = -> Box529
  Tool = -> Cylinder423
FEATURE [Part::Cylinder] Cylinder424  label="円柱424"
  Angle = 360
  AttacherType = Attacher::AttachEngine3D
  FirstAngle = 0
  Height = 170
  Placement = pos=(-119,28,146.3) rot=(0,1,0;1.5708rad)
  Radius = 10
  SecondAngle = 0
FEATURE [Part::Cylinder] Cylinder425  label="円柱425"
  Angle = 360
  AttacherType = Attacher::AttachEngine3D
  FirstAngle = 0
  Height = 42
  Placement = pos=(-85,-10,-5) rot=(0,0,1;0rad)
  Radius = 2
  SecondAngle = 0
FEATURE [Part::Cut] Cut460
  Base = -> Cut458
  Tool = -> Cylinder425
FEATURE [Part::Cylinder] Cylinder426  label="円柱426"
  Angle = 360
  AttacherType = Attacher::AttachEngine3D
  FirstAngle = 0
  Height = 42
  Placement = pos=(17.2,-10,-5) rot=(0,0,1;0rad)
  Radius = 2
  SecondAngle = 0
FEATURE [Part::Cut] Cut461
  Base = -> Cut459
  Tool = -> Cylinder426
FEATURE [Part::Part2DObjectPython] Wire006  # Draft 2D object (typed FeaturePython)
  Area = 2400
  ChamferSize = 0
  Closed = true
  End = (40,150,0)
  FilletRadius = 0
  Length = 342.483
  MakeFace = true
  Points = (4) [(0,0,0),(16,0,0),(56,150,0),(40,150,0)]
  Start = (0,0,0)
  Subdivisions = 0
FEATURE [Part::Extrusion] Extrude011
  Base = -> Wire006
  Dir = (0,0,1)
  DirMode = 2
  FaceMakerClass = Part::FaceMakerBullseye
  FaceMakerMode = 3
  LengthFwd = 10
  LengthRev = 0
  Solid = false
  Symmetric = false
FEATURE [Part::Fillet] Fillet030
  Base = -> Extrude011
  EdgeLinks = -> Extrude011 [Edge5,Edge8]
  Edges = 2 edges r=7.72: [Edge5,Edge8]
  Placement = pos=(41,-18,5) rot=(0.57735,0.57735,0.57735;2.0944rad)
FEATURE [Part::Part2DObjectPython] Wire007  # Draft 2D object (typed FeaturePython)
  Area = 2400
  ChamferSize = 0
  Closed = true
  End = (40,150,0)
  FilletRadius = 0
  Length = 342.483
  MakeFace = true
  Points = (4) [(0,0,0),(16,0,0),(56,150,0),(40,150,0)]
  Start = (0,0,0)
  Subdivisions = 0
FEATURE [Part::Extrusion] Extrude012
  Base = -> Wire007
  Dir = (0,0,1)
  DirMode = 2
  FaceMakerClass = Part::FaceMakerBullseye
  FaceMakerMode = 3
  LengthFwd = 10
  LengthRev = 0
  Solid = false
  Symmetric = false
FEATURE [Part::Fillet] Fillet031
  Base = -> Extrude012
  EdgeLinks = -> Extrude012 [Edge5,Edge8]
  Edges = 2 edges r=7.72: [Edge5,Edge8]
  Placement = pos=(-119,-18,5) rot=(0.57735,0.57735,0.57735;2.0944rad)
FEATURE [Part::MultiFuse] Fusion412
  Shapes = -> [Fillet030,Cylinder424,Fillet031]
FEATURE [Part::MultiFuse] Fusion413  label="持ち手001"
  Placement = pos=(0,0,20.1) rot=(0,0,1;0rad)
  Shapes = -> [Cut460,Fusion412,Cut461]
FEATURE [Part::Box] Box530  label="立方体502"
  AttacherType = Attacher::AttachEngine3D
  Height = 7
  Length = 29.2
  Width = 10
FEATURE [Part::Box] Box531  label="立方体503"
  AttacherType = Attacher::AttachEngine3D
  Height = 4
  Length = 2
  Placement = pos=(6.6,-1,1.4) rot=(0,0,1;0rad)
  Width = 1
FEATURE [Part::MultiFuse] Fusion414  label="microswitchR"
  Placement = pos=(-89,-108,3) rot=(0,0,1;0rad)
  Shapes = -> [Box530,Box531]
FEATURE [Part::Box] Box532  label="立方体504"
  AttacherType = Attacher::AttachEngine3D
  Height = 7
  Length = 29.2
  Width = 10
FEATURE [Part::Box] Box533  label="立方体505"
  AttacherType = Attacher::AttachEngine3D
  Height = 4
  Length = 2
  Placement = pos=(20.6,-1,1.4) rot=(0,0,1;0rad)
  Width = 1
FEATURE [Part::MultiFuse] Fusion001  label="microswitchL"
  Placement = pos=(-8.2,-108,3) rot=(0,0,1;0rad)
  Shapes = -> [Box533,Box532]
FEATURE [Part::Cylinder] Cylinder427  label="円柱427"
  Angle = 360
  AttacherType = Attacher::AttachEngine3D
  FirstAngle = 0
  Height = 7
  Placement = pos=(-46,-103,3) rot=(0,0,1;0rad)
  Radius = 4
  SecondAngle = 0
FEATURE [Part::Cylinder] Cylinder428  label="円柱428"
  Angle = 360
  AttacherType = Attacher::AttachEngine3D
  FirstAngle = 0
  Height = 7
  Placement = pos=(-46,-103,3) rot=(0,0,1;0rad)
  Radius = 3.25
  SecondAngle = 0
FEATURE [Part::Box] Box534  label="立方体506"
  AttacherType = Attacher::AttachEngine3D
  Height = 7
  Length = 2.5
  Placement = pos=(-47.25,-110,3) rot=(0,0,1;0rad)
  Width = 6
FEATURE [Part::Box] Box535  label="立方体507"
  AttacherType = Attacher::AttachEngine3D
  Height = 7
  Length = 36
  Placement = pos=(-52,-108,3) rot=(0,0,1;0rad)
  Width = 10
FEATURE [Part::Cylinder] Cylinder429  label="円柱429"
  Angle = 360
  AttacherType = Attacher::AttachEngine3D
  FirstAngle = 0
  Height = 7
  Placement = pos=(-22,-103,3) rot=(0,0,1;0rad)
  Radius = 4
  SecondAngle = 0
FEATURE [Part::Cylinder] Cylinder430  label="円柱430"
  Angle = 360
  AttacherType = Attacher::AttachEngine3D
  FirstAngle = 0
  Height = 7
  Placement = pos=(-22,-103,3) rot=(0,0,1;0rad)
  Radius = 3.25
  SecondAngle = 0
FEATURE [Part::Box] Box536  label="立方体508"
  AttacherType = Attacher::AttachEngine3D
  Height = 7
  Length = 3
  Placement = pos=(-23.5,-109,3) rot=(0,0,1;0rad)
  Width = 6
FEATURE [Part::Box] Box537  label="立方体509"
  AttacherType = Attacher::AttachEngine3D
  Height = 7
  Length = 3
  Placement = pos=(-47.5,-109,3) rot=(0,0,1;0rad)
  Width = 6
FEATURE [Part::Box] Box538  label="立方体510"
  AttacherType = Attacher::AttachEngine3D
  Height = 7
  Length = 2.5
  Placement = pos=(-23.25,-110,3) rot=(0,0,1;0rad)
  Width = 6
FEATURE [Part::MultiFuse] Fusion415
  Shapes = -> [Cylinder427,Box537]
FEATURE [Part::MultiFuse] Fusion416
  Shapes = -> [Cylinder429,Box536]
FEATURE [Part::MultiFuse] Fusion417
  Shapes = -> [Fusion415,Fusion416]
FEATURE [Part::Cut] Cut462
  Base = -> Box535
  Tool = -> Fusion417
FEATURE [Part::MultiFuse] Fusion418
  Placement = pos=(0,-0.5,0) rot=(0,0,1;0rad)
  Shapes = -> [Cylinder428,Cylinder430]
FEATURE [Part::MultiFuse] Fusion419
  Shapes = -> [Box534,Box538]
FEATURE [Part::Box] Box539  label="立方体511"
  AttacherType = Attacher::AttachEngine3D
  Height = 7
  Length = 166
  Placement = pos=(-117,-117,3) rot=(0,0,1;0rad)
  Width = 7
FEATURE [Part::Box] Box540  label="立方体512"
  AttacherType = Attacher::AttachEngine3D
  Height = 7
  Length = 4
  Placement = pos=(-83.4,-110,3) rot=(0,0,1;0rad)
  Width = 1
FEATURE [Part::Chamfer] Chamfer
  Base = -> Box540
  EdgeLinks = -> Box540 [Edge3,Edge7]
  Edges = 2 edges r=0.99: [Edge3,Edge7]
FEATURE [Part::Box] Box541  label="立方体513"
  AttacherType = Attacher::AttachEngine3D
  Height = 7
  Length = 4
  Placement = pos=(-83.4,-110,3) rot=(0,0,1;0rad)
  Width = 1
FEATURE [Part::Chamfer] Chamfer048
  Base = -> Box541
  EdgeLinks = -> Box541 [Edge3,Edge7]
  Edges = 2 edges r=0.99: [Edge3,Edge7]
  Placement = pos=(94.8,0,0) rot=(0,0,1;0rad)
FEATURE [Part::Cylinder] Cylinder431  label="円柱431"
  Angle = 360
  AttacherType = Attacher::AttachEngine3D
  FirstAngle = 0
  Height = 10
  Placement = pos=(-34.3,-103,0) rot=(0,0,1;0rad)
  Radius = 1.6
  SecondAngle = 0
FEATURE [Part::Cylinder] Cylinder432  label="円柱432"
  Angle = 360
  AttacherType = Attacher::AttachEngine3D
  FirstAngle = 0
  Height = 70
  Placement = pos=(-92,-103,-10) rot=(0,0,1;0rad)
  Radius = 2
  SecondAngle = 0
FEATURE [Part::Cylinder] Cylinder433  label="円柱433"
  Angle = 360
  AttacherType = Attacher::AttachEngine3D
  FirstAngle = 0
  Height = 70
  Placement = pos=(24,-103,-10) rot=(0,0,1;0rad)
  Radius = 2
  SecondAngle = 0
FEATURE [Part::MultiFuse] Fusion421
  Shapes = -> [Cylinder432,Cylinder433]
FEATURE [Part::Box] Box542  label="立方体514"
  AttacherType = Attacher::AttachEngine3D
  Height = 7
  Length = 13
  Placement = pos=(-102,-108,3) rot=(0,0,1;0rad)
  Width = 10
FEATURE [Part::Box] Box543  label="立方体515"
  AttacherType = Attacher::AttachEngine3D
  Height = 7
  Length = 13
  Placement = pos=(21,-108,3) rot=(0,0,1;0rad)
  Width = 10
FEATURE [Part::Cylinder] Cylinder434  label="円柱434"
  Angle = 360
  AttacherType = Attacher::AttachEngine3D
  FirstAngle = 0
  Height = 5
  Placement = pos=(-34.3,-103,-5) rot=(0,0,1;0rad)
  Radius = 3
  SecondAngle = 0
FEATURE [Part::Cut] Cut463
  Base = -> Cut423
  Tool = -> Cylinder434
FEATURE [Part::Cylinder] Cylinder435  label="円柱435"
  Angle = 360
  AttacherType = Attacher::AttachEngine3D
  FirstAngle = 0
  Height = 70
  Placement = pos=(-92,-103,-10) rot=(0,0,1;0rad)
  Radius = 2
  SecondAngle = 0
FEATURE [Part::Cylinder] Cylinder436  label="円柱436"
  Angle = 360
  AttacherType = Attacher::AttachEngine3D
  FirstAngle = 0
  Height = 70
  Placement = pos=(24,-103,-10) rot=(0,0,1;0rad)
  Radius = 2
  SecondAngle = 0
FEATURE [Part::MultiFuse] Fusion422
  Shapes = -> [Cylinder435,Cylinder436]
FEATURE [Part::MultiFuse] Fusion423
  Shapes = -> [Box543,Box542]
FEATURE [Part::Box] Box544  label="立方体516"
  AttacherType = Attacher::AttachEngine3D
  Height = 1.5
  Length = 136
  Placement = pos=(-102,-108,10) rot=(0,0,1;0rad)
  Width = 10
FEATURE [Part::Cylinder] Cylinder437  label="円柱437"
  Angle = 360
  AttacherType = Attacher::AttachEngine3D
  FirstAngle = 0
  Height = 13
  Placement = pos=(-34.3,-103,0) rot=(0,0,1;0rad)
  Radius = 1.6
  SecondAngle = 0
FEATURE [Part::Cut] Cut466
  Base = -> Box544
  Tool = -> Cylinder437
FEATURE [Part::Cut] Cut467
  Base = -> Cut466
  Tool = -> Fusion421
FEATURE [Part::MultiFuse] Fusion424
  Shapes = -> [Cut462,Box513,Fusion423]
FEATURE [Part::Cut] Cut468
  Base = -> Fusion424
  Tool = -> Cylinder431
FEATURE [Part::Cut] Cut469
  Base = -> Cut468
  Tool = -> Fusion422
FEATURE [Part::Cylinder] Cylinder438  label="円柱438"
  Angle = 360
  AttacherType = Attacher::AttachEngine3D
  FirstAngle = 0
  Height = 13
  Placement = pos=(15.3,-100.3,0) rot=(0,0,1;0rad)
  Radius = 1.1
  SecondAngle = 0
FEATURE [Part::Cylinder] Cylinder439  label="円柱439"
  Angle = 360
  AttacherType = Attacher::AttachEngine3D
  FirstAngle = 0
  Height = 13
  Placement = pos=(5.8,-100.3,0) rot=(0,0,1;0rad)
  Radius = 1.1
  SecondAngle = 0
FEATURE [Part::Cylinder] Cylinder440  label="円柱440"
  Angle = 360
  AttacherType = Attacher::AttachEngine3D
  FirstAngle = 0
  Height = 2
  Placement = pos=(15.3,-100.3,0) rot=(0,0,1;0rad)
  Radius = 2
  SecondAngle = 0
FEATURE [Part::Cylinder] Cylinder441  label="円柱441"
  Angle = 360
  AttacherType = Attacher::AttachEngine3D
  FirstAngle = 0
  Height = 2
  Placement = pos=(5.8,-100.3,0) rot=(0,0,1;0rad)
  Radius = 2
  SecondAngle = 0
FEATURE [Part::Cylinder] Cylinder442  label="円柱442"
  Angle = 360
  AttacherType = Attacher::AttachEngine3D
  FirstAngle = 0
  Height = 13
  Placement = pos=(15.3,-100.3,0) rot=(0,0,1;0rad)
  Radius = 1.1
  SecondAngle = 0
FEATURE [Part::Cylinder] Cylinder443  label="円柱443"
  Angle = 360
  AttacherType = Attacher::AttachEngine3D
  FirstAngle = 0
  Height = 13
  Placement = pos=(5.8,-100.3,0) rot=(0,0,1;0rad)
  Radius = 1.1
  SecondAngle = 0
FEATURE [Part::Cylinder] Cylinder444  label="円柱444"
  Angle = 360
  AttacherType = Attacher::AttachEngine3D
  FirstAngle = 0
  Height = 2
  Placement = pos=(15.3,-100.3,0) rot=(0,0,1;0rad)
  Radius = 2
  SecondAngle = 0
FEATURE [Part::Cylinder] Cylinder445  label="円柱445"
  Angle = 360
  AttacherType = Attacher::AttachEngine3D
  FirstAngle = 0
  Height = 2
  Placement = pos=(5.8,-100.3,0) rot=(0,0,1;0rad)
  Radius = 2
  SecondAngle = 0
FEATURE [Part::MultiFuse] Fusion426
  Placement = pos=(-89.1,0,0) rot=(0,0,1;0rad)
  Shapes = -> [Cylinder442,Cylinder443,Cylinder444,Cylinder445]
FEATURE [Part::MultiFuse] Fusion425
  Shapes = -> [Cylinder438,Cylinder439,Cylinder440,Cylinder441]
FEATURE [Part::MultiFuse] Fusion427
  Shapes = -> [Fusion425,Fusion426]
FEATURE [Part::Cylinder] Cylinder446  label="円柱446"
  Angle = 360
  AttacherType = Attacher::AttachEngine3D
  FirstAngle = 0
  Height = 13
  Placement = pos=(15.3,-100.3,0) rot=(0,0,1;0rad)
  Radius = 1.25
  SecondAngle = 0
FEATURE [Part::Cylinder] Cylinder447  label="円柱447"
  Angle = 360
  AttacherType = Attacher::AttachEngine3D
  FirstAngle = 0
  Height = 13
  Placement = pos=(5.8,-100.3,0) rot=(0,0,1;0rad)
  Radius = 1.25
  SecondAngle = 0
FEATURE [Part::Cylinder] Cylinder448  label="円柱448"
  Angle = 360
  AttacherType = Attacher::AttachEngine3D
  FirstAngle = 0
  Height = 2
  Placement = pos=(15.3,-100.3,0) rot=(0,0,1;0rad)
  Radius = 2
  SecondAngle = 0
FEATURE [Part::Cylinder] Cylinder449  label="円柱449"
  Angle = 360
  AttacherType = Attacher::AttachEngine3D
  FirstAngle = 0
  Height = 2
  Placement = pos=(5.8,-100.3,0) rot=(0,0,1;0rad)
  Radius = 2
  SecondAngle = 0
FEATURE [Part::Cylinder] Cylinder450  label="円柱450"
  Angle = 360
  AttacherType = Attacher::AttachEngine3D
  FirstAngle = 0
  Height = 13
  Placement = pos=(15.3,-100.3,0) rot=(0,0,1;0rad)
  Radius = 1.25
  SecondAngle = 0
FEATURE [Part::Cylinder] Cylinder451  label="円柱451"
  Angle = 360
  AttacherType = Attacher::AttachEngine3D
  FirstAngle = 0
  Height = 13
  Placement = pos=(5.8,-100.3,0) rot=(0,0,1;0rad)
  Radius = 1.25
  SecondAngle = 0
FEATURE [Part::Cylinder] Cylinder452  label="円柱452"
  Angle = 360
  AttacherType = Attacher::AttachEngine3D
  FirstAngle = 0
  Height = 2
  Placement = pos=(15.3,-100.3,0) rot=(0,0,1;0rad)
  Radius = 2
  SecondAngle = 0
FEATURE [Part::Cylinder] Cylinder453  label="円柱453"
  Angle = 360
  AttacherType = Attacher::AttachEngine3D
  FirstAngle = 0
  Height = 2
  Placement = pos=(5.8,-100.3,0) rot=(0,0,1;0rad)
  Radius = 2
  SecondAngle = 0
FEATURE [Part::MultiFuse] Fusion428
  Shapes = -> [Cylinder446,Cylinder447,Cylinder448,Cylinder449]
FEATURE [Part::MultiFuse] Fusion429
  Placement = pos=(-89.1,0,0) rot=(0,0,1;0rad)
  Shapes = -> [Cylinder450,Cylinder451,Cylinder452,Cylinder453]
FEATURE [Part::MultiFuse] Fusion430
  Shapes = -> [Fusion428,Fusion429]
FEATURE [Part::Cut] Cut471
  Base = -> Cut469
  Tool = -> Fusion430
FEATURE [Part::MultiFuse] Fusion431
  Shapes = -> [Box452,Cylinder350]
FEATURE [Part::Cut] Cut472
  Base = -> Fusion431
  Tool = -> Cylinder351
FEATURE [Part::Cut] Cut473
  Base = -> Cut472
  Tool = -> Box453
FEATURE [Part::Cylinder] Cylinder454  label="円柱454"
  Angle = 360
  AttacherType = Attacher::AttachEngine3D
  FirstAngle = 0
  Height = 13
  Placement = pos=(15.3,-100.3,0) rot=(0,0,1;0rad)
  Radius = 1
  SecondAngle = 0
FEATURE [Part::Cylinder] Cylinder455  label="円柱455"
  Angle = 360
  AttacherType = Attacher::AttachEngine3D
  FirstAngle = 0
  Height = 13
  Placement = pos=(5.8,-100.3,0) rot=(0,0,1;0rad)
  Radius = 1
  SecondAngle = 0
FEATURE [Part::Cylinder] Cylinder456  label="円柱456"
  Angle = 360
  AttacherType = Attacher::AttachEngine3D
  FirstAngle = 0
  Height = 2
  Placement = pos=(15.3,-100.3,0) rot=(0,0,1;0rad)
  Radius = 2
  SecondAngle = 0
FEATURE [Part::Cylinder] Cylinder457  label="円柱457"
  Angle = 360
  AttacherType = Attacher::AttachEngine3D
  FirstAngle = 0
  Height = 2
  Placement = pos=(5.8,-100.3,0) rot=(0,0,1;0rad)
  Radius = 2
  SecondAngle = 0
FEATURE [Part::Cylinder] Cylinder458  label="円柱458"
  Angle = 360
  AttacherType = Attacher::AttachEngine3D
  FirstAngle = 0
  Height = 13
  Placement = pos=(15.3,-100.3,0) rot=(0,0,1;0rad)
  Radius = 1
  SecondAngle = 0
FEATURE [Part::Cylinder] Cylinder459  label="円柱459"
  Angle = 360
  AttacherType = Attacher::AttachEngine3D
  FirstAngle = 0
  Height = 13
  Placement = pos=(5.8,-100.3,0) rot=(0,0,1;0rad)
  Radius = 1
  SecondAngle = 0
FEATURE [Part::Cylinder] Cylinder460  label="円柱460"
  Angle = 360
  AttacherType = Attacher::AttachEngine3D
  FirstAngle = 0
  Height = 2
  Placement = pos=(15.3,-100.3,0) rot=(0,0,1;0rad)
  Radius = 2
  SecondAngle = 0
FEATURE [Part::Cylinder] Cylinder461  label="円柱461"
  Angle = 360
  AttacherType = Attacher::AttachEngine3D
  FirstAngle = 0
  Height = 2
  Placement = pos=(5.8,-100.3,0) rot=(0,0,1;0rad)
  Radius = 2
  SecondAngle = 0
FEATURE [Part::MultiFuse] Fusion432
  Shapes = -> [Cylinder454,Cylinder455,Cylinder456,Cylinder457]
FEATURE [Part::MultiFuse] Fusion433
  Placement = pos=(-89.1,0,0) rot=(0,0,1;0rad)
  Shapes = -> [Cylinder458,Cylinder459,Cylinder460,Cylinder461]
FEATURE [Part::MultiFuse] Fusion434
  Shapes = -> [Fusion432,Fusion433]
FEATURE [Part::Cut] Cut474
  Base = -> Cut467
  Refine = true
  Tool = -> Fusion427
FEATURE [Part::Cut] Cut475
  Base = -> Cut471
  Refine = true
  Tool = -> Fusion434
FEATURE [Part::Fillet] Fillet032
  Base = -> Box539
  EdgeLinks = -> Box539 [Edge1,Edge5]
  Edges = 2 edges r=6: [Edge1,Edge5]
FEATURE [Part::Fillet] Fillet033
  Base = -> Fillet032
  EdgeLinks = -> Fillet032 [Edge3,Edge13]
  Edges = 2 edges r=0.999: [Edge3,Edge13]
FEATURE [Part::MultiFuse] Fusion435  label="bumper1"
  Refine = true
  Shapes = -> [Fusion418,Fusion419,Chamfer,Chamfer048,Fillet033]
FEATURE [Part::MultiFuse] Fusion436
  Refine = true
  Shapes = -> [Cut410,Cut411]
FEATURE [Part::Box] Box545  label="立方体517"
  AttacherType = Attacher::AttachEngine3D
  Height = 4
  Length = 47.5
  Placement = pos=(-13.5,-108,33) rot=(0,0,1;0rad)
  Width = 9.9
FEATURE [Part::Box] Box546  label="立方体518"
  AttacherType = Attacher::AttachEngine3D
  Height = 4
  Length = 35
  Placement = pos=(-13.5,-108,33) rot=(0,0,1;0rad)
  Width = 3.9
FEATURE [Part::Fillet] Fillet034  label="bumper2"
  Base = -> Cut474
  EdgeLinks = -> Cut474 [Edge1,Edge6]
  Edges = 2 edges r=8: [Edge1,Edge6]
FEATURE [Part::Fillet] Fillet035  label="bumper3"
  Base = -> Cut475
  EdgeLinks = -> Cut475 [Edge94,Edge96]
  Edges = 2 edges r=8: [Edge94,Edge96]
FEATURE [Part::Fillet] Fillet036
  Base = -> Cut463
  EdgeLinks = -> Cut463 [Edge73,Edge79]
  Edges = 2 edges r=8: [Edge73,Edge79]
FEATURE [Part::Box] Box547  label="立方体519"
  AttacherType = Attacher::AttachEngine3D
  Height = 4
  Length = 47.5
  Placement = pos=(-102,-108,33) rot=(0,0,1;0rad)
  Width = 9.9
FEATURE [Part::Fillet] Fillet037
  Base = -> Box546
  EdgeLinks = -> Box546 [Edge3,Edge7]
  Edges = 2 edges r=3.899: [Edge3,Edge7]
FEATURE [Part::Box] Box548  label="立方体520"
  AttacherType = Attacher::AttachEngine3D
  Height = 4
  Length = 35
  Placement = pos=(-13.5,-108,33) rot=(0,0,1;0rad)
  Width = 3.9
FEATURE [Part::Fillet] Fillet038
  Base = -> Box548
  EdgeLinks = -> Box548 [Edge3,Edge7]
  Edges = 2 edges r=3.899: [Edge3,Edge7]
  Placement = pos=(-76,0,0) rot=(0,0,1;0rad)
FEATURE [Part::Fillet] Fillet039
  Base = -> Box545
  EdgeLinks = -> Box545 [Edge5]
  Edges = 1 edges r=8: [Edge5]
FEATURE [Part::Cut] Cut476
  Base = -> Fillet039
  Refine = true
  Tool = -> Fillet037
FEATURE [Part::Fillet] Fillet040
  Base = -> Cut476
  EdgeLinks = -> Cut476 [Edge23]
  Edges = 1 edges r=3: [Edge23]
FEATURE [Part::Cut] Cut477
  Base = -> Box547
  Refine = true
  Tool = -> Fillet038
FEATURE [Part::Fillet] Fillet041
  Base = -> Cut477
  EdgeLinks = -> Cut477 [Edge1]
  Edges = 1 edges r=8: [Edge1]
FEATURE [Part::Fillet] Fillet042
  Base = -> Fillet041
  EdgeLinks = -> Fillet041 [Edge23]
  Edges = 1 edges r=3: [Edge23]
FEATURE [Part::Cylinder] Cylinder462  label="円柱462"
  Angle = 360
  AttacherType = Attacher::AttachEngine3D
  FirstAngle = 0
  Height = 70
  Placement = pos=(-92,-103,-10) rot=(0,0,1;0rad)
  Radius = 2
  SecondAngle = 0
FEATURE [Part::Cylinder] Cylinder463  label="円柱463"
  Angle = 360
  AttacherType = Attacher::AttachEngine3D
  FirstAngle = 0
  Height = 70
  Placement = pos=(24,-103,-10) rot=(0,0,1;0rad)
  Radius = 2
  SecondAngle = 0
FEATURE [Part::MultiFuse] Fusion437
  Shapes = -> [Cylinder462,Cylinder463]
FEATURE [Part::MultiFuse] Fusion438
  Refine = true
  Shapes = -> [Fillet040,Cut431,Fillet042]
FEATURE [Part::Cut] Cut478
  Base = -> Fusion438
  Refine = true
  Tool = -> Fusion437
FEATURE [Part::Box] Box549  label="立方体521"
  AttacherType = Attacher::AttachEngine3D
  Height = 8
  Length = 3
  Placement = pos=(-78,-76,0) rot=(0,0,1;0rad)
  Width = 15
FEATURE [Part::Box] Box550  label="立方体522"
  AttacherType = Attacher::AttachEngine3D
  Height = 8
  Length = 3
  Placement = pos=(5,-76,0) rot=(0,0,1;0rad)
  Width = 15
FEATURE [Part::Box] Box551  label="立方体523"
  AttacherType = Attacher::AttachEngine3D
  Height = 8
  Length = 10
  Placement = pos=(-63.2,-84,0) rot=(0,0,1;0rad)
  Width = 8
FEATURE [Part::Box] Box552  label="立方体524"
  AttacherType = Attacher::AttachEngine3D
  Height = 9
  Length = 10
  Placement = pos=(-14.8,-84,0) rot=(0,0,1;0rad)
  Width = 8
FEATURE [Part::Box] Box554  label="立方体526"
  AttacherType = Attacher::AttachEngine3D
  Height = 3
  Length = 68.4
  Placement = pos=(-68.2,-78,32) rot=(0,0,1;0rad)
  Width = 17
FEATURE [Part::Chamfer] Chamfer049
  Base = -> Box554
  EdgeLinks = -> Box554 [Edge3,Edge7]
  Edges = 2 edges r=14: [Edge3,Edge7]
FEATURE [Part::Cylinder] Cylinder464  label="円柱464"
  Angle = 360
  AttacherType = Attacher::AttachEngine3D
  FirstAngle = 0
  Height = 40
  Placement = pos=(-9.8,-80,-5) rot=(0,0,1;0rad)
  Radius = 2
  SecondAngle = 0
FEATURE [Part::Cylinder] Cylinder465  label="円柱465"
  Angle = 360
  AttacherType = Attacher::AttachEngine3D
  FirstAngle = 0
  Height = 40
  Placement = pos=(-58.2,-80,-5) rot=(0,0,1;0rad)
  Radius = 2
  SecondAngle = 0
FEATURE [Part::Cylinder] Cylinder466  label="円柱466"
  Angle = 360
  AttacherType = Attacher::AttachEngine3D
  FirstAngle = 0
  Height = 5
  Placement = pos=(-9.8,-80,-5) rot=(0,0,1;0rad)
  Radius = 4
  SecondAngle = 0
FEATURE [Part::Cylinder] Cylinder467  label="円柱467"
  Angle = 360
  AttacherType = Attacher::AttachEngine3D
  FirstAngle = 0
  Height = 5
  Placement = pos=(-58.2,-80,-5) rot=(0,0,1;0rad)
  Radius = 4
  SecondAngle = 0
FEATURE [Part::Box] Box555  label="立方体527"
  AttacherType = Attacher::AttachEngine3D
  Height = 3
  Length = 10
  Placement = pos=(-63.2,-84,32) rot=(0,0,1;0rad)
  Width = 8
FEATURE [Part::Box] Box556  label="立方体528"
  AttacherType = Attacher::AttachEngine3D
  Height = 3
  Length = 10
  Placement = pos=(-14.8,-84,32) rot=(0,0,1;0rad)
  Width = 8
FEATURE [Part::MultiFuse] Fusion439
  Refine = true
  Shapes = -> [Cylinder464,Cylinder465]
FEATURE [Part::Cylinder] Cylinder468  label="円柱468"
  Angle = 360
  AttacherType = Attacher::AttachEngine3D
  FirstAngle = 0
  Height = 40
  Placement = pos=(-9.8,-80,-5) rot=(0,0,1;0rad)
  Radius = 2
  SecondAngle = 0
FEATURE [Part::Cylinder] Cylinder469  label="円柱469"
  Angle = 360
  AttacherType = Attacher::AttachEngine3D
  FirstAngle = 0
  Height = 40
  Placement = pos=(-58.2,-80,-5) rot=(0,0,1;0rad)
  Radius = 2
  SecondAngle = 0
FEATURE [Part::MultiFuse] Fusion440
  Refine = true
  Shapes = -> [Cylinder468,Cylinder469]
FEATURE [Part::MultiFuse] Fusion441
  Refine = true
  Shapes = -> [Cylinder466,Cylinder467]
FEATURE [Part::MultiFuse] Fusion442
  Refine = true
  Shapes = -> [Fusion440,Fusion441]
FEATURE [Part::MultiFuse] Fusion443
  Refine = true
  Shapes = -> [Box555,Chamfer049,Box556]
FEATURE [Part::Cut] Cut479
  Base = -> Fusion443
  Refine = true
  Tool = -> Fusion439
FEATURE [Part::MultiFuse] Fusion444
  Refine = true
  Shapes = -> [Fillet036,Box552,Box551]
FEATURE [Part::Cut] Cut480
  Base = -> Fusion444
  Refine = true
  Tool = -> Fusion442
FEATURE [Part::Cylinder] Cylinder472  label="円柱472"
  Angle = 360
  AttacherType = Attacher::AttachEngine3D
  FirstAngle = 0
  Height = 40
  Placement = pos=(-9.8,-80,0) rot=(0,0,1;0rad)
  Radius = 2
  SecondAngle = 0
FEATURE [Part::Cylinder] Cylinder473  label="円柱473"
  Angle = 360
  AttacherType = Attacher::AttachEngine3D
  FirstAngle = 0
  Height = 40
  Placement = pos=(-58.2,-80,0) rot=(0,0,1;0rad)
  Radius = 2
  SecondAngle = 0
FEATURE [Part::MultiFuse] Fusion445
  Refine = true
  Shapes = -> [Cylinder472,Cylinder473]
